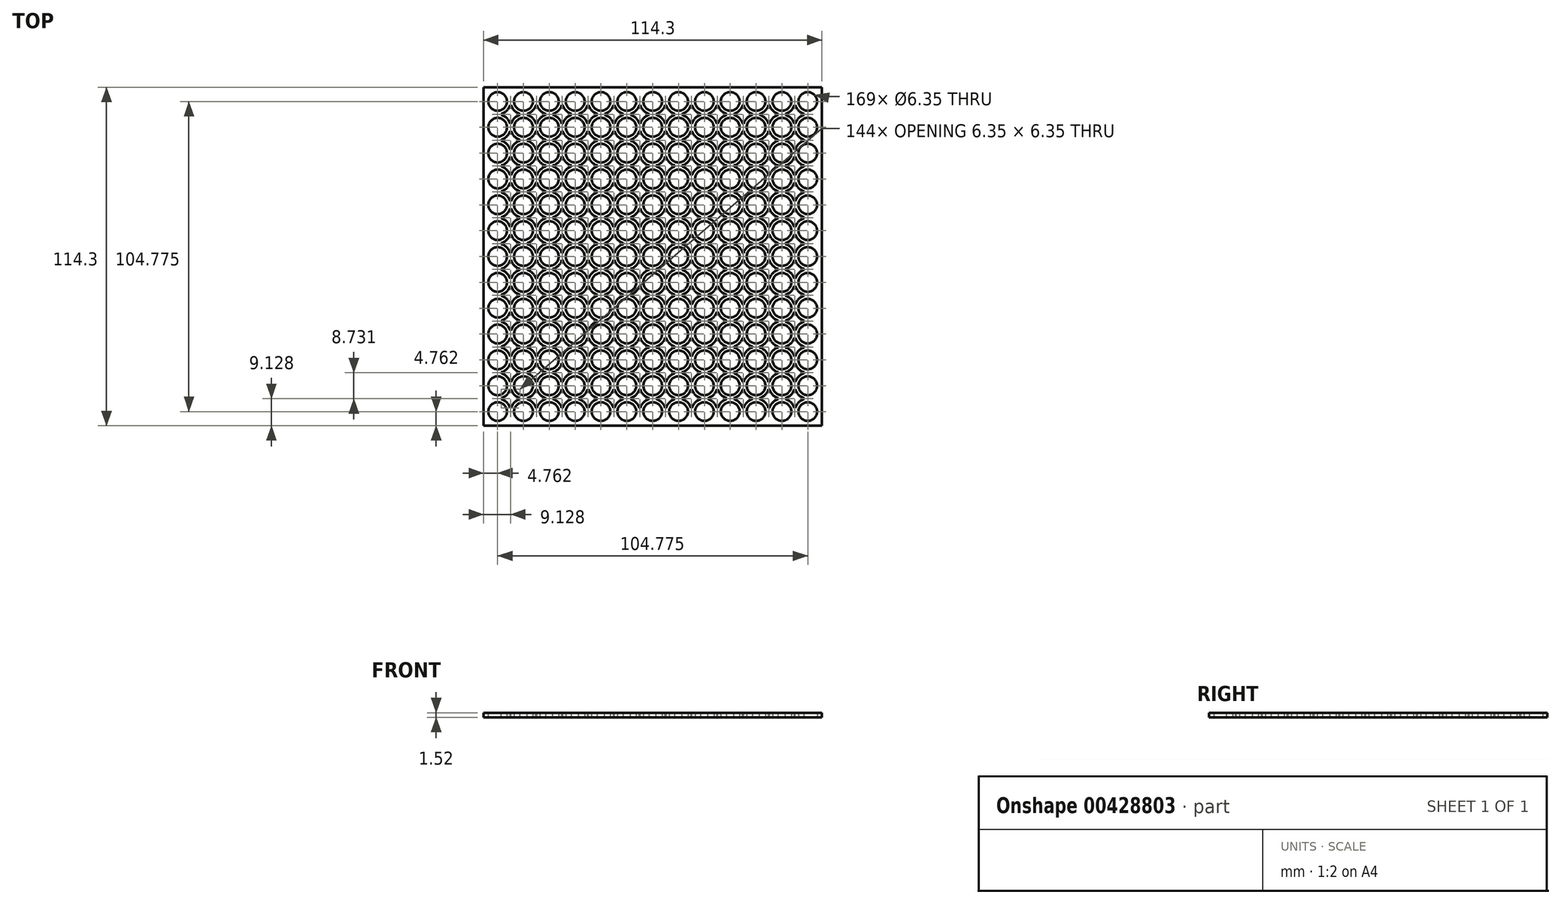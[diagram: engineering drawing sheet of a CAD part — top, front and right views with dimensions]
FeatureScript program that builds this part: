
annotation { "Feature Type Name" : "Feature", "Feature Type Description" : "" }
export const myFeature = defineFeature(function(context is Context, id is Id, definition is map)
    precondition{}
    {
        {
            var Q0;
            Q0=qCreatedBy(makeId("Top.planeOp"),FACE);
            var sketch = newSketch(context, id + "F0", { "sketchPlane" : qUnion([Q0])});
            skLineSegment(sketch, "E0.bottom", {"start": v(-57.15, -57.15) * mm, "end": v(57.15, -57.15) * mm});
            skLineSegment(sketch, "E0.top", {"start": v(-57.15, 57.15) * mm, "end": v(57.15, 57.15) * mm});
            skLineSegment(sketch, "E0.left", {"start": v(-57.15, -57.15) * mm, "end": v(-57.15, 57.15) * mm});
            skLineSegment(sketch, "E0.right", {"start": v(57.15, -57.15) * mm, "end": v(57.15, 57.15) * mm});
            skPoint(sketch, "E0.middle", {"position": v(0, 0) * mm});
            skCircle(sketch, "E1", {"center": v(-52.39, 52.39) * mm, "radius": 3.18 * mm});
            skLineSegment(sketch, "E2", {"start": v(-57.15, 52.39) * mm, "end": v(-52.39, 52.39) * mm, "construction": true});
            skLineSegment(sketch, "E3", {"start": v(-52.39, 57.15) * mm, "end": v(-52.39, 52.39) * mm, "construction": true});
            skLineSegment(sketch, "E4", {"start": v(-57.15, 52.39) * mm, "end": v(-55.56, 52.39) * mm, "construction": true});
            skCircle(sketch, "E5.0.1.0", {"center": v(-52.39, 43.66) * mm, "radius": 3.18 * mm});
            skCircle(sketch, "E5.0.2.0", {"center": v(-52.39, 34.93) * mm, "radius": 3.18 * mm});
            skCircle(sketch, "E5.0.3.0", {"center": v(-52.39, 26.2) * mm, "radius": 3.18 * mm});
            skCircle(sketch, "E5.0.4.0", {"center": v(-52.39, 17.46) * mm, "radius": 3.18 * mm});
            skCircle(sketch, "E5.0.5.0", {"center": v(-52.39, 8.73) * mm, "radius": 3.18 * mm});
            skCircle(sketch, "E5.0.6.0", {"center": v(-52.39, 0) * mm, "radius": 3.18 * mm});
            skCircle(sketch, "E5.0.7.0", {"center": v(-52.39, -8.73) * mm, "radius": 3.18 * mm});
            skCircle(sketch, "E5.0.8.0", {"center": v(-52.39, -17.46) * mm, "radius": 3.18 * mm});
            skCircle(sketch, "E5.0.9.0", {"center": v(-52.39, -26.2) * mm, "radius": 3.18 * mm});
            skCircle(sketch, "E5.0.10.0", {"center": v(-52.39, -34.93) * mm, "radius": 3.18 * mm});
            skCircle(sketch, "E5.0.11.0", {"center": v(-52.39, -43.66) * mm, "radius": 3.18 * mm});
            skCircle(sketch, "E5.0.12.0", {"center": v(-52.39, -52.39) * mm, "radius": 3.18 * mm});
            skCircle(sketch, "E5.1.0.0", {"center": v(-43.66, 52.39) * mm, "radius": 3.18 * mm});
            skCircle(sketch, "E5.1.1.0", {"center": v(-43.66, 43.66) * mm, "radius": 3.18 * mm});
            skCircle(sketch, "E5.1.2.0", {"center": v(-43.66, 34.93) * mm, "radius": 3.18 * mm});
            skCircle(sketch, "E5.1.3.0", {"center": v(-43.66, 26.2) * mm, "radius": 3.18 * mm});
            skCircle(sketch, "E5.1.4.0", {"center": v(-43.66, 17.46) * mm, "radius": 3.18 * mm});
            skCircle(sketch, "E5.1.5.0", {"center": v(-43.66, 8.73) * mm, "radius": 3.18 * mm});
            skCircle(sketch, "E5.1.6.0", {"center": v(-43.66, 0) * mm, "radius": 3.18 * mm});
            skCircle(sketch, "E5.1.7.0", {"center": v(-43.66, -8.73) * mm, "radius": 3.18 * mm});
            skCircle(sketch, "E5.1.8.0", {"center": v(-43.66, -17.46) * mm, "radius": 3.18 * mm});
            skCircle(sketch, "E5.1.9.0", {"center": v(-43.66, -26.2) * mm, "radius": 3.18 * mm});
            skCircle(sketch, "E5.1.10.0", {"center": v(-43.66, -34.93) * mm, "radius": 3.18 * mm});
            skCircle(sketch, "E5.1.11.0", {"center": v(-43.66, -43.66) * mm, "radius": 3.18 * mm});
            skCircle(sketch, "E5.1.12.0", {"center": v(-43.66, -52.39) * mm, "radius": 3.18 * mm});
            skCircle(sketch, "E5.2.0.0", {"center": v(-34.93, 52.39) * mm, "radius": 3.18 * mm});
            skCircle(sketch, "E5.2.1.0", {"center": v(-34.93, 43.66) * mm, "radius": 3.18 * mm});
            skCircle(sketch, "E5.2.2.0", {"center": v(-34.93, 34.93) * mm, "radius": 3.18 * mm});
            skCircle(sketch, "E5.2.3.0", {"center": v(-34.93, 26.2) * mm, "radius": 3.18 * mm});
            skCircle(sketch, "E5.2.4.0", {"center": v(-34.93, 17.46) * mm, "radius": 3.18 * mm});
            skCircle(sketch, "E5.2.5.0", {"center": v(-34.93, 8.73) * mm, "radius": 3.18 * mm});
            skCircle(sketch, "E5.2.6.0", {"center": v(-34.93, 0) * mm, "radius": 3.18 * mm});
            skCircle(sketch, "E5.2.7.0", {"center": v(-34.93, -8.73) * mm, "radius": 3.18 * mm});
            skCircle(sketch, "E5.2.8.0", {"center": v(-34.93, -17.46) * mm, "radius": 3.18 * mm});
            skCircle(sketch, "E5.2.9.0", {"center": v(-34.93, -26.2) * mm, "radius": 3.18 * mm});
            skCircle(sketch, "E5.2.10.0", {"center": v(-34.93, -34.93) * mm, "radius": 3.18 * mm});
            skCircle(sketch, "E5.2.11.0", {"center": v(-34.93, -43.66) * mm, "radius": 3.18 * mm});
            skCircle(sketch, "E5.2.12.0", {"center": v(-34.93, -52.39) * mm, "radius": 3.18 * mm});
            skCircle(sketch, "E5.3.0.0", {"center": v(-26.2, 52.39) * mm, "radius": 3.18 * mm});
            skCircle(sketch, "E5.3.1.0", {"center": v(-26.2, 43.66) * mm, "radius": 3.18 * mm});
            skCircle(sketch, "E5.3.2.0", {"center": v(-26.2, 34.93) * mm, "radius": 3.18 * mm});
            skCircle(sketch, "E5.3.3.0", {"center": v(-26.2, 26.2) * mm, "radius": 3.18 * mm});
            skCircle(sketch, "E5.3.4.0", {"center": v(-26.2, 17.46) * mm, "radius": 3.18 * mm});
            skCircle(sketch, "E5.3.5.0", {"center": v(-26.2, 8.73) * mm, "radius": 3.18 * mm});
            skCircle(sketch, "E5.3.6.0", {"center": v(-26.2, 0) * mm, "radius": 3.18 * mm});
            skCircle(sketch, "E5.3.7.0", {"center": v(-26.2, -8.73) * mm, "radius": 3.18 * mm});
            skCircle(sketch, "E5.3.8.0", {"center": v(-26.2, -17.46) * mm, "radius": 3.18 * mm});
            skCircle(sketch, "E5.3.9.0", {"center": v(-26.2, -26.2) * mm, "radius": 3.18 * mm});
            skCircle(sketch, "E5.3.10.0", {"center": v(-26.2, -34.93) * mm, "radius": 3.18 * mm});
            skCircle(sketch, "E5.3.11.0", {"center": v(-26.2, -43.66) * mm, "radius": 3.18 * mm});
            skCircle(sketch, "E5.3.12.0", {"center": v(-26.2, -52.39) * mm, "radius": 3.18 * mm});
            skCircle(sketch, "E5.4.0.0", {"center": v(-17.46, 52.39) * mm, "radius": 3.18 * mm});
            skCircle(sketch, "E5.4.1.0", {"center": v(-17.46, 43.66) * mm, "radius": 3.18 * mm});
            skCircle(sketch, "E5.4.2.0", {"center": v(-17.46, 34.93) * mm, "radius": 3.18 * mm});
            skCircle(sketch, "E5.4.3.0", {"center": v(-17.46, 26.2) * mm, "radius": 3.18 * mm});
            skCircle(sketch, "E5.4.4.0", {"center": v(-17.46, 17.46) * mm, "radius": 3.18 * mm});
            skCircle(sketch, "E5.4.5.0", {"center": v(-17.46, 8.73) * mm, "radius": 3.18 * mm});
            skCircle(sketch, "E5.4.6.0", {"center": v(-17.46, 0) * mm, "radius": 3.18 * mm});
            skCircle(sketch, "E5.4.7.0", {"center": v(-17.46, -8.73) * mm, "radius": 3.18 * mm});
            skCircle(sketch, "E5.4.8.0", {"center": v(-17.46, -17.46) * mm, "radius": 3.18 * mm});
            skCircle(sketch, "E5.4.9.0", {"center": v(-17.46, -26.2) * mm, "radius": 3.18 * mm});
            skCircle(sketch, "E5.4.10.0", {"center": v(-17.46, -34.93) * mm, "radius": 3.18 * mm});
            skCircle(sketch, "E5.4.11.0", {"center": v(-17.46, -43.66) * mm, "radius": 3.18 * mm});
            skCircle(sketch, "E5.4.12.0", {"center": v(-17.46, -52.39) * mm, "radius": 3.18 * mm});
            skCircle(sketch, "E5.5.0.0", {"center": v(-8.73, 52.39) * mm, "radius": 3.18 * mm});
            skCircle(sketch, "E5.5.1.0", {"center": v(-8.73, 43.66) * mm, "radius": 3.18 * mm});
            skCircle(sketch, "E5.5.2.0", {"center": v(-8.73, 34.93) * mm, "radius": 3.18 * mm});
            skCircle(sketch, "E5.5.3.0", {"center": v(-8.73, 26.2) * mm, "radius": 3.18 * mm});
            skCircle(sketch, "E5.5.4.0", {"center": v(-8.73, 17.46) * mm, "radius": 3.18 * mm});
            skCircle(sketch, "E5.5.5.0", {"center": v(-8.73, 8.73) * mm, "radius": 3.18 * mm});
            skCircle(sketch, "E5.5.6.0", {"center": v(-8.73, 0) * mm, "radius": 3.18 * mm});
            skCircle(sketch, "E5.5.7.0", {"center": v(-8.73, -8.73) * mm, "radius": 3.18 * mm});
            skCircle(sketch, "E5.5.8.0", {"center": v(-8.73, -17.46) * mm, "radius": 3.18 * mm});
            skCircle(sketch, "E5.5.9.0", {"center": v(-8.73, -26.2) * mm, "radius": 3.18 * mm});
            skCircle(sketch, "E5.5.10.0", {"center": v(-8.73, -34.93) * mm, "radius": 3.18 * mm});
            skCircle(sketch, "E5.5.11.0", {"center": v(-8.73, -43.66) * mm, "radius": 3.18 * mm});
            skCircle(sketch, "E5.5.12.0", {"center": v(-8.73, -52.39) * mm, "radius": 3.18 * mm});
            skCircle(sketch, "E5.6.0.0", {"center": v(0, 52.39) * mm, "radius": 3.18 * mm});
            skCircle(sketch, "E5.6.1.0", {"center": v(0, 43.66) * mm, "radius": 3.18 * mm});
            skCircle(sketch, "E5.6.2.0", {"center": v(0, 34.93) * mm, "radius": 3.18 * mm});
            skCircle(sketch, "E5.6.3.0", {"center": v(0, 26.2) * mm, "radius": 3.18 * mm});
            skCircle(sketch, "E5.6.4.0", {"center": v(0, 17.46) * mm, "radius": 3.18 * mm});
            skCircle(sketch, "E5.6.5.0", {"center": v(0, 8.73) * mm, "radius": 3.18 * mm});
            skCircle(sketch, "E5.6.6.0", {"center": v(0, 0) * mm, "radius": 3.18 * mm});
            skCircle(sketch, "E5.6.7.0", {"center": v(0, -8.73) * mm, "radius": 3.18 * mm});
            skCircle(sketch, "E5.6.8.0", {"center": v(0, -17.46) * mm, "radius": 3.18 * mm});
            skCircle(sketch, "E5.6.9.0", {"center": v(0, -26.2) * mm, "radius": 3.18 * mm});
            skCircle(sketch, "E5.6.10.0", {"center": v(0, -34.93) * mm, "radius": 3.18 * mm});
            skCircle(sketch, "E5.6.11.0", {"center": v(0, -43.66) * mm, "radius": 3.18 * mm});
            skCircle(sketch, "E5.6.12.0", {"center": v(0, -52.39) * mm, "radius": 3.18 * mm});
            skCircle(sketch, "E5.7.0.0", {"center": v(8.73, 52.39) * mm, "radius": 3.18 * mm});
            skCircle(sketch, "E5.7.1.0", {"center": v(8.73, 43.66) * mm, "radius": 3.18 * mm});
            skCircle(sketch, "E5.7.2.0", {"center": v(8.73, 34.93) * mm, "radius": 3.18 * mm});
            skCircle(sketch, "E5.7.3.0", {"center": v(8.73, 26.2) * mm, "radius": 3.18 * mm});
            skCircle(sketch, "E5.7.4.0", {"center": v(8.73, 17.46) * mm, "radius": 3.18 * mm});
            skCircle(sketch, "E5.7.5.0", {"center": v(8.73, 8.73) * mm, "radius": 3.18 * mm});
            skCircle(sketch, "E5.7.6.0", {"center": v(8.73, 0) * mm, "radius": 3.18 * mm});
            skCircle(sketch, "E5.7.7.0", {"center": v(8.73, -8.73) * mm, "radius": 3.18 * mm});
            skCircle(sketch, "E5.7.8.0", {"center": v(8.73, -17.46) * mm, "radius": 3.18 * mm});
            skCircle(sketch, "E5.7.9.0", {"center": v(8.73, -26.2) * mm, "radius": 3.18 * mm});
            skCircle(sketch, "E5.7.10.0", {"center": v(8.73, -34.93) * mm, "radius": 3.18 * mm});
            skCircle(sketch, "E5.7.11.0", {"center": v(8.73, -43.66) * mm, "radius": 3.18 * mm});
            skCircle(sketch, "E5.7.12.0", {"center": v(8.73, -52.39) * mm, "radius": 3.18 * mm});
            skCircle(sketch, "E5.8.0.0", {"center": v(17.46, 52.39) * mm, "radius": 3.18 * mm});
            skCircle(sketch, "E5.8.1.0", {"center": v(17.46, 43.66) * mm, "radius": 3.18 * mm});
            skCircle(sketch, "E5.8.2.0", {"center": v(17.46, 34.93) * mm, "radius": 3.18 * mm});
            skCircle(sketch, "E5.8.3.0", {"center": v(17.46, 26.2) * mm, "radius": 3.18 * mm});
            skCircle(sketch, "E5.8.4.0", {"center": v(17.46, 17.46) * mm, "radius": 3.18 * mm});
            skCircle(sketch, "E5.8.5.0", {"center": v(17.46, 8.73) * mm, "radius": 3.18 * mm});
            skCircle(sketch, "E5.8.6.0", {"center": v(17.46, 0) * mm, "radius": 3.18 * mm});
            skCircle(sketch, "E5.8.7.0", {"center": v(17.46, -8.73) * mm, "radius": 3.18 * mm});
            skCircle(sketch, "E5.8.8.0", {"center": v(17.46, -17.46) * mm, "radius": 3.18 * mm});
            skCircle(sketch, "E5.8.9.0", {"center": v(17.46, -26.2) * mm, "radius": 3.18 * mm});
            skCircle(sketch, "E5.8.10.0", {"center": v(17.46, -34.93) * mm, "radius": 3.18 * mm});
            skCircle(sketch, "E5.8.11.0", {"center": v(17.46, -43.66) * mm, "radius": 3.18 * mm});
            skCircle(sketch, "E5.8.12.0", {"center": v(17.46, -52.39) * mm, "radius": 3.18 * mm});
            skCircle(sketch, "E5.9.0.0", {"center": v(26.2, 52.39) * mm, "radius": 3.18 * mm});
            skCircle(sketch, "E5.9.1.0", {"center": v(26.2, 43.66) * mm, "radius": 3.18 * mm});
            skCircle(sketch, "E5.9.2.0", {"center": v(26.2, 34.93) * mm, "radius": 3.18 * mm});
            skCircle(sketch, "E5.9.3.0", {"center": v(26.2, 26.2) * mm, "radius": 3.18 * mm});
            skCircle(sketch, "E5.9.4.0", {"center": v(26.2, 17.46) * mm, "radius": 3.18 * mm});
            skCircle(sketch, "E5.9.5.0", {"center": v(26.2, 8.73) * mm, "radius": 3.18 * mm});
            skCircle(sketch, "E5.9.6.0", {"center": v(26.2, 0) * mm, "radius": 3.18 * mm});
            skCircle(sketch, "E5.9.7.0", {"center": v(26.2, -8.73) * mm, "radius": 3.18 * mm});
            skCircle(sketch, "E5.9.8.0", {"center": v(26.2, -17.46) * mm, "radius": 3.18 * mm});
            skCircle(sketch, "E5.9.9.0", {"center": v(26.2, -26.2) * mm, "radius": 3.18 * mm});
            skCircle(sketch, "E5.9.10.0", {"center": v(26.2, -34.93) * mm, "radius": 3.18 * mm});
            skCircle(sketch, "E5.9.11.0", {"center": v(26.2, -43.66) * mm, "radius": 3.18 * mm});
            skCircle(sketch, "E5.9.12.0", {"center": v(26.2, -52.39) * mm, "radius": 3.18 * mm});
            skCircle(sketch, "E5.10.0.0", {"center": v(34.93, 52.39) * mm, "radius": 3.18 * mm});
            skCircle(sketch, "E5.10.1.0", {"center": v(34.93, 43.66) * mm, "radius": 3.18 * mm});
            skCircle(sketch, "E5.10.2.0", {"center": v(34.93, 34.93) * mm, "radius": 3.18 * mm});
            skCircle(sketch, "E5.10.3.0", {"center": v(34.93, 26.2) * mm, "radius": 3.18 * mm});
            skCircle(sketch, "E5.10.4.0", {"center": v(34.93, 17.46) * mm, "radius": 3.18 * mm});
            skCircle(sketch, "E5.10.5.0", {"center": v(34.93, 8.73) * mm, "radius": 3.18 * mm});
            skCircle(sketch, "E5.10.6.0", {"center": v(34.93, 0) * mm, "radius": 3.18 * mm});
            skCircle(sketch, "E5.10.7.0", {"center": v(34.93, -8.73) * mm, "radius": 3.18 * mm});
            skCircle(sketch, "E5.10.8.0", {"center": v(34.93, -17.46) * mm, "radius": 3.18 * mm});
            skCircle(sketch, "E5.10.9.0", {"center": v(34.93, -26.2) * mm, "radius": 3.18 * mm});
            skCircle(sketch, "E5.10.10.0", {"center": v(34.93, -34.93) * mm, "radius": 3.18 * mm});
            skCircle(sketch, "E5.10.11.0", {"center": v(34.93, -43.66) * mm, "radius": 3.18 * mm});
            skCircle(sketch, "E5.10.12.0", {"center": v(34.93, -52.39) * mm, "radius": 3.18 * mm});
            skCircle(sketch, "E5.11.0.0", {"center": v(43.66, 52.39) * mm, "radius": 3.18 * mm});
            skCircle(sketch, "E5.11.1.0", {"center": v(43.66, 43.66) * mm, "radius": 3.18 * mm});
            skCircle(sketch, "E5.11.2.0", {"center": v(43.66, 34.93) * mm, "radius": 3.18 * mm});
            skCircle(sketch, "E5.11.3.0", {"center": v(43.66, 26.2) * mm, "radius": 3.18 * mm});
            skCircle(sketch, "E5.11.4.0", {"center": v(43.66, 17.46) * mm, "radius": 3.18 * mm});
            skCircle(sketch, "E5.11.5.0", {"center": v(43.66, 8.73) * mm, "radius": 3.18 * mm});
            skCircle(sketch, "E5.11.6.0", {"center": v(43.66, 0) * mm, "radius": 3.18 * mm});
            skCircle(sketch, "E5.11.7.0", {"center": v(43.66, -8.73) * mm, "radius": 3.18 * mm});
            skCircle(sketch, "E5.11.8.0", {"center": v(43.66, -17.46) * mm, "radius": 3.18 * mm});
            skCircle(sketch, "E5.11.9.0", {"center": v(43.66, -26.2) * mm, "radius": 3.18 * mm});
            skCircle(sketch, "E5.11.10.0", {"center": v(43.66, -34.93) * mm, "radius": 3.18 * mm});
            skCircle(sketch, "E5.11.11.0", {"center": v(43.66, -43.66) * mm, "radius": 3.18 * mm});
            skCircle(sketch, "E5.11.12.0", {"center": v(43.66, -52.39) * mm, "radius": 3.18 * mm});
            skCircle(sketch, "E5.12.0.0", {"center": v(52.39, 52.39) * mm, "radius": 3.18 * mm});
            skCircle(sketch, "E5.12.1.0", {"center": v(52.39, 43.66) * mm, "radius": 3.18 * mm});
            skCircle(sketch, "E5.12.2.0", {"center": v(52.39, 34.93) * mm, "radius": 3.18 * mm});
            skCircle(sketch, "E5.12.3.0", {"center": v(52.39, 26.2) * mm, "radius": 3.18 * mm});
            skCircle(sketch, "E5.12.4.0", {"center": v(52.39, 17.46) * mm, "radius": 3.18 * mm});
            skCircle(sketch, "E5.12.5.0", {"center": v(52.39, 8.73) * mm, "radius": 3.18 * mm});
            skCircle(sketch, "E5.12.6.0", {"center": v(52.39, 0) * mm, "radius": 3.18 * mm});
            skCircle(sketch, "E5.12.7.0", {"center": v(52.39, -8.73) * mm, "radius": 3.18 * mm});
            skCircle(sketch, "E5.12.8.0", {"center": v(52.39, -17.46) * mm, "radius": 3.18 * mm});
            skCircle(sketch, "E5.12.9.0", {"center": v(52.39, -26.2) * mm, "radius": 3.18 * mm});
            skCircle(sketch, "E5.12.10.0", {"center": v(52.39, -34.93) * mm, "radius": 3.18 * mm});
            skCircle(sketch, "E5.12.11.0", {"center": v(52.39, -43.66) * mm, "radius": 3.18 * mm});
            skCircle(sketch, "E5.12.12.0", {"center": v(52.39, -52.39) * mm, "radius": 3.18 * mm});
            skLineSegment(sketch, "E5.direction1", {"start": v(-52.39, 52.39) * mm, "end": v(-43.66, 52.39) * mm, "construction": true});
            skLineSegment(sketch, "E5.direction2", {"start": v(-52.39, 52.39) * mm, "end": v(-52.39, 43.66) * mm, "construction": true});
            skLineSegment(sketch, "E6", {"start": v(52.39, 52.39) * mm, "end": v(57.15, 52.39) * mm, "construction": true});
            skLineSegment(sketch, "E7", {"start": v(-52.39, -52.39) * mm, "end": v(-52.39, -57.15) * mm, "construction": true});
            skSolve(sketch);
        }
        {
            var Q0;
            Q0=makeQuery(id+"F0.imprint","IMPRINT",FACE,{"disambiguationData":[TD([[makeQuery(id+"F0.imprint","IMPRINT",EDGE,{"derivedFrom":sQuery(id+"F0.wireOp",EDGE,"E0.bottom")}),1.0]])]});
            extrude(context, id + "F1", {"entities" : qUnion([Q0]), "depth" : 1.52 * mm});
        }
        {
            var Q0;
            Q0=makeQuery(id+"F1.opExtrude","CAP_FACE",FACE,{"disambiguationData":[OSD([sQuery(id+"F0.wireOp",EDGE,"E0.bottom"),sQuery(id+"F0.wireOp",EDGE,"E0.top"),sQuery(id+"F0.wireOp",EDGE,"E0.left"),sQuery(id+"F0.wireOp",EDGE,"E0.right"),sQuery(id+"F0.wireOp",EDGE,"E1"),sQuery(id+"F0.wireOp",EDGE,"E5.0.1.0"),sQuery(id+"F0.wireOp",EDGE,"E5.0.2.0"),sQuery(id+"F0.wireOp",EDGE,"E5.0.3.0"),sQuery(id+"F0.wireOp",EDGE,"E5.0.4.0"),sQuery(id+"F0.wireOp",EDGE,"E5.0.5.0"),sQuery(id+"F0.wireOp",EDGE,"E5.0.6.0"),sQuery(id+"F0.wireOp",EDGE,"E5.0.7.0"),sQuery(id+"F0.wireOp",EDGE,"E5.0.8.0"),sQuery(id+"F0.wireOp",EDGE,"E5.0.9.0"),sQuery(id+"F0.wireOp",EDGE,"E5.0.10.0"),sQuery(id+"F0.wireOp",EDGE,"E5.0.11.0"),sQuery(id+"F0.wireOp",EDGE,"E5.0.12.0"),sQuery(id+"F0.wireOp",EDGE,"E5.1.0.0"),sQuery(id+"F0.wireOp",EDGE,"E5.1.1.0"),sQuery(id+"F0.wireOp",EDGE,"E5.1.2.0"),sQuery(id+"F0.wireOp",EDGE,"E5.1.3.0"),sQuery(id+"F0.wireOp",EDGE,"E5.1.4.0"),sQuery(id+"F0.wireOp",EDGE,"E5.1.5.0"),sQuery(id+"F0.wireOp",EDGE,"E5.1.6.0"),sQuery(id+"F0.wireOp",EDGE,"E5.1.7.0"),sQuery(id+"F0.wireOp",EDGE,"E5.1.8.0"),sQuery(id+"F0.wireOp",EDGE,"E5.1.9.0"),sQuery(id+"F0.wireOp",EDGE,"E5.1.10.0"),sQuery(id+"F0.wireOp",EDGE,"E5.1.11.0"),sQuery(id+"F0.wireOp",EDGE,"E5.1.12.0"),sQuery(id+"F0.wireOp",EDGE,"E5.2.0.0"),sQuery(id+"F0.wireOp",EDGE,"E5.2.1.0"),sQuery(id+"F0.wireOp",EDGE,"E5.2.2.0"),sQuery(id+"F0.wireOp",EDGE,"E5.2.3.0"),sQuery(id+"F0.wireOp",EDGE,"E5.2.4.0"),sQuery(id+"F0.wireOp",EDGE,"E5.2.5.0"),sQuery(id+"F0.wireOp",EDGE,"E5.2.6.0"),sQuery(id+"F0.wireOp",EDGE,"E5.2.7.0"),sQuery(id+"F0.wireOp",EDGE,"E5.2.8.0"),sQuery(id+"F0.wireOp",EDGE,"E5.2.9.0"),sQuery(id+"F0.wireOp",EDGE,"E5.2.10.0"),sQuery(id+"F0.wireOp",EDGE,"E5.2.11.0"),sQuery(id+"F0.wireOp",EDGE,"E5.2.12.0"),sQuery(id+"F0.wireOp",EDGE,"E5.3.0.0"),sQuery(id+"F0.wireOp",EDGE,"E5.3.1.0"),sQuery(id+"F0.wireOp",EDGE,"E5.3.2.0"),sQuery(id+"F0.wireOp",EDGE,"E5.3.3.0"),sQuery(id+"F0.wireOp",EDGE,"E5.3.4.0"),sQuery(id+"F0.wireOp",EDGE,"E5.3.5.0"),sQuery(id+"F0.wireOp",EDGE,"E5.3.6.0"),sQuery(id+"F0.wireOp",EDGE,"E5.3.7.0"),sQuery(id+"F0.wireOp",EDGE,"E5.3.8.0"),sQuery(id+"F0.wireOp",EDGE,"E5.3.9.0"),sQuery(id+"F0.wireOp",EDGE,"E5.3.10.0"),sQuery(id+"F0.wireOp",EDGE,"E5.3.11.0"),sQuery(id+"F0.wireOp",EDGE,"E5.3.12.0"),sQuery(id+"F0.wireOp",EDGE,"E5.4.0.0"),sQuery(id+"F0.wireOp",EDGE,"E5.4.1.0"),sQuery(id+"F0.wireOp",EDGE,"E5.4.2.0"),sQuery(id+"F0.wireOp",EDGE,"E5.4.3.0"),sQuery(id+"F0.wireOp",EDGE,"E5.4.4.0"),sQuery(id+"F0.wireOp",EDGE,"E5.4.5.0"),sQuery(id+"F0.wireOp",EDGE,"E5.4.6.0"),sQuery(id+"F0.wireOp",EDGE,"E5.4.7.0"),sQuery(id+"F0.wireOp",EDGE,"E5.4.8.0"),sQuery(id+"F0.wireOp",EDGE,"E5.4.9.0"),sQuery(id+"F0.wireOp",EDGE,"E5.4.10.0"),sQuery(id+"F0.wireOp",EDGE,"E5.4.11.0"),sQuery(id+"F0.wireOp",EDGE,"E5.4.12.0"),sQuery(id+"F0.wireOp",EDGE,"E5.5.0.0"),sQuery(id+"F0.wireOp",EDGE,"E5.5.1.0"),sQuery(id+"F0.wireOp",EDGE,"E5.5.2.0"),sQuery(id+"F0.wireOp",EDGE,"E5.5.3.0"),sQuery(id+"F0.wireOp",EDGE,"E5.5.4.0"),sQuery(id+"F0.wireOp",EDGE,"E5.5.5.0"),sQuery(id+"F0.wireOp",EDGE,"E5.5.6.0"),sQuery(id+"F0.wireOp",EDGE,"E5.5.7.0"),sQuery(id+"F0.wireOp",EDGE,"E5.5.8.0"),sQuery(id+"F0.wireOp",EDGE,"E5.5.9.0"),sQuery(id+"F0.wireOp",EDGE,"E5.5.10.0"),sQuery(id+"F0.wireOp",EDGE,"E5.5.11.0"),sQuery(id+"F0.wireOp",EDGE,"E5.5.12.0"),sQuery(id+"F0.wireOp",EDGE,"E5.6.0.0"),sQuery(id+"F0.wireOp",EDGE,"E5.6.1.0"),sQuery(id+"F0.wireOp",EDGE,"E5.6.2.0"),sQuery(id+"F0.wireOp",EDGE,"E5.6.3.0"),sQuery(id+"F0.wireOp",EDGE,"E5.6.4.0"),sQuery(id+"F0.wireOp",EDGE,"E5.6.5.0"),sQuery(id+"F0.wireOp",EDGE,"E5.6.6.0"),sQuery(id+"F0.wireOp",EDGE,"E5.6.7.0"),sQuery(id+"F0.wireOp",EDGE,"E5.6.8.0"),sQuery(id+"F0.wireOp",EDGE,"E5.6.9.0"),sQuery(id+"F0.wireOp",EDGE,"E5.6.10.0"),sQuery(id+"F0.wireOp",EDGE,"E5.6.11.0"),sQuery(id+"F0.wireOp",EDGE,"E5.6.12.0"),sQuery(id+"F0.wireOp",EDGE,"E5.7.0.0"),sQuery(id+"F0.wireOp",EDGE,"E5.7.1.0"),sQuery(id+"F0.wireOp",EDGE,"E5.7.2.0"),sQuery(id+"F0.wireOp",EDGE,"E5.7.3.0"),sQuery(id+"F0.wireOp",EDGE,"E5.7.4.0"),sQuery(id+"F0.wireOp",EDGE,"E5.7.5.0"),sQuery(id+"F0.wireOp",EDGE,"E5.7.6.0"),sQuery(id+"F0.wireOp",EDGE,"E5.7.7.0"),sQuery(id+"F0.wireOp",EDGE,"E5.7.8.0"),sQuery(id+"F0.wireOp",EDGE,"E5.7.9.0"),sQuery(id+"F0.wireOp",EDGE,"E5.7.10.0"),sQuery(id+"F0.wireOp",EDGE,"E5.7.11.0"),sQuery(id+"F0.wireOp",EDGE,"E5.7.12.0"),sQuery(id+"F0.wireOp",EDGE,"E5.8.0.0"),sQuery(id+"F0.wireOp",EDGE,"E5.8.1.0"),sQuery(id+"F0.wireOp",EDGE,"E5.8.2.0"),sQuery(id+"F0.wireOp",EDGE,"E5.8.3.0"),sQuery(id+"F0.wireOp",EDGE,"E5.8.4.0"),sQuery(id+"F0.wireOp",EDGE,"E5.8.5.0"),sQuery(id+"F0.wireOp",EDGE,"E5.8.6.0"),sQuery(id+"F0.wireOp",EDGE,"E5.8.7.0"),sQuery(id+"F0.wireOp",EDGE,"E5.8.8.0"),sQuery(id+"F0.wireOp",EDGE,"E5.8.9.0"),sQuery(id+"F0.wireOp",EDGE,"E5.8.10.0"),sQuery(id+"F0.wireOp",EDGE,"E5.8.11.0"),sQuery(id+"F0.wireOp",EDGE,"E5.8.12.0"),sQuery(id+"F0.wireOp",EDGE,"E5.9.0.0"),sQuery(id+"F0.wireOp",EDGE,"E5.9.1.0"),sQuery(id+"F0.wireOp",EDGE,"E5.9.2.0"),sQuery(id+"F0.wireOp",EDGE,"E5.9.3.0"),sQuery(id+"F0.wireOp",EDGE,"E5.9.4.0"),sQuery(id+"F0.wireOp",EDGE,"E5.9.5.0"),sQuery(id+"F0.wireOp",EDGE,"E5.9.6.0"),sQuery(id+"F0.wireOp",EDGE,"E5.9.7.0"),sQuery(id+"F0.wireOp",EDGE,"E5.9.8.0"),sQuery(id+"F0.wireOp",EDGE,"E5.9.9.0"),sQuery(id+"F0.wireOp",EDGE,"E5.9.10.0"),sQuery(id+"F0.wireOp",EDGE,"E5.9.11.0"),sQuery(id+"F0.wireOp",EDGE,"E5.9.12.0"),sQuery(id+"F0.wireOp",EDGE,"E5.10.0.0"),sQuery(id+"F0.wireOp",EDGE,"E5.10.1.0"),sQuery(id+"F0.wireOp",EDGE,"E5.10.2.0"),sQuery(id+"F0.wireOp",EDGE,"E5.10.3.0"),sQuery(id+"F0.wireOp",EDGE,"E5.10.4.0"),sQuery(id+"F0.wireOp",EDGE,"E5.10.5.0"),sQuery(id+"F0.wireOp",EDGE,"E5.10.6.0"),sQuery(id+"F0.wireOp",EDGE,"E5.10.7.0"),sQuery(id+"F0.wireOp",EDGE,"E5.10.8.0"),sQuery(id+"F0.wireOp",EDGE,"E5.10.9.0"),sQuery(id+"F0.wireOp",EDGE,"E5.10.10.0"),sQuery(id+"F0.wireOp",EDGE,"E5.10.11.0"),sQuery(id+"F0.wireOp",EDGE,"E5.10.12.0"),sQuery(id+"F0.wireOp",EDGE,"E5.11.0.0"),sQuery(id+"F0.wireOp",EDGE,"E5.11.1.0"),sQuery(id+"F0.wireOp",EDGE,"E5.11.2.0"),sQuery(id+"F0.wireOp",EDGE,"E5.11.3.0"),sQuery(id+"F0.wireOp",EDGE,"E5.11.4.0"),sQuery(id+"F0.wireOp",EDGE,"E5.11.5.0"),sQuery(id+"F0.wireOp",EDGE,"E5.11.6.0"),sQuery(id+"F0.wireOp",EDGE,"E5.11.7.0"),sQuery(id+"F0.wireOp",EDGE,"E5.11.8.0"),sQuery(id+"F0.wireOp",EDGE,"E5.11.9.0"),sQuery(id+"F0.wireOp",EDGE,"E5.11.10.0"),sQuery(id+"F0.wireOp",EDGE,"E5.11.11.0"),sQuery(id+"F0.wireOp",EDGE,"E5.11.12.0"),sQuery(id+"F0.wireOp",EDGE,"E5.12.0.0"),sQuery(id+"F0.wireOp",EDGE,"E5.12.1.0"),sQuery(id+"F0.wireOp",EDGE,"E5.12.2.0"),sQuery(id+"F0.wireOp",EDGE,"E5.12.3.0"),sQuery(id+"F0.wireOp",EDGE,"E5.12.4.0"),sQuery(id+"F0.wireOp",EDGE,"E5.12.5.0"),sQuery(id+"F0.wireOp",EDGE,"E5.12.6.0"),sQuery(id+"F0.wireOp",EDGE,"E5.12.7.0"),sQuery(id+"F0.wireOp",EDGE,"E5.12.8.0"),sQuery(id+"F0.wireOp",EDGE,"E5.12.9.0"),sQuery(id+"F0.wireOp",EDGE,"E5.12.10.0"),sQuery(id+"F0.wireOp",EDGE,"E5.12.11.0"),sQuery(id+"F0.wireOp",EDGE,"E5.12.12.0")])],"isStart":false});
            var sketch = newSketch(context, id + "F2", { "sketchPlane" : qUnion([Q0])});
            skArc(sketch, "E8", {"start": v(-51.2, 48.19) * mm, "mid": v(-49.3, 49.3) * mm, "end": v(-48.19, 51.2) * mm});
            skArc(sketch, "E9", {"start": v(-47.86, 51.2) * mm, "mid": v(-46.74, 49.3) * mm, "end": v(-44.85, 48.19) * mm});
            skArc(sketch, "E10", {"start": v(-44.85, 47.86) * mm, "mid": v(-46.74, 46.74) * mm, "end": v(-47.86, 44.85) * mm});
            skArc(sketch, "E11", {"start": v(-48.19, 44.85) * mm, "mid": v(-49.3, 46.74) * mm, "end": v(-51.2, 47.86) * mm});
            skLineSegment(sketch, "E12", {"start": v(-52.39, 52.39) * mm, "end": v(-43.66, 43.66) * mm, "construction": true});
            skArc(sketch, "E13", {"start": v(-51.2, 48.19) * mm, "mid": v(-51.2, 48.02) * mm, "end": v(-51.2, 47.86) * mm});
            skArc(sketch, "E14.trimOffspring", {"start": v(-47.86, 51.2) * mm, "mid": v(-48.02, 51.2) * mm, "end": v(-48.19, 51.2) * mm});
            skArc(sketch, "E15.trimOffspring", {"start": v(-44.85, 47.86) * mm, "mid": v(-44.85, 48.02) * mm, "end": v(-44.85, 48.19) * mm});
            skArc(sketch, "E16.trimOffspring", {"start": v(-48.19, 44.85) * mm, "mid": v(-48.02, 44.85) * mm, "end": v(-47.86, 44.85) * mm});
            skArc(sketch, "E17.0.1.0", {"start": v(-47.86, 42.46) * mm, "mid": v(-46.74, 40.57) * mm, "end": v(-44.85, 39.46) * mm});
            skArc(sketch, "E17.0.1.1", {"start": v(-51.2, 39.46) * mm, "mid": v(-49.3, 40.57) * mm, "end": v(-48.19, 42.46) * mm});
            skArc(sketch, "E17.0.1.2", {"start": v(-47.86, 42.46) * mm, "mid": v(-48.02, 42.47) * mm, "end": v(-48.19, 42.46) * mm});
            skArc(sketch, "E17.0.1.3", {"start": v(-51.2, 39.46) * mm, "mid": v(-51.2, 39.3) * mm, "end": v(-51.2, 39.12) * mm});
            skArc(sketch, "E17.0.1.4", {"start": v(-48.19, 36.12) * mm, "mid": v(-49.3, 38.01) * mm, "end": v(-51.2, 39.12) * mm});
            skArc(sketch, "E17.0.1.5", {"start": v(-44.85, 39.12) * mm, "mid": v(-46.74, 38.01) * mm, "end": v(-47.86, 36.12) * mm});
            skArc(sketch, "E17.0.1.6", {"start": v(-48.19, 36.12) * mm, "mid": v(-48.02, 36.12) * mm, "end": v(-47.86, 36.12) * mm});
            skArc(sketch, "E17.0.1.7", {"start": v(-44.85, 39.12) * mm, "mid": v(-44.85, 39.3) * mm, "end": v(-44.85, 39.46) * mm});
            skArc(sketch, "E17.0.2.0", {"start": v(-47.86, 33.73) * mm, "mid": v(-46.74, 31.84) * mm, "end": v(-44.85, 30.73) * mm});
            skArc(sketch, "E17.0.2.1", {"start": v(-51.2, 30.73) * mm, "mid": v(-49.3, 31.84) * mm, "end": v(-48.19, 33.73) * mm});
            skArc(sketch, "E17.0.2.2", {"start": v(-47.86, 33.73) * mm, "mid": v(-48.02, 33.73) * mm, "end": v(-48.19, 33.73) * mm});
            skArc(sketch, "E17.0.2.3", {"start": v(-51.2, 30.73) * mm, "mid": v(-51.2, 30.56) * mm, "end": v(-51.2, 30.4) * mm});
            skArc(sketch, "E17.0.2.4", {"start": v(-48.19, 27.39) * mm, "mid": v(-49.3, 29.28) * mm, "end": v(-51.2, 30.4) * mm});
            skArc(sketch, "E17.0.2.5", {"start": v(-44.85, 30.4) * mm, "mid": v(-46.74, 29.28) * mm, "end": v(-47.86, 27.39) * mm});
            skArc(sketch, "E17.0.2.6", {"start": v(-48.19, 27.39) * mm, "mid": v(-48.02, 27.38) * mm, "end": v(-47.86, 27.39) * mm});
            skArc(sketch, "E17.0.2.7", {"start": v(-44.85, 30.4) * mm, "mid": v(-44.85, 30.56) * mm, "end": v(-44.85, 30.73) * mm});
            skArc(sketch, "E17.0.3.0", {"start": v(-47.86, 25) * mm, "mid": v(-46.74, 23.1) * mm, "end": v(-44.85, 22) * mm});
            skArc(sketch, "E17.0.3.1", {"start": v(-51.2, 22) * mm, "mid": v(-49.3, 23.1) * mm, "end": v(-48.19, 25) * mm});
            skArc(sketch, "E17.0.3.2", {"start": v(-47.86, 25) * mm, "mid": v(-48.02, 25) * mm, "end": v(-48.19, 25) * mm});
            skArc(sketch, "E17.0.3.3", {"start": v(-51.2, 22) * mm, "mid": v(-51.2, 21.83) * mm, "end": v(-51.2, 21.66) * mm});
            skArc(sketch, "E17.0.3.4", {"start": v(-48.19, 18.66) * mm, "mid": v(-49.3, 20.55) * mm, "end": v(-51.2, 21.66) * mm});
            skArc(sketch, "E17.0.3.5", {"start": v(-44.85, 21.66) * mm, "mid": v(-46.74, 20.55) * mm, "end": v(-47.86, 18.66) * mm});
            skArc(sketch, "E17.0.3.6", {"start": v(-48.19, 18.66) * mm, "mid": v(-48.02, 18.65) * mm, "end": v(-47.86, 18.66) * mm});
            skArc(sketch, "E17.0.3.7", {"start": v(-44.85, 21.66) * mm, "mid": v(-44.85, 21.83) * mm, "end": v(-44.85, 22) * mm});
            skArc(sketch, "E17.0.4.0", {"start": v(-47.86, 16.27) * mm, "mid": v(-46.74, 14.38) * mm, "end": v(-44.85, 13.26) * mm});
            skArc(sketch, "E17.0.4.1", {"start": v(-51.2, 13.26) * mm, "mid": v(-49.3, 14.38) * mm, "end": v(-48.19, 16.27) * mm});
            skArc(sketch, "E17.0.4.2", {"start": v(-47.86, 16.27) * mm, "mid": v(-48.02, 16.27) * mm, "end": v(-48.19, 16.27) * mm});
            skArc(sketch, "E17.0.4.3", {"start": v(-51.2, 13.26) * mm, "mid": v(-51.2, 13.1) * mm, "end": v(-51.2, 12.93) * mm});
            skArc(sketch, "E17.0.4.4", {"start": v(-48.19, 9.93) * mm, "mid": v(-49.3, 11.82) * mm, "end": v(-51.2, 12.93) * mm});
            skArc(sketch, "E17.0.4.5", {"start": v(-44.85, 12.93) * mm, "mid": v(-46.74, 11.82) * mm, "end": v(-47.86, 9.93) * mm});
            skArc(sketch, "E17.0.4.6", {"start": v(-48.19, 9.93) * mm, "mid": v(-48.02, 9.92) * mm, "end": v(-47.86, 9.93) * mm});
            skArc(sketch, "E17.0.4.7", {"start": v(-44.85, 12.93) * mm, "mid": v(-44.85, 13.1) * mm, "end": v(-44.85, 13.26) * mm});
            skArc(sketch, "E17.0.5.0", {"start": v(-47.86, 7.54) * mm, "mid": v(-46.74, 5.64) * mm, "end": v(-44.85, 4.53) * mm});
            skArc(sketch, "E17.0.5.1", {"start": v(-51.2, 4.53) * mm, "mid": v(-49.3, 5.64) * mm, "end": v(-48.19, 7.54) * mm});
            skArc(sketch, "E17.0.5.2", {"start": v(-47.86, 7.54) * mm, "mid": v(-48.02, 7.54) * mm, "end": v(-48.19, 7.54) * mm});
            skArc(sketch, "E17.0.5.3", {"start": v(-51.2, 4.53) * mm, "mid": v(-51.2, 4.37) * mm, "end": v(-51.2, 4.2) * mm});
            skArc(sketch, "E17.0.5.4", {"start": v(-48.19, 1.2) * mm, "mid": v(-49.3, 3.09) * mm, "end": v(-51.2, 4.2) * mm});
            skArc(sketch, "E17.0.5.5", {"start": v(-44.85, 4.2) * mm, "mid": v(-46.74, 3.09) * mm, "end": v(-47.86, 1.2) * mm});
            skArc(sketch, "E17.0.5.6", {"start": v(-48.19, 1.2) * mm, "mid": v(-48.02, 1.2) * mm, "end": v(-47.86, 1.2) * mm});
            skArc(sketch, "E17.0.5.7", {"start": v(-44.85, 4.2) * mm, "mid": v(-44.85, 4.37) * mm, "end": v(-44.85, 4.53) * mm});
            skArc(sketch, "E17.0.6.0", {"start": v(-47.86, -1.2) * mm, "mid": v(-46.74, -3.09) * mm, "end": v(-44.85, -4.2) * mm});
            skArc(sketch, "E17.0.6.1", {"start": v(-51.2, -4.2) * mm, "mid": v(-49.3, -3.09) * mm, "end": v(-48.19, -1.2) * mm});
            skArc(sketch, "E17.0.6.2", {"start": v(-47.86, -1.2) * mm, "mid": v(-48.02, -1.2) * mm, "end": v(-48.19, -1.2) * mm});
            skArc(sketch, "E17.0.6.3", {"start": v(-51.2, -4.2) * mm, "mid": v(-51.2, -4.37) * mm, "end": v(-51.2, -4.53) * mm});
            skArc(sketch, "E17.0.6.4", {"start": v(-48.19, -7.54) * mm, "mid": v(-49.3, -5.64) * mm, "end": v(-51.2, -4.53) * mm});
            skArc(sketch, "E17.0.6.5", {"start": v(-44.85, -4.53) * mm, "mid": v(-46.74, -5.64) * mm, "end": v(-47.86, -7.54) * mm});
            skArc(sketch, "E17.0.6.6", {"start": v(-48.19, -7.54) * mm, "mid": v(-48.02, -7.54) * mm, "end": v(-47.86, -7.54) * mm});
            skArc(sketch, "E17.0.6.7", {"start": v(-44.85, -4.53) * mm, "mid": v(-44.85, -4.37) * mm, "end": v(-44.85, -4.2) * mm});
            skArc(sketch, "E17.0.7.0", {"start": v(-47.86, -9.93) * mm, "mid": v(-46.74, -11.82) * mm, "end": v(-44.85, -12.93) * mm});
            skArc(sketch, "E17.0.7.1", {"start": v(-51.2, -12.93) * mm, "mid": v(-49.3, -11.82) * mm, "end": v(-48.19, -9.93) * mm});
            skArc(sketch, "E17.0.7.2", {"start": v(-47.86, -9.93) * mm, "mid": v(-48.02, -9.92) * mm, "end": v(-48.19, -9.93) * mm});
            skArc(sketch, "E17.0.7.3", {"start": v(-51.2, -12.93) * mm, "mid": v(-51.2, -13.1) * mm, "end": v(-51.2, -13.26) * mm});
            skArc(sketch, "E17.0.7.4", {"start": v(-48.19, -16.27) * mm, "mid": v(-49.3, -14.38) * mm, "end": v(-51.2, -13.26) * mm});
            skArc(sketch, "E17.0.7.5", {"start": v(-44.85, -13.26) * mm, "mid": v(-46.74, -14.38) * mm, "end": v(-47.86, -16.27) * mm});
            skArc(sketch, "E17.0.7.6", {"start": v(-48.19, -16.27) * mm, "mid": v(-48.02, -16.27) * mm, "end": v(-47.86, -16.27) * mm});
            skArc(sketch, "E17.0.7.7", {"start": v(-44.85, -13.26) * mm, "mid": v(-44.85, -13.1) * mm, "end": v(-44.85, -12.93) * mm});
            skArc(sketch, "E17.0.8.0", {"start": v(-47.86, -18.66) * mm, "mid": v(-46.74, -20.55) * mm, "end": v(-44.85, -21.66) * mm});
            skArc(sketch, "E17.0.8.1", {"start": v(-51.2, -21.66) * mm, "mid": v(-49.3, -20.55) * mm, "end": v(-48.19, -18.66) * mm});
            skArc(sketch, "E17.0.8.2", {"start": v(-47.86, -18.66) * mm, "mid": v(-48.02, -18.65) * mm, "end": v(-48.19, -18.66) * mm});
            skArc(sketch, "E17.0.8.3", {"start": v(-51.2, -21.66) * mm, "mid": v(-51.2, -21.83) * mm, "end": v(-51.2, -22) * mm});
            skArc(sketch, "E17.0.8.4", {"start": v(-48.19, -25) * mm, "mid": v(-49.3, -23.1) * mm, "end": v(-51.2, -22) * mm});
            skArc(sketch, "E17.0.8.5", {"start": v(-44.85, -22) * mm, "mid": v(-46.74, -23.1) * mm, "end": v(-47.86, -25) * mm});
            skArc(sketch, "E17.0.8.6", {"start": v(-48.19, -25) * mm, "mid": v(-48.02, -25) * mm, "end": v(-47.86, -25) * mm});
            skArc(sketch, "E17.0.8.7", {"start": v(-44.85, -22) * mm, "mid": v(-44.85, -21.83) * mm, "end": v(-44.85, -21.66) * mm});
            skArc(sketch, "E17.0.9.0", {"start": v(-47.86, -27.39) * mm, "mid": v(-46.74, -29.28) * mm, "end": v(-44.85, -30.4) * mm});
            skArc(sketch, "E17.0.9.1", {"start": v(-51.2, -30.4) * mm, "mid": v(-49.3, -29.28) * mm, "end": v(-48.19, -27.39) * mm});
            skArc(sketch, "E17.0.9.2", {"start": v(-47.86, -27.39) * mm, "mid": v(-48.02, -27.38) * mm, "end": v(-48.19, -27.39) * mm});
            skArc(sketch, "E17.0.9.3", {"start": v(-51.2, -30.4) * mm, "mid": v(-51.2, -30.56) * mm, "end": v(-51.2, -30.73) * mm});
            skArc(sketch, "E17.0.9.4", {"start": v(-48.19, -33.73) * mm, "mid": v(-49.3, -31.84) * mm, "end": v(-51.2, -30.73) * mm});
            skArc(sketch, "E17.0.9.5", {"start": v(-44.85, -30.73) * mm, "mid": v(-46.74, -31.84) * mm, "end": v(-47.86, -33.73) * mm});
            skArc(sketch, "E17.0.9.6", {"start": v(-48.19, -33.73) * mm, "mid": v(-48.02, -33.73) * mm, "end": v(-47.86, -33.73) * mm});
            skArc(sketch, "E17.0.9.7", {"start": v(-44.85, -30.73) * mm, "mid": v(-44.85, -30.56) * mm, "end": v(-44.85, -30.4) * mm});
            skArc(sketch, "E17.0.10.0", {"start": v(-47.86, -36.12) * mm, "mid": v(-46.74, -38.01) * mm, "end": v(-44.85, -39.12) * mm});
            skArc(sketch, "E17.0.10.1", {"start": v(-51.2, -39.12) * mm, "mid": v(-49.3, -38.01) * mm, "end": v(-48.19, -36.12) * mm});
            skArc(sketch, "E17.0.10.2", {"start": v(-47.86, -36.12) * mm, "mid": v(-48.02, -36.12) * mm, "end": v(-48.19, -36.12) * mm});
            skArc(sketch, "E17.0.10.3", {"start": v(-51.2, -39.12) * mm, "mid": v(-51.2, -39.3) * mm, "end": v(-51.2, -39.46) * mm});
            skArc(sketch, "E17.0.10.4", {"start": v(-48.19, -42.46) * mm, "mid": v(-49.3, -40.57) * mm, "end": v(-51.2, -39.46) * mm});
            skArc(sketch, "E17.0.10.5", {"start": v(-44.85, -39.46) * mm, "mid": v(-46.74, -40.57) * mm, "end": v(-47.86, -42.46) * mm});
            skArc(sketch, "E17.0.10.6", {"start": v(-48.19, -42.46) * mm, "mid": v(-48.02, -42.47) * mm, "end": v(-47.86, -42.46) * mm});
            skArc(sketch, "E17.0.10.7", {"start": v(-44.85, -39.46) * mm, "mid": v(-44.85, -39.3) * mm, "end": v(-44.85, -39.12) * mm});
            skArc(sketch, "E17.0.11.0", {"start": v(-47.86, -44.85) * mm, "mid": v(-46.74, -46.74) * mm, "end": v(-44.85, -47.86) * mm});
            skArc(sketch, "E17.0.11.1", {"start": v(-51.2, -47.86) * mm, "mid": v(-49.3, -46.74) * mm, "end": v(-48.19, -44.85) * mm});
            skArc(sketch, "E17.0.11.2", {"start": v(-47.86, -44.85) * mm, "mid": v(-48.02, -44.85) * mm, "end": v(-48.19, -44.85) * mm});
            skArc(sketch, "E17.0.11.3", {"start": v(-51.2, -47.86) * mm, "mid": v(-51.2, -48.02) * mm, "end": v(-51.2, -48.19) * mm});
            skArc(sketch, "E17.0.11.4", {"start": v(-48.19, -51.2) * mm, "mid": v(-49.3, -49.3) * mm, "end": v(-51.2, -48.19) * mm});
            skArc(sketch, "E17.0.11.5", {"start": v(-44.85, -48.19) * mm, "mid": v(-46.74, -49.3) * mm, "end": v(-47.86, -51.2) * mm});
            skArc(sketch, "E17.0.11.6", {"start": v(-48.19, -51.2) * mm, "mid": v(-48.02, -51.2) * mm, "end": v(-47.86, -51.2) * mm});
            skArc(sketch, "E17.0.11.7", {"start": v(-44.85, -48.19) * mm, "mid": v(-44.85, -48.02) * mm, "end": v(-44.85, -47.86) * mm});
            skArc(sketch, "E17.1.0.0", {"start": v(-39.12, 51.2) * mm, "mid": v(-38.01, 49.3) * mm, "end": v(-36.12, 48.19) * mm});
            skArc(sketch, "E17.1.0.1", {"start": v(-42.46, 48.19) * mm, "mid": v(-40.57, 49.3) * mm, "end": v(-39.46, 51.2) * mm});
            skArc(sketch, "E17.1.0.2", {"start": v(-39.12, 51.2) * mm, "mid": v(-39.3, 51.2) * mm, "end": v(-39.46, 51.2) * mm});
            skArc(sketch, "E17.1.0.3", {"start": v(-42.46, 48.19) * mm, "mid": v(-42.47, 48.02) * mm, "end": v(-42.46, 47.86) * mm});
            skArc(sketch, "E17.1.0.4", {"start": v(-39.46, 44.85) * mm, "mid": v(-40.57, 46.74) * mm, "end": v(-42.46, 47.86) * mm});
            skArc(sketch, "E17.1.0.5", {"start": v(-36.12, 47.86) * mm, "mid": v(-38.01, 46.74) * mm, "end": v(-39.12, 44.85) * mm});
            skArc(sketch, "E17.1.0.6", {"start": v(-39.46, 44.85) * mm, "mid": v(-39.3, 44.85) * mm, "end": v(-39.12, 44.85) * mm});
            skArc(sketch, "E17.1.0.7", {"start": v(-36.12, 47.86) * mm, "mid": v(-36.12, 48.02) * mm, "end": v(-36.12, 48.19) * mm});
            skArc(sketch, "E17.1.1.0", {"start": v(-39.12, 42.46) * mm, "mid": v(-38.01, 40.57) * mm, "end": v(-36.12, 39.46) * mm});
            skArc(sketch, "E17.1.1.1", {"start": v(-42.46, 39.46) * mm, "mid": v(-40.57, 40.57) * mm, "end": v(-39.46, 42.46) * mm});
            skArc(sketch, "E17.1.1.2", {"start": v(-39.12, 42.46) * mm, "mid": v(-39.3, 42.47) * mm, "end": v(-39.46, 42.46) * mm});
            skArc(sketch, "E17.1.1.3", {"start": v(-42.46, 39.46) * mm, "mid": v(-42.47, 39.3) * mm, "end": v(-42.46, 39.12) * mm});
            skArc(sketch, "E17.1.1.4", {"start": v(-39.46, 36.12) * mm, "mid": v(-40.57, 38.01) * mm, "end": v(-42.46, 39.12) * mm});
            skArc(sketch, "E17.1.1.5", {"start": v(-36.12, 39.12) * mm, "mid": v(-38.01, 38.01) * mm, "end": v(-39.12, 36.12) * mm});
            skArc(sketch, "E17.1.1.6", {"start": v(-39.46, 36.12) * mm, "mid": v(-39.3, 36.12) * mm, "end": v(-39.12, 36.12) * mm});
            skArc(sketch, "E17.1.1.7", {"start": v(-36.12, 39.12) * mm, "mid": v(-36.12, 39.3) * mm, "end": v(-36.12, 39.46) * mm});
            skArc(sketch, "E17.1.2.0", {"start": v(-39.12, 33.73) * mm, "mid": v(-38.01, 31.84) * mm, "end": v(-36.12, 30.73) * mm});
            skArc(sketch, "E17.1.2.1", {"start": v(-42.46, 30.73) * mm, "mid": v(-40.57, 31.84) * mm, "end": v(-39.46, 33.73) * mm});
            skArc(sketch, "E17.1.2.2", {"start": v(-39.12, 33.73) * mm, "mid": v(-39.3, 33.73) * mm, "end": v(-39.46, 33.73) * mm});
            skArc(sketch, "E17.1.2.3", {"start": v(-42.46, 30.73) * mm, "mid": v(-42.47, 30.56) * mm, "end": v(-42.46, 30.4) * mm});
            skArc(sketch, "E17.1.2.4", {"start": v(-39.46, 27.39) * mm, "mid": v(-40.57, 29.28) * mm, "end": v(-42.46, 30.4) * mm});
            skArc(sketch, "E17.1.2.5", {"start": v(-36.12, 30.4) * mm, "mid": v(-38.01, 29.28) * mm, "end": v(-39.12, 27.39) * mm});
            skArc(sketch, "E17.1.2.6", {"start": v(-39.46, 27.39) * mm, "mid": v(-39.3, 27.38) * mm, "end": v(-39.12, 27.39) * mm});
            skArc(sketch, "E17.1.2.7", {"start": v(-36.12, 30.4) * mm, "mid": v(-36.12, 30.56) * mm, "end": v(-36.12, 30.73) * mm});
            skArc(sketch, "E17.1.3.0", {"start": v(-39.12, 25) * mm, "mid": v(-38.01, 23.1) * mm, "end": v(-36.12, 22) * mm});
            skArc(sketch, "E17.1.3.1", {"start": v(-42.46, 22) * mm, "mid": v(-40.57, 23.1) * mm, "end": v(-39.46, 25) * mm});
            skArc(sketch, "E17.1.3.2", {"start": v(-39.12, 25) * mm, "mid": v(-39.3, 25) * mm, "end": v(-39.46, 25) * mm});
            skArc(sketch, "E17.1.3.3", {"start": v(-42.46, 22) * mm, "mid": v(-42.47, 21.83) * mm, "end": v(-42.46, 21.66) * mm});
            skArc(sketch, "E17.1.3.4", {"start": v(-39.46, 18.66) * mm, "mid": v(-40.57, 20.55) * mm, "end": v(-42.46, 21.66) * mm});
            skArc(sketch, "E17.1.3.5", {"start": v(-36.12, 21.66) * mm, "mid": v(-38.01, 20.55) * mm, "end": v(-39.12, 18.66) * mm});
            skArc(sketch, "E17.1.3.6", {"start": v(-39.46, 18.66) * mm, "mid": v(-39.3, 18.65) * mm, "end": v(-39.12, 18.66) * mm});
            skArc(sketch, "E17.1.3.7", {"start": v(-36.12, 21.66) * mm, "mid": v(-36.12, 21.83) * mm, "end": v(-36.12, 22) * mm});
            skArc(sketch, "E17.1.4.0", {"start": v(-39.12, 16.27) * mm, "mid": v(-38.01, 14.38) * mm, "end": v(-36.12, 13.26) * mm});
            skArc(sketch, "E17.1.4.1", {"start": v(-42.46, 13.26) * mm, "mid": v(-40.57, 14.38) * mm, "end": v(-39.46, 16.27) * mm});
            skArc(sketch, "E17.1.4.2", {"start": v(-39.12, 16.27) * mm, "mid": v(-39.3, 16.27) * mm, "end": v(-39.46, 16.27) * mm});
            skArc(sketch, "E17.1.4.3", {"start": v(-42.46, 13.26) * mm, "mid": v(-42.47, 13.1) * mm, "end": v(-42.46, 12.93) * mm});
            skArc(sketch, "E17.1.4.4", {"start": v(-39.46, 9.93) * mm, "mid": v(-40.57, 11.82) * mm, "end": v(-42.46, 12.93) * mm});
            skArc(sketch, "E17.1.4.5", {"start": v(-36.12, 12.93) * mm, "mid": v(-38.01, 11.82) * mm, "end": v(-39.12, 9.93) * mm});
            skArc(sketch, "E17.1.4.6", {"start": v(-39.46, 9.93) * mm, "mid": v(-39.3, 9.92) * mm, "end": v(-39.12, 9.93) * mm});
            skArc(sketch, "E17.1.4.7", {"start": v(-36.12, 12.93) * mm, "mid": v(-36.12, 13.1) * mm, "end": v(-36.12, 13.26) * mm});
            skArc(sketch, "E17.1.5.0", {"start": v(-39.12, 7.54) * mm, "mid": v(-38.01, 5.64) * mm, "end": v(-36.12, 4.53) * mm});
            skArc(sketch, "E17.1.5.1", {"start": v(-42.46, 4.53) * mm, "mid": v(-40.57, 5.64) * mm, "end": v(-39.46, 7.54) * mm});
            skArc(sketch, "E17.1.5.2", {"start": v(-39.12, 7.54) * mm, "mid": v(-39.3, 7.54) * mm, "end": v(-39.46, 7.54) * mm});
            skArc(sketch, "E17.1.5.3", {"start": v(-42.46, 4.53) * mm, "mid": v(-42.47, 4.37) * mm, "end": v(-42.46, 4.2) * mm});
            skArc(sketch, "E17.1.5.4", {"start": v(-39.46, 1.2) * mm, "mid": v(-40.57, 3.09) * mm, "end": v(-42.46, 4.2) * mm});
            skArc(sketch, "E17.1.5.5", {"start": v(-36.12, 4.2) * mm, "mid": v(-38.01, 3.09) * mm, "end": v(-39.12, 1.2) * mm});
            skArc(sketch, "E17.1.5.6", {"start": v(-39.46, 1.2) * mm, "mid": v(-39.3, 1.2) * mm, "end": v(-39.12, 1.2) * mm});
            skArc(sketch, "E17.1.5.7", {"start": v(-36.12, 4.2) * mm, "mid": v(-36.12, 4.37) * mm, "end": v(-36.12, 4.53) * mm});
            skArc(sketch, "E17.1.6.0", {"start": v(-39.12, -1.2) * mm, "mid": v(-38.01, -3.09) * mm, "end": v(-36.12, -4.2) * mm});
            skArc(sketch, "E17.1.6.1", {"start": v(-42.46, -4.2) * mm, "mid": v(-40.57, -3.09) * mm, "end": v(-39.46, -1.2) * mm});
            skArc(sketch, "E17.1.6.2", {"start": v(-39.12, -1.2) * mm, "mid": v(-39.3, -1.2) * mm, "end": v(-39.46, -1.2) * mm});
            skArc(sketch, "E17.1.6.3", {"start": v(-42.46, -4.2) * mm, "mid": v(-42.47, -4.37) * mm, "end": v(-42.46, -4.53) * mm});
            skArc(sketch, "E17.1.6.4", {"start": v(-39.46, -7.54) * mm, "mid": v(-40.57, -5.64) * mm, "end": v(-42.46, -4.53) * mm});
            skArc(sketch, "E17.1.6.5", {"start": v(-36.12, -4.53) * mm, "mid": v(-38.01, -5.64) * mm, "end": v(-39.12, -7.54) * mm});
            skArc(sketch, "E17.1.6.6", {"start": v(-39.46, -7.54) * mm, "mid": v(-39.3, -7.54) * mm, "end": v(-39.12, -7.54) * mm});
            skArc(sketch, "E17.1.6.7", {"start": v(-36.12, -4.53) * mm, "mid": v(-36.12, -4.37) * mm, "end": v(-36.12, -4.2) * mm});
            skArc(sketch, "E17.1.7.0", {"start": v(-39.12, -9.93) * mm, "mid": v(-38.01, -11.82) * mm, "end": v(-36.12, -12.93) * mm});
            skArc(sketch, "E17.1.7.1", {"start": v(-42.46, -12.93) * mm, "mid": v(-40.57, -11.82) * mm, "end": v(-39.46, -9.93) * mm});
            skArc(sketch, "E17.1.7.2", {"start": v(-39.12, -9.93) * mm, "mid": v(-39.3, -9.92) * mm, "end": v(-39.46, -9.93) * mm});
            skArc(sketch, "E17.1.7.3", {"start": v(-42.46, -12.93) * mm, "mid": v(-42.47, -13.1) * mm, "end": v(-42.46, -13.26) * mm});
            skArc(sketch, "E17.1.7.4", {"start": v(-39.46, -16.27) * mm, "mid": v(-40.57, -14.38) * mm, "end": v(-42.46, -13.26) * mm});
            skArc(sketch, "E17.1.7.5", {"start": v(-36.12, -13.26) * mm, "mid": v(-38.01, -14.38) * mm, "end": v(-39.12, -16.27) * mm});
            skArc(sketch, "E17.1.7.6", {"start": v(-39.46, -16.27) * mm, "mid": v(-39.3, -16.27) * mm, "end": v(-39.12, -16.27) * mm});
            skArc(sketch, "E17.1.7.7", {"start": v(-36.12, -13.26) * mm, "mid": v(-36.12, -13.1) * mm, "end": v(-36.12, -12.93) * mm});
            skArc(sketch, "E17.1.8.0", {"start": v(-39.12, -18.66) * mm, "mid": v(-38.01, -20.55) * mm, "end": v(-36.12, -21.66) * mm});
            skArc(sketch, "E17.1.8.1", {"start": v(-42.46, -21.66) * mm, "mid": v(-40.57, -20.55) * mm, "end": v(-39.46, -18.66) * mm});
            skArc(sketch, "E17.1.8.2", {"start": v(-39.12, -18.66) * mm, "mid": v(-39.3, -18.65) * mm, "end": v(-39.46, -18.66) * mm});
            skArc(sketch, "E17.1.8.3", {"start": v(-42.46, -21.66) * mm, "mid": v(-42.47, -21.83) * mm, "end": v(-42.46, -22) * mm});
            skArc(sketch, "E17.1.8.4", {"start": v(-39.46, -25) * mm, "mid": v(-40.57, -23.1) * mm, "end": v(-42.46, -22) * mm});
            skArc(sketch, "E17.1.8.5", {"start": v(-36.12, -22) * mm, "mid": v(-38.01, -23.1) * mm, "end": v(-39.12, -25) * mm});
            skArc(sketch, "E17.1.8.6", {"start": v(-39.46, -25) * mm, "mid": v(-39.3, -25) * mm, "end": v(-39.12, -25) * mm});
            skArc(sketch, "E17.1.8.7", {"start": v(-36.12, -22) * mm, "mid": v(-36.12, -21.83) * mm, "end": v(-36.12, -21.66) * mm});
            skArc(sketch, "E17.1.9.0", {"start": v(-39.12, -27.39) * mm, "mid": v(-38.01, -29.28) * mm, "end": v(-36.12, -30.4) * mm});
            skArc(sketch, "E17.1.9.1", {"start": v(-42.46, -30.4) * mm, "mid": v(-40.57, -29.28) * mm, "end": v(-39.46, -27.39) * mm});
            skArc(sketch, "E17.1.9.2", {"start": v(-39.12, -27.39) * mm, "mid": v(-39.3, -27.38) * mm, "end": v(-39.46, -27.39) * mm});
            skArc(sketch, "E17.1.9.3", {"start": v(-42.46, -30.4) * mm, "mid": v(-42.47, -30.56) * mm, "end": v(-42.46, -30.73) * mm});
            skArc(sketch, "E17.1.9.4", {"start": v(-39.46, -33.73) * mm, "mid": v(-40.57, -31.84) * mm, "end": v(-42.46, -30.73) * mm});
            skArc(sketch, "E17.1.9.5", {"start": v(-36.12, -30.73) * mm, "mid": v(-38.01, -31.84) * mm, "end": v(-39.12, -33.73) * mm});
            skArc(sketch, "E17.1.9.6", {"start": v(-39.46, -33.73) * mm, "mid": v(-39.3, -33.73) * mm, "end": v(-39.12, -33.73) * mm});
            skArc(sketch, "E17.1.9.7", {"start": v(-36.12, -30.73) * mm, "mid": v(-36.12, -30.56) * mm, "end": v(-36.12, -30.4) * mm});
            skArc(sketch, "E17.1.10.0", {"start": v(-39.12, -36.12) * mm, "mid": v(-38.01, -38.01) * mm, "end": v(-36.12, -39.12) * mm});
            skArc(sketch, "E17.1.10.1", {"start": v(-42.46, -39.12) * mm, "mid": v(-40.57, -38.01) * mm, "end": v(-39.46, -36.12) * mm});
            skArc(sketch, "E17.1.10.2", {"start": v(-39.12, -36.12) * mm, "mid": v(-39.3, -36.12) * mm, "end": v(-39.46, -36.12) * mm});
            skArc(sketch, "E17.1.10.3", {"start": v(-42.46, -39.12) * mm, "mid": v(-42.47, -39.3) * mm, "end": v(-42.46, -39.46) * mm});
            skArc(sketch, "E17.1.10.4", {"start": v(-39.46, -42.46) * mm, "mid": v(-40.57, -40.57) * mm, "end": v(-42.46, -39.46) * mm});
            skArc(sketch, "E17.1.10.5", {"start": v(-36.12, -39.46) * mm, "mid": v(-38.01, -40.57) * mm, "end": v(-39.12, -42.46) * mm});
            skArc(sketch, "E17.1.10.6", {"start": v(-39.46, -42.46) * mm, "mid": v(-39.3, -42.47) * mm, "end": v(-39.12, -42.46) * mm});
            skArc(sketch, "E17.1.10.7", {"start": v(-36.12, -39.46) * mm, "mid": v(-36.12, -39.3) * mm, "end": v(-36.12, -39.12) * mm});
            skArc(sketch, "E17.1.11.0", {"start": v(-39.12, -44.85) * mm, "mid": v(-38.01, -46.74) * mm, "end": v(-36.12, -47.86) * mm});
            skArc(sketch, "E17.1.11.1", {"start": v(-42.46, -47.86) * mm, "mid": v(-40.57, -46.74) * mm, "end": v(-39.46, -44.85) * mm});
            skArc(sketch, "E17.1.11.2", {"start": v(-39.12, -44.85) * mm, "mid": v(-39.3, -44.85) * mm, "end": v(-39.46, -44.85) * mm});
            skArc(sketch, "E17.1.11.3", {"start": v(-42.46, -47.86) * mm, "mid": v(-42.47, -48.02) * mm, "end": v(-42.46, -48.19) * mm});
            skArc(sketch, "E17.1.11.4", {"start": v(-39.46, -51.2) * mm, "mid": v(-40.57, -49.3) * mm, "end": v(-42.46, -48.19) * mm});
            skArc(sketch, "E17.1.11.5", {"start": v(-36.12, -48.19) * mm, "mid": v(-38.01, -49.3) * mm, "end": v(-39.12, -51.2) * mm});
            skArc(sketch, "E17.1.11.6", {"start": v(-39.46, -51.2) * mm, "mid": v(-39.3, -51.2) * mm, "end": v(-39.12, -51.2) * mm});
            skArc(sketch, "E17.1.11.7", {"start": v(-36.12, -48.19) * mm, "mid": v(-36.12, -48.02) * mm, "end": v(-36.12, -47.86) * mm});
            skArc(sketch, "E17.2.0.0", {"start": v(-30.4, 51.2) * mm, "mid": v(-29.28, 49.3) * mm, "end": v(-27.39, 48.19) * mm});
            skArc(sketch, "E17.2.0.1", {"start": v(-33.73, 48.19) * mm, "mid": v(-31.84, 49.3) * mm, "end": v(-30.73, 51.2) * mm});
            skArc(sketch, "E17.2.0.2", {"start": v(-30.4, 51.2) * mm, "mid": v(-30.56, 51.2) * mm, "end": v(-30.73, 51.2) * mm});
            skArc(sketch, "E17.2.0.3", {"start": v(-33.73, 48.19) * mm, "mid": v(-33.73, 48.02) * mm, "end": v(-33.73, 47.86) * mm});
            skArc(sketch, "E17.2.0.4", {"start": v(-30.73, 44.85) * mm, "mid": v(-31.84, 46.74) * mm, "end": v(-33.73, 47.86) * mm});
            skArc(sketch, "E17.2.0.5", {"start": v(-27.39, 47.86) * mm, "mid": v(-29.28, 46.74) * mm, "end": v(-30.4, 44.85) * mm});
            skArc(sketch, "E17.2.0.6", {"start": v(-30.73, 44.85) * mm, "mid": v(-30.56, 44.85) * mm, "end": v(-30.4, 44.85) * mm});
            skArc(sketch, "E17.2.0.7", {"start": v(-27.39, 47.86) * mm, "mid": v(-27.38, 48.02) * mm, "end": v(-27.39, 48.19) * mm});
            skArc(sketch, "E17.2.1.0", {"start": v(-30.4, 42.46) * mm, "mid": v(-29.28, 40.57) * mm, "end": v(-27.39, 39.46) * mm});
            skArc(sketch, "E17.2.1.1", {"start": v(-33.73, 39.46) * mm, "mid": v(-31.84, 40.57) * mm, "end": v(-30.73, 42.46) * mm});
            skArc(sketch, "E17.2.1.2", {"start": v(-30.4, 42.46) * mm, "mid": v(-30.56, 42.47) * mm, "end": v(-30.73, 42.46) * mm});
            skArc(sketch, "E17.2.1.3", {"start": v(-33.73, 39.46) * mm, "mid": v(-33.73, 39.3) * mm, "end": v(-33.73, 39.12) * mm});
            skArc(sketch, "E17.2.1.4", {"start": v(-30.73, 36.12) * mm, "mid": v(-31.84, 38.01) * mm, "end": v(-33.73, 39.12) * mm});
            skArc(sketch, "E17.2.1.5", {"start": v(-27.39, 39.12) * mm, "mid": v(-29.28, 38.01) * mm, "end": v(-30.4, 36.12) * mm});
            skArc(sketch, "E17.2.1.6", {"start": v(-30.73, 36.12) * mm, "mid": v(-30.56, 36.12) * mm, "end": v(-30.4, 36.12) * mm});
            skArc(sketch, "E17.2.1.7", {"start": v(-27.39, 39.12) * mm, "mid": v(-27.38, 39.3) * mm, "end": v(-27.39, 39.46) * mm});
            skArc(sketch, "E17.2.2.0", {"start": v(-30.4, 33.73) * mm, "mid": v(-29.28, 31.84) * mm, "end": v(-27.39, 30.73) * mm});
            skArc(sketch, "E17.2.2.1", {"start": v(-33.73, 30.73) * mm, "mid": v(-31.84, 31.84) * mm, "end": v(-30.73, 33.73) * mm});
            skArc(sketch, "E17.2.2.2", {"start": v(-30.4, 33.73) * mm, "mid": v(-30.56, 33.73) * mm, "end": v(-30.73, 33.73) * mm});
            skArc(sketch, "E17.2.2.3", {"start": v(-33.73, 30.73) * mm, "mid": v(-33.73, 30.56) * mm, "end": v(-33.73, 30.4) * mm});
            skArc(sketch, "E17.2.2.4", {"start": v(-30.73, 27.39) * mm, "mid": v(-31.84, 29.28) * mm, "end": v(-33.73, 30.4) * mm});
            skArc(sketch, "E17.2.2.5", {"start": v(-27.39, 30.4) * mm, "mid": v(-29.28, 29.28) * mm, "end": v(-30.4, 27.39) * mm});
            skArc(sketch, "E17.2.2.6", {"start": v(-30.73, 27.39) * mm, "mid": v(-30.56, 27.38) * mm, "end": v(-30.4, 27.39) * mm});
            skArc(sketch, "E17.2.2.7", {"start": v(-27.39, 30.4) * mm, "mid": v(-27.38, 30.56) * mm, "end": v(-27.39, 30.73) * mm});
            skArc(sketch, "E17.2.3.0", {"start": v(-30.4, 25) * mm, "mid": v(-29.28, 23.1) * mm, "end": v(-27.39, 22) * mm});
            skArc(sketch, "E17.2.3.1", {"start": v(-33.73, 22) * mm, "mid": v(-31.84, 23.1) * mm, "end": v(-30.73, 25) * mm});
            skArc(sketch, "E17.2.3.2", {"start": v(-30.4, 25) * mm, "mid": v(-30.56, 25) * mm, "end": v(-30.73, 25) * mm});
            skArc(sketch, "E17.2.3.3", {"start": v(-33.73, 22) * mm, "mid": v(-33.73, 21.83) * mm, "end": v(-33.73, 21.66) * mm});
            skArc(sketch, "E17.2.3.4", {"start": v(-30.73, 18.66) * mm, "mid": v(-31.84, 20.55) * mm, "end": v(-33.73, 21.66) * mm});
            skArc(sketch, "E17.2.3.5", {"start": v(-27.39, 21.66) * mm, "mid": v(-29.28, 20.55) * mm, "end": v(-30.4, 18.66) * mm});
            skArc(sketch, "E17.2.3.6", {"start": v(-30.73, 18.66) * mm, "mid": v(-30.56, 18.65) * mm, "end": v(-30.4, 18.66) * mm});
            skArc(sketch, "E17.2.3.7", {"start": v(-27.39, 21.66) * mm, "mid": v(-27.38, 21.83) * mm, "end": v(-27.39, 22) * mm});
            skArc(sketch, "E17.2.4.0", {"start": v(-30.4, 16.27) * mm, "mid": v(-29.28, 14.38) * mm, "end": v(-27.39, 13.26) * mm});
            skArc(sketch, "E17.2.4.1", {"start": v(-33.73, 13.26) * mm, "mid": v(-31.84, 14.38) * mm, "end": v(-30.73, 16.27) * mm});
            skArc(sketch, "E17.2.4.2", {"start": v(-30.4, 16.27) * mm, "mid": v(-30.56, 16.27) * mm, "end": v(-30.73, 16.27) * mm});
            skArc(sketch, "E17.2.4.3", {"start": v(-33.73, 13.26) * mm, "mid": v(-33.73, 13.1) * mm, "end": v(-33.73, 12.93) * mm});
            skArc(sketch, "E17.2.4.4", {"start": v(-30.73, 9.93) * mm, "mid": v(-31.84, 11.82) * mm, "end": v(-33.73, 12.93) * mm});
            skArc(sketch, "E17.2.4.5", {"start": v(-27.39, 12.93) * mm, "mid": v(-29.28, 11.82) * mm, "end": v(-30.4, 9.93) * mm});
            skArc(sketch, "E17.2.4.6", {"start": v(-30.73, 9.93) * mm, "mid": v(-30.56, 9.92) * mm, "end": v(-30.4, 9.93) * mm});
            skArc(sketch, "E17.2.4.7", {"start": v(-27.39, 12.93) * mm, "mid": v(-27.38, 13.1) * mm, "end": v(-27.39, 13.26) * mm});
            skArc(sketch, "E17.2.5.0", {"start": v(-30.4, 7.54) * mm, "mid": v(-29.28, 5.64) * mm, "end": v(-27.39, 4.53) * mm});
            skArc(sketch, "E17.2.5.1", {"start": v(-33.73, 4.53) * mm, "mid": v(-31.84, 5.64) * mm, "end": v(-30.73, 7.54) * mm});
            skArc(sketch, "E17.2.5.2", {"start": v(-30.4, 7.54) * mm, "mid": v(-30.56, 7.54) * mm, "end": v(-30.73, 7.54) * mm});
            skArc(sketch, "E17.2.5.3", {"start": v(-33.73, 4.53) * mm, "mid": v(-33.73, 4.37) * mm, "end": v(-33.73, 4.2) * mm});
            skArc(sketch, "E17.2.5.4", {"start": v(-30.73, 1.2) * mm, "mid": v(-31.84, 3.09) * mm, "end": v(-33.73, 4.2) * mm});
            skArc(sketch, "E17.2.5.5", {"start": v(-27.39, 4.2) * mm, "mid": v(-29.28, 3.09) * mm, "end": v(-30.4, 1.2) * mm});
            skArc(sketch, "E17.2.5.6", {"start": v(-30.73, 1.2) * mm, "mid": v(-30.56, 1.2) * mm, "end": v(-30.4, 1.2) * mm});
            skArc(sketch, "E17.2.5.7", {"start": v(-27.39, 4.2) * mm, "mid": v(-27.38, 4.37) * mm, "end": v(-27.39, 4.53) * mm});
            skArc(sketch, "E17.2.6.0", {"start": v(-30.4, -1.2) * mm, "mid": v(-29.28, -3.09) * mm, "end": v(-27.39, -4.2) * mm});
            skArc(sketch, "E17.2.6.1", {"start": v(-33.73, -4.2) * mm, "mid": v(-31.84, -3.09) * mm, "end": v(-30.73, -1.2) * mm});
            skArc(sketch, "E17.2.6.2", {"start": v(-30.4, -1.2) * mm, "mid": v(-30.56, -1.2) * mm, "end": v(-30.73, -1.2) * mm});
            skArc(sketch, "E17.2.6.3", {"start": v(-33.73, -4.2) * mm, "mid": v(-33.73, -4.37) * mm, "end": v(-33.73, -4.53) * mm});
            skArc(sketch, "E17.2.6.4", {"start": v(-30.73, -7.54) * mm, "mid": v(-31.84, -5.64) * mm, "end": v(-33.73, -4.53) * mm});
            skArc(sketch, "E17.2.6.5", {"start": v(-27.39, -4.53) * mm, "mid": v(-29.28, -5.64) * mm, "end": v(-30.4, -7.54) * mm});
            skArc(sketch, "E17.2.6.6", {"start": v(-30.73, -7.54) * mm, "mid": v(-30.56, -7.54) * mm, "end": v(-30.4, -7.54) * mm});
            skArc(sketch, "E17.2.6.7", {"start": v(-27.39, -4.53) * mm, "mid": v(-27.38, -4.37) * mm, "end": v(-27.39, -4.2) * mm});
            skArc(sketch, "E17.2.7.0", {"start": v(-30.4, -9.93) * mm, "mid": v(-29.28, -11.82) * mm, "end": v(-27.39, -12.93) * mm});
            skArc(sketch, "E17.2.7.1", {"start": v(-33.73, -12.93) * mm, "mid": v(-31.84, -11.82) * mm, "end": v(-30.73, -9.93) * mm});
            skArc(sketch, "E17.2.7.2", {"start": v(-30.4, -9.93) * mm, "mid": v(-30.56, -9.92) * mm, "end": v(-30.73, -9.93) * mm});
            skArc(sketch, "E17.2.7.3", {"start": v(-33.73, -12.93) * mm, "mid": v(-33.73, -13.1) * mm, "end": v(-33.73, -13.26) * mm});
            skArc(sketch, "E17.2.7.4", {"start": v(-30.73, -16.27) * mm, "mid": v(-31.84, -14.38) * mm, "end": v(-33.73, -13.26) * mm});
            skArc(sketch, "E17.2.7.5", {"start": v(-27.39, -13.26) * mm, "mid": v(-29.28, -14.38) * mm, "end": v(-30.4, -16.27) * mm});
            skArc(sketch, "E17.2.7.6", {"start": v(-30.73, -16.27) * mm, "mid": v(-30.56, -16.27) * mm, "end": v(-30.4, -16.27) * mm});
            skArc(sketch, "E17.2.7.7", {"start": v(-27.39, -13.26) * mm, "mid": v(-27.38, -13.1) * mm, "end": v(-27.39, -12.93) * mm});
            skArc(sketch, "E17.2.8.0", {"start": v(-30.4, -18.66) * mm, "mid": v(-29.28, -20.55) * mm, "end": v(-27.39, -21.66) * mm});
            skArc(sketch, "E17.2.8.1", {"start": v(-33.73, -21.66) * mm, "mid": v(-31.84, -20.55) * mm, "end": v(-30.73, -18.66) * mm});
            skArc(sketch, "E17.2.8.2", {"start": v(-30.4, -18.66) * mm, "mid": v(-30.56, -18.65) * mm, "end": v(-30.73, -18.66) * mm});
            skArc(sketch, "E17.2.8.3", {"start": v(-33.73, -21.66) * mm, "mid": v(-33.73, -21.83) * mm, "end": v(-33.73, -22) * mm});
            skArc(sketch, "E17.2.8.4", {"start": v(-30.73, -25) * mm, "mid": v(-31.84, -23.1) * mm, "end": v(-33.73, -22) * mm});
            skArc(sketch, "E17.2.8.5", {"start": v(-27.39, -22) * mm, "mid": v(-29.28, -23.1) * mm, "end": v(-30.4, -25) * mm});
            skArc(sketch, "E17.2.8.6", {"start": v(-30.73, -25) * mm, "mid": v(-30.56, -25) * mm, "end": v(-30.4, -25) * mm});
            skArc(sketch, "E17.2.8.7", {"start": v(-27.39, -22) * mm, "mid": v(-27.38, -21.83) * mm, "end": v(-27.39, -21.66) * mm});
            skArc(sketch, "E17.2.9.0", {"start": v(-30.4, -27.39) * mm, "mid": v(-29.28, -29.28) * mm, "end": v(-27.39, -30.4) * mm});
            skArc(sketch, "E17.2.9.1", {"start": v(-33.73, -30.4) * mm, "mid": v(-31.84, -29.28) * mm, "end": v(-30.73, -27.39) * mm});
            skArc(sketch, "E17.2.9.2", {"start": v(-30.4, -27.39) * mm, "mid": v(-30.56, -27.38) * mm, "end": v(-30.73, -27.39) * mm});
            skArc(sketch, "E17.2.9.3", {"start": v(-33.73, -30.4) * mm, "mid": v(-33.73, -30.56) * mm, "end": v(-33.73, -30.73) * mm});
            skArc(sketch, "E17.2.9.4", {"start": v(-30.73, -33.73) * mm, "mid": v(-31.84, -31.84) * mm, "end": v(-33.73, -30.73) * mm});
            skArc(sketch, "E17.2.9.5", {"start": v(-27.39, -30.73) * mm, "mid": v(-29.28, -31.84) * mm, "end": v(-30.4, -33.73) * mm});
            skArc(sketch, "E17.2.9.6", {"start": v(-30.73, -33.73) * mm, "mid": v(-30.56, -33.73) * mm, "end": v(-30.4, -33.73) * mm});
            skArc(sketch, "E17.2.9.7", {"start": v(-27.39, -30.73) * mm, "mid": v(-27.38, -30.56) * mm, "end": v(-27.39, -30.4) * mm});
            skArc(sketch, "E17.2.10.0", {"start": v(-30.4, -36.12) * mm, "mid": v(-29.28, -38.01) * mm, "end": v(-27.39, -39.12) * mm});
            skArc(sketch, "E17.2.10.1", {"start": v(-33.73, -39.12) * mm, "mid": v(-31.84, -38.01) * mm, "end": v(-30.73, -36.12) * mm});
            skArc(sketch, "E17.2.10.2", {"start": v(-30.4, -36.12) * mm, "mid": v(-30.56, -36.12) * mm, "end": v(-30.73, -36.12) * mm});
            skArc(sketch, "E17.2.10.3", {"start": v(-33.73, -39.12) * mm, "mid": v(-33.73, -39.3) * mm, "end": v(-33.73, -39.46) * mm});
            skArc(sketch, "E17.2.10.4", {"start": v(-30.73, -42.46) * mm, "mid": v(-31.84, -40.57) * mm, "end": v(-33.73, -39.46) * mm});
            skArc(sketch, "E17.2.10.5", {"start": v(-27.39, -39.46) * mm, "mid": v(-29.28, -40.57) * mm, "end": v(-30.4, -42.46) * mm});
            skArc(sketch, "E17.2.10.6", {"start": v(-30.73, -42.46) * mm, "mid": v(-30.56, -42.47) * mm, "end": v(-30.4, -42.46) * mm});
            skArc(sketch, "E17.2.10.7", {"start": v(-27.39, -39.46) * mm, "mid": v(-27.38, -39.3) * mm, "end": v(-27.39, -39.12) * mm});
            skArc(sketch, "E17.2.11.0", {"start": v(-30.4, -44.85) * mm, "mid": v(-29.28, -46.74) * mm, "end": v(-27.39, -47.86) * mm});
            skArc(sketch, "E17.2.11.1", {"start": v(-33.73, -47.86) * mm, "mid": v(-31.84, -46.74) * mm, "end": v(-30.73, -44.85) * mm});
            skArc(sketch, "E17.2.11.2", {"start": v(-30.4, -44.85) * mm, "mid": v(-30.56, -44.85) * mm, "end": v(-30.73, -44.85) * mm});
            skArc(sketch, "E17.2.11.3", {"start": v(-33.73, -47.86) * mm, "mid": v(-33.73, -48.02) * mm, "end": v(-33.73, -48.19) * mm});
            skArc(sketch, "E17.2.11.4", {"start": v(-30.73, -51.2) * mm, "mid": v(-31.84, -49.3) * mm, "end": v(-33.73, -48.19) * mm});
            skArc(sketch, "E17.2.11.5", {"start": v(-27.39, -48.19) * mm, "mid": v(-29.28, -49.3) * mm, "end": v(-30.4, -51.2) * mm});
            skArc(sketch, "E17.2.11.6", {"start": v(-30.73, -51.2) * mm, "mid": v(-30.56, -51.2) * mm, "end": v(-30.4, -51.2) * mm});
            skArc(sketch, "E17.2.11.7", {"start": v(-27.39, -48.19) * mm, "mid": v(-27.38, -48.02) * mm, "end": v(-27.39, -47.86) * mm});
            skArc(sketch, "E17.3.0.0", {"start": v(-21.66, 51.2) * mm, "mid": v(-20.55, 49.3) * mm, "end": v(-18.66, 48.19) * mm});
            skArc(sketch, "E17.3.0.1", {"start": v(-25, 48.19) * mm, "mid": v(-23.1, 49.3) * mm, "end": v(-22, 51.2) * mm});
            skArc(sketch, "E17.3.0.2", {"start": v(-21.66, 51.2) * mm, "mid": v(-21.83, 51.2) * mm, "end": v(-22, 51.2) * mm});
            skArc(sketch, "E17.3.0.3", {"start": v(-25, 48.19) * mm, "mid": v(-25, 48.02) * mm, "end": v(-25, 47.86) * mm});
            skArc(sketch, "E17.3.0.4", {"start": v(-22, 44.85) * mm, "mid": v(-23.1, 46.74) * mm, "end": v(-25, 47.86) * mm});
            skArc(sketch, "E17.3.0.5", {"start": v(-18.66, 47.86) * mm, "mid": v(-20.55, 46.74) * mm, "end": v(-21.66, 44.85) * mm});
            skArc(sketch, "E17.3.0.6", {"start": v(-22, 44.85) * mm, "mid": v(-21.83, 44.85) * mm, "end": v(-21.66, 44.85) * mm});
            skArc(sketch, "E17.3.0.7", {"start": v(-18.66, 47.86) * mm, "mid": v(-18.65, 48.02) * mm, "end": v(-18.66, 48.19) * mm});
            skArc(sketch, "E17.3.1.0", {"start": v(-21.66, 42.46) * mm, "mid": v(-20.55, 40.57) * mm, "end": v(-18.66, 39.46) * mm});
            skArc(sketch, "E17.3.1.1", {"start": v(-25, 39.46) * mm, "mid": v(-23.1, 40.57) * mm, "end": v(-22, 42.46) * mm});
            skArc(sketch, "E17.3.1.2", {"start": v(-21.66, 42.46) * mm, "mid": v(-21.83, 42.47) * mm, "end": v(-22, 42.46) * mm});
            skArc(sketch, "E17.3.1.3", {"start": v(-25, 39.46) * mm, "mid": v(-25, 39.3) * mm, "end": v(-25, 39.12) * mm});
            skArc(sketch, "E17.3.1.4", {"start": v(-22, 36.12) * mm, "mid": v(-23.1, 38.01) * mm, "end": v(-25, 39.12) * mm});
            skArc(sketch, "E17.3.1.5", {"start": v(-18.66, 39.12) * mm, "mid": v(-20.55, 38.01) * mm, "end": v(-21.66, 36.12) * mm});
            skArc(sketch, "E17.3.1.6", {"start": v(-22, 36.12) * mm, "mid": v(-21.83, 36.12) * mm, "end": v(-21.66, 36.12) * mm});
            skArc(sketch, "E17.3.1.7", {"start": v(-18.66, 39.12) * mm, "mid": v(-18.65, 39.3) * mm, "end": v(-18.66, 39.46) * mm});
            skArc(sketch, "E17.3.2.0", {"start": v(-21.66, 33.73) * mm, "mid": v(-20.55, 31.84) * mm, "end": v(-18.66, 30.73) * mm});
            skArc(sketch, "E17.3.2.1", {"start": v(-25, 30.73) * mm, "mid": v(-23.1, 31.84) * mm, "end": v(-22, 33.73) * mm});
            skArc(sketch, "E17.3.2.2", {"start": v(-21.66, 33.73) * mm, "mid": v(-21.83, 33.73) * mm, "end": v(-22, 33.73) * mm});
            skArc(sketch, "E17.3.2.3", {"start": v(-25, 30.73) * mm, "mid": v(-25, 30.56) * mm, "end": v(-25, 30.4) * mm});
            skArc(sketch, "E17.3.2.4", {"start": v(-22, 27.39) * mm, "mid": v(-23.1, 29.28) * mm, "end": v(-25, 30.4) * mm});
            skArc(sketch, "E17.3.2.5", {"start": v(-18.66, 30.4) * mm, "mid": v(-20.55, 29.28) * mm, "end": v(-21.66, 27.39) * mm});
            skArc(sketch, "E17.3.2.6", {"start": v(-22, 27.39) * mm, "mid": v(-21.83, 27.38) * mm, "end": v(-21.66, 27.39) * mm});
            skArc(sketch, "E17.3.2.7", {"start": v(-18.66, 30.4) * mm, "mid": v(-18.65, 30.56) * mm, "end": v(-18.66, 30.73) * mm});
            skArc(sketch, "E17.3.3.0", {"start": v(-21.66, 25) * mm, "mid": v(-20.55, 23.1) * mm, "end": v(-18.66, 22) * mm});
            skArc(sketch, "E17.3.3.1", {"start": v(-25, 22) * mm, "mid": v(-23.1, 23.1) * mm, "end": v(-22, 25) * mm});
            skArc(sketch, "E17.3.3.2", {"start": v(-21.66, 25) * mm, "mid": v(-21.83, 25) * mm, "end": v(-22, 25) * mm});
            skArc(sketch, "E17.3.3.3", {"start": v(-25, 22) * mm, "mid": v(-25, 21.83) * mm, "end": v(-25, 21.66) * mm});
            skArc(sketch, "E17.3.3.4", {"start": v(-22, 18.66) * mm, "mid": v(-23.1, 20.55) * mm, "end": v(-25, 21.66) * mm});
            skArc(sketch, "E17.3.3.5", {"start": v(-18.66, 21.66) * mm, "mid": v(-20.55, 20.55) * mm, "end": v(-21.66, 18.66) * mm});
            skArc(sketch, "E17.3.3.6", {"start": v(-22, 18.66) * mm, "mid": v(-21.83, 18.65) * mm, "end": v(-21.66, 18.66) * mm});
            skArc(sketch, "E17.3.3.7", {"start": v(-18.66, 21.66) * mm, "mid": v(-18.65, 21.83) * mm, "end": v(-18.66, 22) * mm});
            skArc(sketch, "E17.3.4.0", {"start": v(-21.66, 16.27) * mm, "mid": v(-20.55, 14.38) * mm, "end": v(-18.66, 13.26) * mm});
            skArc(sketch, "E17.3.4.1", {"start": v(-25, 13.26) * mm, "mid": v(-23.1, 14.38) * mm, "end": v(-22, 16.27) * mm});
            skArc(sketch, "E17.3.4.2", {"start": v(-21.66, 16.27) * mm, "mid": v(-21.83, 16.27) * mm, "end": v(-22, 16.27) * mm});
            skArc(sketch, "E17.3.4.3", {"start": v(-25, 13.26) * mm, "mid": v(-25, 13.1) * mm, "end": v(-25, 12.93) * mm});
            skArc(sketch, "E17.3.4.4", {"start": v(-22, 9.93) * mm, "mid": v(-23.1, 11.82) * mm, "end": v(-25, 12.93) * mm});
            skArc(sketch, "E17.3.4.5", {"start": v(-18.66, 12.93) * mm, "mid": v(-20.55, 11.82) * mm, "end": v(-21.66, 9.93) * mm});
            skArc(sketch, "E17.3.4.6", {"start": v(-22, 9.93) * mm, "mid": v(-21.83, 9.92) * mm, "end": v(-21.66, 9.93) * mm});
            skArc(sketch, "E17.3.4.7", {"start": v(-18.66, 12.93) * mm, "mid": v(-18.65, 13.1) * mm, "end": v(-18.66, 13.26) * mm});
            skArc(sketch, "E17.3.5.0", {"start": v(-21.66, 7.54) * mm, "mid": v(-20.55, 5.64) * mm, "end": v(-18.66, 4.53) * mm});
            skArc(sketch, "E17.3.5.1", {"start": v(-25, 4.53) * mm, "mid": v(-23.1, 5.64) * mm, "end": v(-22, 7.54) * mm});
            skArc(sketch, "E17.3.5.2", {"start": v(-21.66, 7.54) * mm, "mid": v(-21.83, 7.54) * mm, "end": v(-22, 7.54) * mm});
            skArc(sketch, "E17.3.5.3", {"start": v(-25, 4.53) * mm, "mid": v(-25, 4.37) * mm, "end": v(-25, 4.2) * mm});
            skArc(sketch, "E17.3.5.4", {"start": v(-22, 1.2) * mm, "mid": v(-23.1, 3.09) * mm, "end": v(-25, 4.2) * mm});
            skArc(sketch, "E17.3.5.5", {"start": v(-18.66, 4.2) * mm, "mid": v(-20.55, 3.09) * mm, "end": v(-21.66, 1.2) * mm});
            skArc(sketch, "E17.3.5.6", {"start": v(-22, 1.2) * mm, "mid": v(-21.83, 1.2) * mm, "end": v(-21.66, 1.2) * mm});
            skArc(sketch, "E17.3.5.7", {"start": v(-18.66, 4.2) * mm, "mid": v(-18.65, 4.37) * mm, "end": v(-18.66, 4.53) * mm});
            skArc(sketch, "E17.3.6.0", {"start": v(-21.66, -1.2) * mm, "mid": v(-20.55, -3.09) * mm, "end": v(-18.66, -4.2) * mm});
            skArc(sketch, "E17.3.6.1", {"start": v(-25, -4.2) * mm, "mid": v(-23.1, -3.09) * mm, "end": v(-22, -1.2) * mm});
            skArc(sketch, "E17.3.6.2", {"start": v(-21.66, -1.2) * mm, "mid": v(-21.83, -1.2) * mm, "end": v(-22, -1.2) * mm});
            skArc(sketch, "E17.3.6.3", {"start": v(-25, -4.2) * mm, "mid": v(-25, -4.37) * mm, "end": v(-25, -4.53) * mm});
            skArc(sketch, "E17.3.6.4", {"start": v(-22, -7.54) * mm, "mid": v(-23.1, -5.64) * mm, "end": v(-25, -4.53) * mm});
            skArc(sketch, "E17.3.6.5", {"start": v(-18.66, -4.53) * mm, "mid": v(-20.55, -5.64) * mm, "end": v(-21.66, -7.54) * mm});
            skArc(sketch, "E17.3.6.6", {"start": v(-22, -7.54) * mm, "mid": v(-21.83, -7.54) * mm, "end": v(-21.66, -7.54) * mm});
            skArc(sketch, "E17.3.6.7", {"start": v(-18.66, -4.53) * mm, "mid": v(-18.65, -4.37) * mm, "end": v(-18.66, -4.2) * mm});
            skArc(sketch, "E17.3.7.0", {"start": v(-21.66, -9.93) * mm, "mid": v(-20.55, -11.82) * mm, "end": v(-18.66, -12.93) * mm});
            skArc(sketch, "E17.3.7.1", {"start": v(-25, -12.93) * mm, "mid": v(-23.1, -11.82) * mm, "end": v(-22, -9.93) * mm});
            skArc(sketch, "E17.3.7.2", {"start": v(-21.66, -9.93) * mm, "mid": v(-21.83, -9.92) * mm, "end": v(-22, -9.93) * mm});
            skArc(sketch, "E17.3.7.3", {"start": v(-25, -12.93) * mm, "mid": v(-25, -13.1) * mm, "end": v(-25, -13.26) * mm});
            skArc(sketch, "E17.3.7.4", {"start": v(-22, -16.27) * mm, "mid": v(-23.1, -14.38) * mm, "end": v(-25, -13.26) * mm});
            skArc(sketch, "E17.3.7.5", {"start": v(-18.66, -13.26) * mm, "mid": v(-20.55, -14.38) * mm, "end": v(-21.66, -16.27) * mm});
            skArc(sketch, "E17.3.7.6", {"start": v(-22, -16.27) * mm, "mid": v(-21.83, -16.27) * mm, "end": v(-21.66, -16.27) * mm});
            skArc(sketch, "E17.3.7.7", {"start": v(-18.66, -13.26) * mm, "mid": v(-18.65, -13.1) * mm, "end": v(-18.66, -12.93) * mm});
            skArc(sketch, "E17.3.8.0", {"start": v(-21.66, -18.66) * mm, "mid": v(-20.55, -20.55) * mm, "end": v(-18.66, -21.66) * mm});
            skArc(sketch, "E17.3.8.1", {"start": v(-25, -21.66) * mm, "mid": v(-23.1, -20.55) * mm, "end": v(-22, -18.66) * mm});
            skArc(sketch, "E17.3.8.2", {"start": v(-21.66, -18.66) * mm, "mid": v(-21.83, -18.65) * mm, "end": v(-22, -18.66) * mm});
            skArc(sketch, "E17.3.8.3", {"start": v(-25, -21.66) * mm, "mid": v(-25, -21.83) * mm, "end": v(-25, -22) * mm});
            skArc(sketch, "E17.3.8.4", {"start": v(-22, -25) * mm, "mid": v(-23.1, -23.1) * mm, "end": v(-25, -22) * mm});
            skArc(sketch, "E17.3.8.5", {"start": v(-18.66, -22) * mm, "mid": v(-20.55, -23.1) * mm, "end": v(-21.66, -25) * mm});
            skArc(sketch, "E17.3.8.6", {"start": v(-22, -25) * mm, "mid": v(-21.83, -25) * mm, "end": v(-21.66, -25) * mm});
            skArc(sketch, "E17.3.8.7", {"start": v(-18.66, -22) * mm, "mid": v(-18.65, -21.83) * mm, "end": v(-18.66, -21.66) * mm});
            skArc(sketch, "E17.3.9.0", {"start": v(-21.66, -27.39) * mm, "mid": v(-20.55, -29.28) * mm, "end": v(-18.66, -30.4) * mm});
            skArc(sketch, "E17.3.9.1", {"start": v(-25, -30.4) * mm, "mid": v(-23.1, -29.28) * mm, "end": v(-22, -27.39) * mm});
            skArc(sketch, "E17.3.9.2", {"start": v(-21.66, -27.39) * mm, "mid": v(-21.83, -27.38) * mm, "end": v(-22, -27.39) * mm});
            skArc(sketch, "E17.3.9.3", {"start": v(-25, -30.4) * mm, "mid": v(-25, -30.56) * mm, "end": v(-25, -30.73) * mm});
            skArc(sketch, "E17.3.9.4", {"start": v(-22, -33.73) * mm, "mid": v(-23.1, -31.84) * mm, "end": v(-25, -30.73) * mm});
            skArc(sketch, "E17.3.9.5", {"start": v(-18.66, -30.73) * mm, "mid": v(-20.55, -31.84) * mm, "end": v(-21.66, -33.73) * mm});
            skArc(sketch, "E17.3.9.6", {"start": v(-22, -33.73) * mm, "mid": v(-21.83, -33.73) * mm, "end": v(-21.66, -33.73) * mm});
            skArc(sketch, "E17.3.9.7", {"start": v(-18.66, -30.73) * mm, "mid": v(-18.65, -30.56) * mm, "end": v(-18.66, -30.4) * mm});
            skArc(sketch, "E17.3.10.0", {"start": v(-21.66, -36.12) * mm, "mid": v(-20.55, -38.01) * mm, "end": v(-18.66, -39.12) * mm});
            skArc(sketch, "E17.3.10.1", {"start": v(-25, -39.12) * mm, "mid": v(-23.1, -38.01) * mm, "end": v(-22, -36.12) * mm});
            skArc(sketch, "E17.3.10.2", {"start": v(-21.66, -36.12) * mm, "mid": v(-21.83, -36.12) * mm, "end": v(-22, -36.12) * mm});
            skArc(sketch, "E17.3.10.3", {"start": v(-25, -39.12) * mm, "mid": v(-25, -39.3) * mm, "end": v(-25, -39.46) * mm});
            skArc(sketch, "E17.3.10.4", {"start": v(-22, -42.46) * mm, "mid": v(-23.1, -40.57) * mm, "end": v(-25, -39.46) * mm});
            skArc(sketch, "E17.3.10.5", {"start": v(-18.66, -39.46) * mm, "mid": v(-20.55, -40.57) * mm, "end": v(-21.66, -42.46) * mm});
            skArc(sketch, "E17.3.10.6", {"start": v(-22, -42.46) * mm, "mid": v(-21.83, -42.47) * mm, "end": v(-21.66, -42.46) * mm});
            skArc(sketch, "E17.3.10.7", {"start": v(-18.66, -39.46) * mm, "mid": v(-18.65, -39.3) * mm, "end": v(-18.66, -39.12) * mm});
            skArc(sketch, "E17.3.11.0", {"start": v(-21.66, -44.85) * mm, "mid": v(-20.55, -46.74) * mm, "end": v(-18.66, -47.86) * mm});
            skArc(sketch, "E17.3.11.1", {"start": v(-25, -47.86) * mm, "mid": v(-23.1, -46.74) * mm, "end": v(-22, -44.85) * mm});
            skArc(sketch, "E17.3.11.2", {"start": v(-21.66, -44.85) * mm, "mid": v(-21.83, -44.85) * mm, "end": v(-22, -44.85) * mm});
            skArc(sketch, "E17.3.11.3", {"start": v(-25, -47.86) * mm, "mid": v(-25, -48.02) * mm, "end": v(-25, -48.19) * mm});
            skArc(sketch, "E17.3.11.4", {"start": v(-22, -51.2) * mm, "mid": v(-23.1, -49.3) * mm, "end": v(-25, -48.19) * mm});
            skArc(sketch, "E17.3.11.5", {"start": v(-18.66, -48.19) * mm, "mid": v(-20.55, -49.3) * mm, "end": v(-21.66, -51.2) * mm});
            skArc(sketch, "E17.3.11.6", {"start": v(-22, -51.2) * mm, "mid": v(-21.83, -51.2) * mm, "end": v(-21.66, -51.2) * mm});
            skArc(sketch, "E17.3.11.7", {"start": v(-18.66, -48.19) * mm, "mid": v(-18.65, -48.02) * mm, "end": v(-18.66, -47.86) * mm});
            skArc(sketch, "E17.4.0.0", {"start": v(-12.93, 51.2) * mm, "mid": v(-11.82, 49.3) * mm, "end": v(-9.93, 48.19) * mm});
            skArc(sketch, "E17.4.0.1", {"start": v(-16.27, 48.19) * mm, "mid": v(-14.38, 49.3) * mm, "end": v(-13.26, 51.2) * mm});
            skArc(sketch, "E17.4.0.2", {"start": v(-12.93, 51.2) * mm, "mid": v(-13.1, 51.2) * mm, "end": v(-13.26, 51.2) * mm});
            skArc(sketch, "E17.4.0.3", {"start": v(-16.27, 48.19) * mm, "mid": v(-16.27, 48.02) * mm, "end": v(-16.27, 47.86) * mm});
            skArc(sketch, "E17.4.0.4", {"start": v(-13.26, 44.85) * mm, "mid": v(-14.38, 46.74) * mm, "end": v(-16.27, 47.86) * mm});
            skArc(sketch, "E17.4.0.5", {"start": v(-9.93, 47.86) * mm, "mid": v(-11.82, 46.74) * mm, "end": v(-12.93, 44.85) * mm});
            skArc(sketch, "E17.4.0.6", {"start": v(-13.26, 44.85) * mm, "mid": v(-13.1, 44.85) * mm, "end": v(-12.93, 44.85) * mm});
            skArc(sketch, "E17.4.0.7", {"start": v(-9.93, 47.86) * mm, "mid": v(-9.92, 48.02) * mm, "end": v(-9.93, 48.19) * mm});
            skArc(sketch, "E17.4.1.0", {"start": v(-12.93, 42.46) * mm, "mid": v(-11.82, 40.57) * mm, "end": v(-9.93, 39.46) * mm});
            skArc(sketch, "E17.4.1.1", {"start": v(-16.27, 39.46) * mm, "mid": v(-14.38, 40.57) * mm, "end": v(-13.26, 42.46) * mm});
            skArc(sketch, "E17.4.1.2", {"start": v(-12.93, 42.46) * mm, "mid": v(-13.1, 42.47) * mm, "end": v(-13.26, 42.46) * mm});
            skArc(sketch, "E17.4.1.3", {"start": v(-16.27, 39.46) * mm, "mid": v(-16.27, 39.3) * mm, "end": v(-16.27, 39.12) * mm});
            skArc(sketch, "E17.4.1.4", {"start": v(-13.26, 36.12) * mm, "mid": v(-14.38, 38.01) * mm, "end": v(-16.27, 39.12) * mm});
            skArc(sketch, "E17.4.1.5", {"start": v(-9.93, 39.12) * mm, "mid": v(-11.82, 38.01) * mm, "end": v(-12.93, 36.12) * mm});
            skArc(sketch, "E17.4.1.6", {"start": v(-13.26, 36.12) * mm, "mid": v(-13.1, 36.12) * mm, "end": v(-12.93, 36.12) * mm});
            skArc(sketch, "E17.4.1.7", {"start": v(-9.93, 39.12) * mm, "mid": v(-9.92, 39.3) * mm, "end": v(-9.93, 39.46) * mm});
            skArc(sketch, "E17.4.2.0", {"start": v(-12.93, 33.73) * mm, "mid": v(-11.82, 31.84) * mm, "end": v(-9.93, 30.73) * mm});
            skArc(sketch, "E17.4.2.1", {"start": v(-16.27, 30.73) * mm, "mid": v(-14.38, 31.84) * mm, "end": v(-13.26, 33.73) * mm});
            skArc(sketch, "E17.4.2.2", {"start": v(-12.93, 33.73) * mm, "mid": v(-13.1, 33.73) * mm, "end": v(-13.26, 33.73) * mm});
            skArc(sketch, "E17.4.2.3", {"start": v(-16.27, 30.73) * mm, "mid": v(-16.27, 30.56) * mm, "end": v(-16.27, 30.4) * mm});
            skArc(sketch, "E17.4.2.4", {"start": v(-13.26, 27.39) * mm, "mid": v(-14.38, 29.28) * mm, "end": v(-16.27, 30.4) * mm});
            skArc(sketch, "E17.4.2.5", {"start": v(-9.93, 30.4) * mm, "mid": v(-11.82, 29.28) * mm, "end": v(-12.93, 27.39) * mm});
            skArc(sketch, "E17.4.2.6", {"start": v(-13.26, 27.39) * mm, "mid": v(-13.1, 27.38) * mm, "end": v(-12.93, 27.39) * mm});
            skArc(sketch, "E17.4.2.7", {"start": v(-9.93, 30.4) * mm, "mid": v(-9.92, 30.56) * mm, "end": v(-9.93, 30.73) * mm});
            skArc(sketch, "E17.4.3.0", {"start": v(-12.93, 25) * mm, "mid": v(-11.82, 23.1) * mm, "end": v(-9.93, 22) * mm});
            skArc(sketch, "E17.4.3.1", {"start": v(-16.27, 22) * mm, "mid": v(-14.38, 23.1) * mm, "end": v(-13.26, 25) * mm});
            skArc(sketch, "E17.4.3.2", {"start": v(-12.93, 25) * mm, "mid": v(-13.1, 25) * mm, "end": v(-13.26, 25) * mm});
            skArc(sketch, "E17.4.3.3", {"start": v(-16.27, 22) * mm, "mid": v(-16.27, 21.83) * mm, "end": v(-16.27, 21.66) * mm});
            skArc(sketch, "E17.4.3.4", {"start": v(-13.26, 18.66) * mm, "mid": v(-14.38, 20.55) * mm, "end": v(-16.27, 21.66) * mm});
            skArc(sketch, "E17.4.3.5", {"start": v(-9.93, 21.66) * mm, "mid": v(-11.82, 20.55) * mm, "end": v(-12.93, 18.66) * mm});
            skArc(sketch, "E17.4.3.6", {"start": v(-13.26, 18.66) * mm, "mid": v(-13.1, 18.65) * mm, "end": v(-12.93, 18.66) * mm});
            skArc(sketch, "E17.4.3.7", {"start": v(-9.93, 21.66) * mm, "mid": v(-9.92, 21.83) * mm, "end": v(-9.93, 22) * mm});
            skArc(sketch, "E17.4.4.0", {"start": v(-12.93, 16.27) * mm, "mid": v(-11.82, 14.38) * mm, "end": v(-9.93, 13.26) * mm});
            skArc(sketch, "E17.4.4.1", {"start": v(-16.27, 13.26) * mm, "mid": v(-14.38, 14.38) * mm, "end": v(-13.26, 16.27) * mm});
            skArc(sketch, "E17.4.4.2", {"start": v(-12.93, 16.27) * mm, "mid": v(-13.1, 16.27) * mm, "end": v(-13.26, 16.27) * mm});
            skArc(sketch, "E17.4.4.3", {"start": v(-16.27, 13.26) * mm, "mid": v(-16.27, 13.1) * mm, "end": v(-16.27, 12.93) * mm});
            skArc(sketch, "E17.4.4.4", {"start": v(-13.26, 9.93) * mm, "mid": v(-14.38, 11.82) * mm, "end": v(-16.27, 12.93) * mm});
            skArc(sketch, "E17.4.4.5", {"start": v(-9.93, 12.93) * mm, "mid": v(-11.82, 11.82) * mm, "end": v(-12.93, 9.93) * mm});
            skArc(sketch, "E17.4.4.6", {"start": v(-13.26, 9.93) * mm, "mid": v(-13.1, 9.92) * mm, "end": v(-12.93, 9.93) * mm});
            skArc(sketch, "E17.4.4.7", {"start": v(-9.93, 12.93) * mm, "mid": v(-9.92, 13.1) * mm, "end": v(-9.93, 13.26) * mm});
            skArc(sketch, "E17.4.5.0", {"start": v(-12.93, 7.54) * mm, "mid": v(-11.82, 5.64) * mm, "end": v(-9.93, 4.53) * mm});
            skArc(sketch, "E17.4.5.1", {"start": v(-16.27, 4.53) * mm, "mid": v(-14.38, 5.64) * mm, "end": v(-13.26, 7.54) * mm});
            skArc(sketch, "E17.4.5.2", {"start": v(-12.93, 7.54) * mm, "mid": v(-13.1, 7.54) * mm, "end": v(-13.26, 7.54) * mm});
            skArc(sketch, "E17.4.5.3", {"start": v(-16.27, 4.53) * mm, "mid": v(-16.27, 4.37) * mm, "end": v(-16.27, 4.2) * mm});
            skArc(sketch, "E17.4.5.4", {"start": v(-13.26, 1.2) * mm, "mid": v(-14.38, 3.09) * mm, "end": v(-16.27, 4.2) * mm});
            skArc(sketch, "E17.4.5.5", {"start": v(-9.93, 4.2) * mm, "mid": v(-11.82, 3.09) * mm, "end": v(-12.93, 1.2) * mm});
            skArc(sketch, "E17.4.5.6", {"start": v(-13.26, 1.2) * mm, "mid": v(-13.1, 1.2) * mm, "end": v(-12.93, 1.2) * mm});
            skArc(sketch, "E17.4.5.7", {"start": v(-9.93, 4.2) * mm, "mid": v(-9.92, 4.37) * mm, "end": v(-9.93, 4.53) * mm});
            skArc(sketch, "E17.4.6.0", {"start": v(-12.93, -1.2) * mm, "mid": v(-11.82, -3.09) * mm, "end": v(-9.93, -4.2) * mm});
            skArc(sketch, "E17.4.6.1", {"start": v(-16.27, -4.2) * mm, "mid": v(-14.38, -3.09) * mm, "end": v(-13.26, -1.2) * mm});
            skArc(sketch, "E17.4.6.2", {"start": v(-12.93, -1.2) * mm, "mid": v(-13.1, -1.2) * mm, "end": v(-13.26, -1.2) * mm});
            skArc(sketch, "E17.4.6.3", {"start": v(-16.27, -4.2) * mm, "mid": v(-16.27, -4.37) * mm, "end": v(-16.27, -4.53) * mm});
            skArc(sketch, "E17.4.6.4", {"start": v(-13.26, -7.54) * mm, "mid": v(-14.38, -5.64) * mm, "end": v(-16.27, -4.53) * mm});
            skArc(sketch, "E17.4.6.5", {"start": v(-9.93, -4.53) * mm, "mid": v(-11.82, -5.64) * mm, "end": v(-12.93, -7.54) * mm});
            skArc(sketch, "E17.4.6.6", {"start": v(-13.26, -7.54) * mm, "mid": v(-13.1, -7.54) * mm, "end": v(-12.93, -7.54) * mm});
            skArc(sketch, "E17.4.6.7", {"start": v(-9.93, -4.53) * mm, "mid": v(-9.92, -4.37) * mm, "end": v(-9.93, -4.2) * mm});
            skArc(sketch, "E17.4.7.0", {"start": v(-12.93, -9.93) * mm, "mid": v(-11.82, -11.82) * mm, "end": v(-9.93, -12.93) * mm});
            skArc(sketch, "E17.4.7.1", {"start": v(-16.27, -12.93) * mm, "mid": v(-14.38, -11.82) * mm, "end": v(-13.26, -9.93) * mm});
            skArc(sketch, "E17.4.7.2", {"start": v(-12.93, -9.93) * mm, "mid": v(-13.1, -9.92) * mm, "end": v(-13.26, -9.93) * mm});
            skArc(sketch, "E17.4.7.3", {"start": v(-16.27, -12.93) * mm, "mid": v(-16.27, -13.1) * mm, "end": v(-16.27, -13.26) * mm});
            skArc(sketch, "E17.4.7.4", {"start": v(-13.26, -16.27) * mm, "mid": v(-14.38, -14.38) * mm, "end": v(-16.27, -13.26) * mm});
            skArc(sketch, "E17.4.7.5", {"start": v(-9.93, -13.26) * mm, "mid": v(-11.82, -14.38) * mm, "end": v(-12.93, -16.27) * mm});
            skArc(sketch, "E17.4.7.6", {"start": v(-13.26, -16.27) * mm, "mid": v(-13.1, -16.27) * mm, "end": v(-12.93, -16.27) * mm});
            skArc(sketch, "E17.4.7.7", {"start": v(-9.93, -13.26) * mm, "mid": v(-9.92, -13.1) * mm, "end": v(-9.93, -12.93) * mm});
            skArc(sketch, "E17.4.8.0", {"start": v(-12.93, -18.66) * mm, "mid": v(-11.82, -20.55) * mm, "end": v(-9.93, -21.66) * mm});
            skArc(sketch, "E17.4.8.1", {"start": v(-16.27, -21.66) * mm, "mid": v(-14.38, -20.55) * mm, "end": v(-13.26, -18.66) * mm});
            skArc(sketch, "E17.4.8.2", {"start": v(-12.93, -18.66) * mm, "mid": v(-13.1, -18.65) * mm, "end": v(-13.26, -18.66) * mm});
            skArc(sketch, "E17.4.8.3", {"start": v(-16.27, -21.66) * mm, "mid": v(-16.27, -21.83) * mm, "end": v(-16.27, -22) * mm});
            skArc(sketch, "E17.4.8.4", {"start": v(-13.26, -25) * mm, "mid": v(-14.38, -23.1) * mm, "end": v(-16.27, -22) * mm});
            skArc(sketch, "E17.4.8.5", {"start": v(-9.93, -22) * mm, "mid": v(-11.82, -23.1) * mm, "end": v(-12.93, -25) * mm});
            skArc(sketch, "E17.4.8.6", {"start": v(-13.26, -25) * mm, "mid": v(-13.1, -25) * mm, "end": v(-12.93, -25) * mm});
            skArc(sketch, "E17.4.8.7", {"start": v(-9.93, -22) * mm, "mid": v(-9.92, -21.83) * mm, "end": v(-9.93, -21.66) * mm});
            skArc(sketch, "E17.4.9.0", {"start": v(-12.93, -27.39) * mm, "mid": v(-11.82, -29.28) * mm, "end": v(-9.93, -30.4) * mm});
            skArc(sketch, "E17.4.9.1", {"start": v(-16.27, -30.4) * mm, "mid": v(-14.38, -29.28) * mm, "end": v(-13.26, -27.39) * mm});
            skArc(sketch, "E17.4.9.2", {"start": v(-12.93, -27.39) * mm, "mid": v(-13.1, -27.38) * mm, "end": v(-13.26, -27.39) * mm});
            skArc(sketch, "E17.4.9.3", {"start": v(-16.27, -30.4) * mm, "mid": v(-16.27, -30.56) * mm, "end": v(-16.27, -30.73) * mm});
            skArc(sketch, "E17.4.9.4", {"start": v(-13.26, -33.73) * mm, "mid": v(-14.38, -31.84) * mm, "end": v(-16.27, -30.73) * mm});
            skArc(sketch, "E17.4.9.5", {"start": v(-9.93, -30.73) * mm, "mid": v(-11.82, -31.84) * mm, "end": v(-12.93, -33.73) * mm});
            skArc(sketch, "E17.4.9.6", {"start": v(-13.26, -33.73) * mm, "mid": v(-13.1, -33.73) * mm, "end": v(-12.93, -33.73) * mm});
            skArc(sketch, "E17.4.9.7", {"start": v(-9.93, -30.73) * mm, "mid": v(-9.92, -30.56) * mm, "end": v(-9.93, -30.4) * mm});
            skArc(sketch, "E17.4.10.0", {"start": v(-12.93, -36.12) * mm, "mid": v(-11.82, -38.01) * mm, "end": v(-9.93, -39.12) * mm});
            skArc(sketch, "E17.4.10.1", {"start": v(-16.27, -39.12) * mm, "mid": v(-14.38, -38.01) * mm, "end": v(-13.26, -36.12) * mm});
            skArc(sketch, "E17.4.10.2", {"start": v(-12.93, -36.12) * mm, "mid": v(-13.1, -36.12) * mm, "end": v(-13.26, -36.12) * mm});
            skArc(sketch, "E17.4.10.3", {"start": v(-16.27, -39.12) * mm, "mid": v(-16.27, -39.3) * mm, "end": v(-16.27, -39.46) * mm});
            skArc(sketch, "E17.4.10.4", {"start": v(-13.26, -42.46) * mm, "mid": v(-14.38, -40.57) * mm, "end": v(-16.27, -39.46) * mm});
            skArc(sketch, "E17.4.10.5", {"start": v(-9.93, -39.46) * mm, "mid": v(-11.82, -40.57) * mm, "end": v(-12.93, -42.46) * mm});
            skArc(sketch, "E17.4.10.6", {"start": v(-13.26, -42.46) * mm, "mid": v(-13.1, -42.47) * mm, "end": v(-12.93, -42.46) * mm});
            skArc(sketch, "E17.4.10.7", {"start": v(-9.93, -39.46) * mm, "mid": v(-9.92, -39.3) * mm, "end": v(-9.93, -39.12) * mm});
            skArc(sketch, "E17.4.11.0", {"start": v(-12.93, -44.85) * mm, "mid": v(-11.82, -46.74) * mm, "end": v(-9.93, -47.86) * mm});
            skArc(sketch, "E17.4.11.1", {"start": v(-16.27, -47.86) * mm, "mid": v(-14.38, -46.74) * mm, "end": v(-13.26, -44.85) * mm});
            skArc(sketch, "E17.4.11.2", {"start": v(-12.93, -44.85) * mm, "mid": v(-13.1, -44.85) * mm, "end": v(-13.26, -44.85) * mm});
            skArc(sketch, "E17.4.11.3", {"start": v(-16.27, -47.86) * mm, "mid": v(-16.27, -48.02) * mm, "end": v(-16.27, -48.19) * mm});
            skArc(sketch, "E17.4.11.4", {"start": v(-13.26, -51.2) * mm, "mid": v(-14.38, -49.3) * mm, "end": v(-16.27, -48.19) * mm});
            skArc(sketch, "E17.4.11.5", {"start": v(-9.93, -48.19) * mm, "mid": v(-11.82, -49.3) * mm, "end": v(-12.93, -51.2) * mm});
            skArc(sketch, "E17.4.11.6", {"start": v(-13.26, -51.2) * mm, "mid": v(-13.1, -51.2) * mm, "end": v(-12.93, -51.2) * mm});
            skArc(sketch, "E17.4.11.7", {"start": v(-9.93, -48.19) * mm, "mid": v(-9.92, -48.02) * mm, "end": v(-9.93, -47.86) * mm});
            skArc(sketch, "E17.5.0.0", {"start": v(-4.2, 51.2) * mm, "mid": v(-3.09, 49.3) * mm, "end": v(-1.2, 48.19) * mm});
            skArc(sketch, "E17.5.0.1", {"start": v(-7.54, 48.19) * mm, "mid": v(-5.64, 49.3) * mm, "end": v(-4.53, 51.2) * mm});
            skArc(sketch, "E17.5.0.2", {"start": v(-4.2, 51.2) * mm, "mid": v(-4.37, 51.2) * mm, "end": v(-4.53, 51.2) * mm});
            skArc(sketch, "E17.5.0.3", {"start": v(-7.54, 48.19) * mm, "mid": v(-7.54, 48.02) * mm, "end": v(-7.54, 47.86) * mm});
            skArc(sketch, "E17.5.0.4", {"start": v(-4.53, 44.85) * mm, "mid": v(-5.64, 46.74) * mm, "end": v(-7.54, 47.86) * mm});
            skArc(sketch, "E17.5.0.5", {"start": v(-1.2, 47.86) * mm, "mid": v(-3.09, 46.74) * mm, "end": v(-4.2, 44.85) * mm});
            skArc(sketch, "E17.5.0.6", {"start": v(-4.53, 44.85) * mm, "mid": v(-4.37, 44.85) * mm, "end": v(-4.2, 44.85) * mm});
            skArc(sketch, "E17.5.0.7", {"start": v(-1.2, 47.86) * mm, "mid": v(-1.2, 48.02) * mm, "end": v(-1.2, 48.19) * mm});
            skArc(sketch, "E17.5.1.0", {"start": v(-4.2, 42.46) * mm, "mid": v(-3.09, 40.57) * mm, "end": v(-1.2, 39.46) * mm});
            skArc(sketch, "E17.5.1.1", {"start": v(-7.54, 39.46) * mm, "mid": v(-5.64, 40.57) * mm, "end": v(-4.53, 42.46) * mm});
            skArc(sketch, "E17.5.1.2", {"start": v(-4.2, 42.46) * mm, "mid": v(-4.37, 42.47) * mm, "end": v(-4.53, 42.46) * mm});
            skArc(sketch, "E17.5.1.3", {"start": v(-7.54, 39.46) * mm, "mid": v(-7.54, 39.3) * mm, "end": v(-7.54, 39.12) * mm});
            skArc(sketch, "E17.5.1.4", {"start": v(-4.53, 36.12) * mm, "mid": v(-5.64, 38.01) * mm, "end": v(-7.54, 39.12) * mm});
            skArc(sketch, "E17.5.1.5", {"start": v(-1.2, 39.12) * mm, "mid": v(-3.09, 38.01) * mm, "end": v(-4.2, 36.12) * mm});
            skArc(sketch, "E17.5.1.6", {"start": v(-4.53, 36.12) * mm, "mid": v(-4.37, 36.12) * mm, "end": v(-4.2, 36.12) * mm});
            skArc(sketch, "E17.5.1.7", {"start": v(-1.2, 39.12) * mm, "mid": v(-1.2, 39.3) * mm, "end": v(-1.2, 39.46) * mm});
            skArc(sketch, "E17.5.2.0", {"start": v(-4.2, 33.73) * mm, "mid": v(-3.09, 31.84) * mm, "end": v(-1.2, 30.73) * mm});
            skArc(sketch, "E17.5.2.1", {"start": v(-7.54, 30.73) * mm, "mid": v(-5.64, 31.84) * mm, "end": v(-4.53, 33.73) * mm});
            skArc(sketch, "E17.5.2.2", {"start": v(-4.2, 33.73) * mm, "mid": v(-4.37, 33.73) * mm, "end": v(-4.53, 33.73) * mm});
            skArc(sketch, "E17.5.2.3", {"start": v(-7.54, 30.73) * mm, "mid": v(-7.54, 30.56) * mm, "end": v(-7.54, 30.4) * mm});
            skArc(sketch, "E17.5.2.4", {"start": v(-4.53, 27.39) * mm, "mid": v(-5.64, 29.28) * mm, "end": v(-7.54, 30.4) * mm});
            skArc(sketch, "E17.5.2.5", {"start": v(-1.2, 30.4) * mm, "mid": v(-3.09, 29.28) * mm, "end": v(-4.2, 27.39) * mm});
            skArc(sketch, "E17.5.2.6", {"start": v(-4.53, 27.39) * mm, "mid": v(-4.37, 27.38) * mm, "end": v(-4.2, 27.39) * mm});
            skArc(sketch, "E17.5.2.7", {"start": v(-1.2, 30.4) * mm, "mid": v(-1.2, 30.56) * mm, "end": v(-1.2, 30.73) * mm});
            skArc(sketch, "E17.5.3.0", {"start": v(-4.2, 25) * mm, "mid": v(-3.09, 23.1) * mm, "end": v(-1.2, 22) * mm});
            skArc(sketch, "E17.5.3.1", {"start": v(-7.54, 22) * mm, "mid": v(-5.64, 23.1) * mm, "end": v(-4.53, 25) * mm});
            skArc(sketch, "E17.5.3.2", {"start": v(-4.2, 25) * mm, "mid": v(-4.37, 25) * mm, "end": v(-4.53, 25) * mm});
            skArc(sketch, "E17.5.3.3", {"start": v(-7.54, 22) * mm, "mid": v(-7.54, 21.83) * mm, "end": v(-7.54, 21.66) * mm});
            skArc(sketch, "E17.5.3.4", {"start": v(-4.53, 18.66) * mm, "mid": v(-5.64, 20.55) * mm, "end": v(-7.54, 21.66) * mm});
            skArc(sketch, "E17.5.3.5", {"start": v(-1.2, 21.66) * mm, "mid": v(-3.09, 20.55) * mm, "end": v(-4.2, 18.66) * mm});
            skArc(sketch, "E17.5.3.6", {"start": v(-4.53, 18.66) * mm, "mid": v(-4.37, 18.65) * mm, "end": v(-4.2, 18.66) * mm});
            skArc(sketch, "E17.5.3.7", {"start": v(-1.2, 21.66) * mm, "mid": v(-1.2, 21.83) * mm, "end": v(-1.2, 22) * mm});
            skArc(sketch, "E17.5.4.0", {"start": v(-4.2, 16.27) * mm, "mid": v(-3.09, 14.38) * mm, "end": v(-1.2, 13.26) * mm});
            skArc(sketch, "E17.5.4.1", {"start": v(-7.54, 13.26) * mm, "mid": v(-5.64, 14.38) * mm, "end": v(-4.53, 16.27) * mm});
            skArc(sketch, "E17.5.4.2", {"start": v(-4.2, 16.27) * mm, "mid": v(-4.37, 16.27) * mm, "end": v(-4.53, 16.27) * mm});
            skArc(sketch, "E17.5.4.3", {"start": v(-7.54, 13.26) * mm, "mid": v(-7.54, 13.1) * mm, "end": v(-7.54, 12.93) * mm});
            skArc(sketch, "E17.5.4.4", {"start": v(-4.53, 9.93) * mm, "mid": v(-5.64, 11.82) * mm, "end": v(-7.54, 12.93) * mm});
            skArc(sketch, "E17.5.4.5", {"start": v(-1.2, 12.93) * mm, "mid": v(-3.09, 11.82) * mm, "end": v(-4.2, 9.93) * mm});
            skArc(sketch, "E17.5.4.6", {"start": v(-4.53, 9.93) * mm, "mid": v(-4.37, 9.92) * mm, "end": v(-4.2, 9.93) * mm});
            skArc(sketch, "E17.5.4.7", {"start": v(-1.2, 12.93) * mm, "mid": v(-1.2, 13.1) * mm, "end": v(-1.2, 13.26) * mm});
            skArc(sketch, "E17.5.5.0", {"start": v(-4.2, 7.54) * mm, "mid": v(-3.09, 5.64) * mm, "end": v(-1.2, 4.53) * mm});
            skArc(sketch, "E17.5.5.1", {"start": v(-7.54, 4.53) * mm, "mid": v(-5.64, 5.64) * mm, "end": v(-4.53, 7.54) * mm});
            skArc(sketch, "E17.5.5.2", {"start": v(-4.2, 7.54) * mm, "mid": v(-4.37, 7.54) * mm, "end": v(-4.53, 7.54) * mm});
            skArc(sketch, "E17.5.5.3", {"start": v(-7.54, 4.53) * mm, "mid": v(-7.54, 4.37) * mm, "end": v(-7.54, 4.2) * mm});
            skArc(sketch, "E17.5.5.4", {"start": v(-4.53, 1.2) * mm, "mid": v(-5.64, 3.09) * mm, "end": v(-7.54, 4.2) * mm});
            skArc(sketch, "E17.5.5.5", {"start": v(-1.2, 4.2) * mm, "mid": v(-3.09, 3.09) * mm, "end": v(-4.2, 1.2) * mm});
            skArc(sketch, "E17.5.5.6", {"start": v(-4.53, 1.2) * mm, "mid": v(-4.37, 1.2) * mm, "end": v(-4.2, 1.2) * mm});
            skArc(sketch, "E17.5.5.7", {"start": v(-1.2, 4.2) * mm, "mid": v(-1.2, 4.37) * mm, "end": v(-1.2, 4.53) * mm});
            skArc(sketch, "E17.5.6.0", {"start": v(-4.2, -1.2) * mm, "mid": v(-3.09, -3.09) * mm, "end": v(-1.2, -4.2) * mm});
            skArc(sketch, "E17.5.6.1", {"start": v(-7.54, -4.2) * mm, "mid": v(-5.64, -3.09) * mm, "end": v(-4.53, -1.2) * mm});
            skArc(sketch, "E17.5.6.2", {"start": v(-4.2, -1.2) * mm, "mid": v(-4.37, -1.2) * mm, "end": v(-4.53, -1.2) * mm});
            skArc(sketch, "E17.5.6.3", {"start": v(-7.54, -4.2) * mm, "mid": v(-7.54, -4.37) * mm, "end": v(-7.54, -4.53) * mm});
            skArc(sketch, "E17.5.6.4", {"start": v(-4.53, -7.54) * mm, "mid": v(-5.64, -5.64) * mm, "end": v(-7.54, -4.53) * mm});
            skArc(sketch, "E17.5.6.5", {"start": v(-1.2, -4.53) * mm, "mid": v(-3.09, -5.64) * mm, "end": v(-4.2, -7.54) * mm});
            skArc(sketch, "E17.5.6.6", {"start": v(-4.53, -7.54) * mm, "mid": v(-4.37, -7.54) * mm, "end": v(-4.2, -7.54) * mm});
            skArc(sketch, "E17.5.6.7", {"start": v(-1.2, -4.53) * mm, "mid": v(-1.2, -4.37) * mm, "end": v(-1.2, -4.2) * mm});
            skArc(sketch, "E17.5.7.0", {"start": v(-4.2, -9.93) * mm, "mid": v(-3.09, -11.82) * mm, "end": v(-1.2, -12.93) * mm});
            skArc(sketch, "E17.5.7.1", {"start": v(-7.54, -12.93) * mm, "mid": v(-5.64, -11.82) * mm, "end": v(-4.53, -9.93) * mm});
            skArc(sketch, "E17.5.7.2", {"start": v(-4.2, -9.93) * mm, "mid": v(-4.37, -9.92) * mm, "end": v(-4.53, -9.93) * mm});
            skArc(sketch, "E17.5.7.3", {"start": v(-7.54, -12.93) * mm, "mid": v(-7.54, -13.1) * mm, "end": v(-7.54, -13.26) * mm});
            skArc(sketch, "E17.5.7.4", {"start": v(-4.53, -16.27) * mm, "mid": v(-5.64, -14.38) * mm, "end": v(-7.54, -13.26) * mm});
            skArc(sketch, "E17.5.7.5", {"start": v(-1.2, -13.26) * mm, "mid": v(-3.09, -14.38) * mm, "end": v(-4.2, -16.27) * mm});
            skArc(sketch, "E17.5.7.6", {"start": v(-4.53, -16.27) * mm, "mid": v(-4.37, -16.27) * mm, "end": v(-4.2, -16.27) * mm});
            skArc(sketch, "E17.5.7.7", {"start": v(-1.2, -13.26) * mm, "mid": v(-1.2, -13.1) * mm, "end": v(-1.2, -12.93) * mm});
            skArc(sketch, "E17.5.8.0", {"start": v(-4.2, -18.66) * mm, "mid": v(-3.09, -20.55) * mm, "end": v(-1.2, -21.66) * mm});
            skArc(sketch, "E17.5.8.1", {"start": v(-7.54, -21.66) * mm, "mid": v(-5.64, -20.55) * mm, "end": v(-4.53, -18.66) * mm});
            skArc(sketch, "E17.5.8.2", {"start": v(-4.2, -18.66) * mm, "mid": v(-4.37, -18.65) * mm, "end": v(-4.53, -18.66) * mm});
            skArc(sketch, "E17.5.8.3", {"start": v(-7.54, -21.66) * mm, "mid": v(-7.54, -21.83) * mm, "end": v(-7.54, -22) * mm});
            skArc(sketch, "E17.5.8.4", {"start": v(-4.53, -25) * mm, "mid": v(-5.64, -23.1) * mm, "end": v(-7.54, -22) * mm});
            skArc(sketch, "E17.5.8.5", {"start": v(-1.2, -22) * mm, "mid": v(-3.09, -23.1) * mm, "end": v(-4.2, -25) * mm});
            skArc(sketch, "E17.5.8.6", {"start": v(-4.53, -25) * mm, "mid": v(-4.37, -25) * mm, "end": v(-4.2, -25) * mm});
            skArc(sketch, "E17.5.8.7", {"start": v(-1.2, -22) * mm, "mid": v(-1.2, -21.83) * mm, "end": v(-1.2, -21.66) * mm});
            skArc(sketch, "E17.5.9.0", {"start": v(-4.2, -27.39) * mm, "mid": v(-3.09, -29.28) * mm, "end": v(-1.2, -30.4) * mm});
            skArc(sketch, "E17.5.9.1", {"start": v(-7.54, -30.4) * mm, "mid": v(-5.64, -29.28) * mm, "end": v(-4.53, -27.39) * mm});
            skArc(sketch, "E17.5.9.2", {"start": v(-4.2, -27.39) * mm, "mid": v(-4.37, -27.38) * mm, "end": v(-4.53, -27.39) * mm});
            skArc(sketch, "E17.5.9.3", {"start": v(-7.54, -30.4) * mm, "mid": v(-7.54, -30.56) * mm, "end": v(-7.54, -30.73) * mm});
            skArc(sketch, "E17.5.9.4", {"start": v(-4.53, -33.73) * mm, "mid": v(-5.64, -31.84) * mm, "end": v(-7.54, -30.73) * mm});
            skArc(sketch, "E17.5.9.5", {"start": v(-1.2, -30.73) * mm, "mid": v(-3.09, -31.84) * mm, "end": v(-4.2, -33.73) * mm});
            skArc(sketch, "E17.5.9.6", {"start": v(-4.53, -33.73) * mm, "mid": v(-4.37, -33.73) * mm, "end": v(-4.2, -33.73) * mm});
            skArc(sketch, "E17.5.9.7", {"start": v(-1.2, -30.73) * mm, "mid": v(-1.2, -30.56) * mm, "end": v(-1.2, -30.4) * mm});
            skArc(sketch, "E17.5.10.0", {"start": v(-4.2, -36.12) * mm, "mid": v(-3.09, -38.01) * mm, "end": v(-1.2, -39.12) * mm});
            skArc(sketch, "E17.5.10.1", {"start": v(-7.54, -39.12) * mm, "mid": v(-5.64, -38.01) * mm, "end": v(-4.53, -36.12) * mm});
            skArc(sketch, "E17.5.10.2", {"start": v(-4.2, -36.12) * mm, "mid": v(-4.37, -36.12) * mm, "end": v(-4.53, -36.12) * mm});
            skArc(sketch, "E17.5.10.3", {"start": v(-7.54, -39.12) * mm, "mid": v(-7.54, -39.3) * mm, "end": v(-7.54, -39.46) * mm});
            skArc(sketch, "E17.5.10.4", {"start": v(-4.53, -42.46) * mm, "mid": v(-5.64, -40.57) * mm, "end": v(-7.54, -39.46) * mm});
            skArc(sketch, "E17.5.10.5", {"start": v(-1.2, -39.46) * mm, "mid": v(-3.09, -40.57) * mm, "end": v(-4.2, -42.46) * mm});
            skArc(sketch, "E17.5.10.6", {"start": v(-4.53, -42.46) * mm, "mid": v(-4.37, -42.47) * mm, "end": v(-4.2, -42.46) * mm});
            skArc(sketch, "E17.5.10.7", {"start": v(-1.2, -39.46) * mm, "mid": v(-1.2, -39.3) * mm, "end": v(-1.2, -39.12) * mm});
            skArc(sketch, "E17.5.11.0", {"start": v(-4.2, -44.85) * mm, "mid": v(-3.09, -46.74) * mm, "end": v(-1.2, -47.86) * mm});
            skArc(sketch, "E17.5.11.1", {"start": v(-7.54, -47.86) * mm, "mid": v(-5.64, -46.74) * mm, "end": v(-4.53, -44.85) * mm});
            skArc(sketch, "E17.5.11.2", {"start": v(-4.2, -44.85) * mm, "mid": v(-4.37, -44.85) * mm, "end": v(-4.53, -44.85) * mm});
            skArc(sketch, "E17.5.11.3", {"start": v(-7.54, -47.86) * mm, "mid": v(-7.54, -48.02) * mm, "end": v(-7.54, -48.19) * mm});
            skArc(sketch, "E17.5.11.4", {"start": v(-4.53, -51.2) * mm, "mid": v(-5.64, -49.3) * mm, "end": v(-7.54, -48.19) * mm});
            skArc(sketch, "E17.5.11.5", {"start": v(-1.2, -48.19) * mm, "mid": v(-3.09, -49.3) * mm, "end": v(-4.2, -51.2) * mm});
            skArc(sketch, "E17.5.11.6", {"start": v(-4.53, -51.2) * mm, "mid": v(-4.37, -51.2) * mm, "end": v(-4.2, -51.2) * mm});
            skArc(sketch, "E17.5.11.7", {"start": v(-1.2, -48.19) * mm, "mid": v(-1.2, -48.02) * mm, "end": v(-1.2, -47.86) * mm});
            skArc(sketch, "E17.6.0.0", {"start": v(4.53, 51.2) * mm, "mid": v(5.64, 49.3) * mm, "end": v(7.54, 48.19) * mm});
            skArc(sketch, "E17.6.0.1", {"start": v(1.2, 48.19) * mm, "mid": v(3.09, 49.3) * mm, "end": v(4.2, 51.2) * mm});
            skArc(sketch, "E17.6.0.2", {"start": v(4.53, 51.2) * mm, "mid": v(4.37, 51.2) * mm, "end": v(4.2, 51.2) * mm});
            skArc(sketch, "E17.6.0.3", {"start": v(1.2, 48.19) * mm, "mid": v(1.2, 48.02) * mm, "end": v(1.2, 47.86) * mm});
            skArc(sketch, "E17.6.0.4", {"start": v(4.2, 44.85) * mm, "mid": v(3.09, 46.74) * mm, "end": v(1.2, 47.86) * mm});
            skArc(sketch, "E17.6.0.5", {"start": v(7.54, 47.86) * mm, "mid": v(5.64, 46.74) * mm, "end": v(4.53, 44.85) * mm});
            skArc(sketch, "E17.6.0.6", {"start": v(4.2, 44.85) * mm, "mid": v(4.37, 44.85) * mm, "end": v(4.53, 44.85) * mm});
            skArc(sketch, "E17.6.0.7", {"start": v(7.54, 47.86) * mm, "mid": v(7.54, 48.02) * mm, "end": v(7.54, 48.19) * mm});
            skArc(sketch, "E17.6.1.0", {"start": v(4.53, 42.46) * mm, "mid": v(5.64, 40.57) * mm, "end": v(7.54, 39.46) * mm});
            skArc(sketch, "E17.6.1.1", {"start": v(1.2, 39.46) * mm, "mid": v(3.09, 40.57) * mm, "end": v(4.2, 42.46) * mm});
            skArc(sketch, "E17.6.1.2", {"start": v(4.53, 42.46) * mm, "mid": v(4.37, 42.47) * mm, "end": v(4.2, 42.46) * mm});
            skArc(sketch, "E17.6.1.3", {"start": v(1.2, 39.46) * mm, "mid": v(1.2, 39.3) * mm, "end": v(1.2, 39.12) * mm});
            skArc(sketch, "E17.6.1.4", {"start": v(4.2, 36.12) * mm, "mid": v(3.09, 38.01) * mm, "end": v(1.2, 39.12) * mm});
            skArc(sketch, "E17.6.1.5", {"start": v(7.54, 39.12) * mm, "mid": v(5.64, 38.01) * mm, "end": v(4.53, 36.12) * mm});
            skArc(sketch, "E17.6.1.6", {"start": v(4.2, 36.12) * mm, "mid": v(4.37, 36.12) * mm, "end": v(4.53, 36.12) * mm});
            skArc(sketch, "E17.6.1.7", {"start": v(7.54, 39.12) * mm, "mid": v(7.54, 39.3) * mm, "end": v(7.54, 39.46) * mm});
            skArc(sketch, "E17.6.2.0", {"start": v(4.53, 33.73) * mm, "mid": v(5.64, 31.84) * mm, "end": v(7.54, 30.73) * mm});
            skArc(sketch, "E17.6.2.1", {"start": v(1.2, 30.73) * mm, "mid": v(3.09, 31.84) * mm, "end": v(4.2, 33.73) * mm});
            skArc(sketch, "E17.6.2.2", {"start": v(4.53, 33.73) * mm, "mid": v(4.37, 33.73) * mm, "end": v(4.2, 33.73) * mm});
            skArc(sketch, "E17.6.2.3", {"start": v(1.2, 30.73) * mm, "mid": v(1.2, 30.56) * mm, "end": v(1.2, 30.4) * mm});
            skArc(sketch, "E17.6.2.4", {"start": v(4.2, 27.39) * mm, "mid": v(3.09, 29.28) * mm, "end": v(1.2, 30.4) * mm});
            skArc(sketch, "E17.6.2.5", {"start": v(7.54, 30.4) * mm, "mid": v(5.64, 29.28) * mm, "end": v(4.53, 27.39) * mm});
            skArc(sketch, "E17.6.2.6", {"start": v(4.2, 27.39) * mm, "mid": v(4.37, 27.38) * mm, "end": v(4.53, 27.39) * mm});
            skArc(sketch, "E17.6.2.7", {"start": v(7.54, 30.4) * mm, "mid": v(7.54, 30.56) * mm, "end": v(7.54, 30.73) * mm});
            skArc(sketch, "E17.6.3.0", {"start": v(4.53, 25) * mm, "mid": v(5.64, 23.1) * mm, "end": v(7.54, 22) * mm});
            skArc(sketch, "E17.6.3.1", {"start": v(1.2, 22) * mm, "mid": v(3.09, 23.1) * mm, "end": v(4.2, 25) * mm});
            skArc(sketch, "E17.6.3.2", {"start": v(4.53, 25) * mm, "mid": v(4.37, 25) * mm, "end": v(4.2, 25) * mm});
            skArc(sketch, "E17.6.3.3", {"start": v(1.2, 22) * mm, "mid": v(1.2, 21.83) * mm, "end": v(1.2, 21.66) * mm});
            skArc(sketch, "E17.6.3.4", {"start": v(4.2, 18.66) * mm, "mid": v(3.09, 20.55) * mm, "end": v(1.2, 21.66) * mm});
            skArc(sketch, "E17.6.3.5", {"start": v(7.54, 21.66) * mm, "mid": v(5.64, 20.55) * mm, "end": v(4.53, 18.66) * mm});
            skArc(sketch, "E17.6.3.6", {"start": v(4.2, 18.66) * mm, "mid": v(4.37, 18.65) * mm, "end": v(4.53, 18.66) * mm});
            skArc(sketch, "E17.6.3.7", {"start": v(7.54, 21.66) * mm, "mid": v(7.54, 21.83) * mm, "end": v(7.54, 22) * mm});
            skArc(sketch, "E17.6.4.0", {"start": v(4.53, 16.27) * mm, "mid": v(5.64, 14.38) * mm, "end": v(7.54, 13.26) * mm});
            skArc(sketch, "E17.6.4.1", {"start": v(1.2, 13.26) * mm, "mid": v(3.09, 14.38) * mm, "end": v(4.2, 16.27) * mm});
            skArc(sketch, "E17.6.4.2", {"start": v(4.53, 16.27) * mm, "mid": v(4.37, 16.27) * mm, "end": v(4.2, 16.27) * mm});
            skArc(sketch, "E17.6.4.3", {"start": v(1.2, 13.26) * mm, "mid": v(1.2, 13.1) * mm, "end": v(1.2, 12.93) * mm});
            skArc(sketch, "E17.6.4.4", {"start": v(4.2, 9.93) * mm, "mid": v(3.09, 11.82) * mm, "end": v(1.2, 12.93) * mm});
            skArc(sketch, "E17.6.4.5", {"start": v(7.54, 12.93) * mm, "mid": v(5.64, 11.82) * mm, "end": v(4.53, 9.93) * mm});
            skArc(sketch, "E17.6.4.6", {"start": v(4.2, 9.93) * mm, "mid": v(4.37, 9.92) * mm, "end": v(4.53, 9.93) * mm});
            skArc(sketch, "E17.6.4.7", {"start": v(7.54, 12.93) * mm, "mid": v(7.54, 13.1) * mm, "end": v(7.54, 13.26) * mm});
            skArc(sketch, "E17.6.5.0", {"start": v(4.53, 7.54) * mm, "mid": v(5.64, 5.64) * mm, "end": v(7.54, 4.53) * mm});
            skArc(sketch, "E17.6.5.1", {"start": v(1.2, 4.53) * mm, "mid": v(3.09, 5.64) * mm, "end": v(4.2, 7.54) * mm});
            skArc(sketch, "E17.6.5.2", {"start": v(4.53, 7.54) * mm, "mid": v(4.37, 7.54) * mm, "end": v(4.2, 7.54) * mm});
            skArc(sketch, "E17.6.5.3", {"start": v(1.2, 4.53) * mm, "mid": v(1.2, 4.37) * mm, "end": v(1.2, 4.2) * mm});
            skArc(sketch, "E17.6.5.4", {"start": v(4.2, 1.2) * mm, "mid": v(3.09, 3.09) * mm, "end": v(1.2, 4.2) * mm});
            skArc(sketch, "E17.6.5.5", {"start": v(7.54, 4.2) * mm, "mid": v(5.64, 3.09) * mm, "end": v(4.53, 1.2) * mm});
            skArc(sketch, "E17.6.5.6", {"start": v(4.2, 1.2) * mm, "mid": v(4.37, 1.2) * mm, "end": v(4.53, 1.2) * mm});
            skArc(sketch, "E17.6.5.7", {"start": v(7.54, 4.2) * mm, "mid": v(7.54, 4.37) * mm, "end": v(7.54, 4.53) * mm});
            skArc(sketch, "E17.6.6.0", {"start": v(4.53, -1.2) * mm, "mid": v(5.64, -3.09) * mm, "end": v(7.54, -4.2) * mm});
            skArc(sketch, "E17.6.6.1", {"start": v(1.2, -4.2) * mm, "mid": v(3.09, -3.09) * mm, "end": v(4.2, -1.2) * mm});
            skArc(sketch, "E17.6.6.2", {"start": v(4.53, -1.2) * mm, "mid": v(4.37, -1.2) * mm, "end": v(4.2, -1.2) * mm});
            skArc(sketch, "E17.6.6.3", {"start": v(1.2, -4.2) * mm, "mid": v(1.2, -4.37) * mm, "end": v(1.2, -4.53) * mm});
            skArc(sketch, "E17.6.6.4", {"start": v(4.2, -7.54) * mm, "mid": v(3.09, -5.64) * mm, "end": v(1.2, -4.53) * mm});
            skArc(sketch, "E17.6.6.5", {"start": v(7.54, -4.53) * mm, "mid": v(5.64, -5.64) * mm, "end": v(4.53, -7.54) * mm});
            skArc(sketch, "E17.6.6.6", {"start": v(4.2, -7.54) * mm, "mid": v(4.37, -7.54) * mm, "end": v(4.53, -7.54) * mm});
            skArc(sketch, "E17.6.6.7", {"start": v(7.54, -4.53) * mm, "mid": v(7.54, -4.37) * mm, "end": v(7.54, -4.2) * mm});
            skArc(sketch, "E17.6.7.0", {"start": v(4.53, -9.93) * mm, "mid": v(5.64, -11.82) * mm, "end": v(7.54, -12.93) * mm});
            skArc(sketch, "E17.6.7.1", {"start": v(1.2, -12.93) * mm, "mid": v(3.09, -11.82) * mm, "end": v(4.2, -9.93) * mm});
            skArc(sketch, "E17.6.7.2", {"start": v(4.53, -9.93) * mm, "mid": v(4.37, -9.92) * mm, "end": v(4.2, -9.93) * mm});
            skArc(sketch, "E17.6.7.3", {"start": v(1.2, -12.93) * mm, "mid": v(1.2, -13.1) * mm, "end": v(1.2, -13.26) * mm});
            skArc(sketch, "E17.6.7.4", {"start": v(4.2, -16.27) * mm, "mid": v(3.09, -14.38) * mm, "end": v(1.2, -13.26) * mm});
            skArc(sketch, "E17.6.7.5", {"start": v(7.54, -13.26) * mm, "mid": v(5.64, -14.38) * mm, "end": v(4.53, -16.27) * mm});
            skArc(sketch, "E17.6.7.6", {"start": v(4.2, -16.27) * mm, "mid": v(4.37, -16.27) * mm, "end": v(4.53, -16.27) * mm});
            skArc(sketch, "E17.6.7.7", {"start": v(7.54, -13.26) * mm, "mid": v(7.54, -13.1) * mm, "end": v(7.54, -12.93) * mm});
            skArc(sketch, "E17.6.8.0", {"start": v(4.53, -18.66) * mm, "mid": v(5.64, -20.55) * mm, "end": v(7.54, -21.66) * mm});
            skArc(sketch, "E17.6.8.1", {"start": v(1.2, -21.66) * mm, "mid": v(3.09, -20.55) * mm, "end": v(4.2, -18.66) * mm});
            skArc(sketch, "E17.6.8.2", {"start": v(4.53, -18.66) * mm, "mid": v(4.37, -18.65) * mm, "end": v(4.2, -18.66) * mm});
            skArc(sketch, "E17.6.8.3", {"start": v(1.2, -21.66) * mm, "mid": v(1.2, -21.83) * mm, "end": v(1.2, -22) * mm});
            skArc(sketch, "E17.6.8.4", {"start": v(4.2, -25) * mm, "mid": v(3.09, -23.1) * mm, "end": v(1.2, -22) * mm});
            skArc(sketch, "E17.6.8.5", {"start": v(7.54, -22) * mm, "mid": v(5.64, -23.1) * mm, "end": v(4.53, -25) * mm});
            skArc(sketch, "E17.6.8.6", {"start": v(4.2, -25) * mm, "mid": v(4.37, -25) * mm, "end": v(4.53, -25) * mm});
            skArc(sketch, "E17.6.8.7", {"start": v(7.54, -22) * mm, "mid": v(7.54, -21.83) * mm, "end": v(7.54, -21.66) * mm});
            skArc(sketch, "E17.6.9.0", {"start": v(4.53, -27.39) * mm, "mid": v(5.64, -29.28) * mm, "end": v(7.54, -30.4) * mm});
            skArc(sketch, "E17.6.9.1", {"start": v(1.2, -30.4) * mm, "mid": v(3.09, -29.28) * mm, "end": v(4.2, -27.39) * mm});
            skArc(sketch, "E17.6.9.2", {"start": v(4.53, -27.39) * mm, "mid": v(4.37, -27.38) * mm, "end": v(4.2, -27.39) * mm});
            skArc(sketch, "E17.6.9.3", {"start": v(1.2, -30.4) * mm, "mid": v(1.2, -30.56) * mm, "end": v(1.2, -30.73) * mm});
            skArc(sketch, "E17.6.9.4", {"start": v(4.2, -33.73) * mm, "mid": v(3.09, -31.84) * mm, "end": v(1.2, -30.73) * mm});
            skArc(sketch, "E17.6.9.5", {"start": v(7.54, -30.73) * mm, "mid": v(5.64, -31.84) * mm, "end": v(4.53, -33.73) * mm});
            skArc(sketch, "E17.6.9.6", {"start": v(4.2, -33.73) * mm, "mid": v(4.37, -33.73) * mm, "end": v(4.53, -33.73) * mm});
            skArc(sketch, "E17.6.9.7", {"start": v(7.54, -30.73) * mm, "mid": v(7.54, -30.56) * mm, "end": v(7.54, -30.4) * mm});
            skArc(sketch, "E17.6.10.0", {"start": v(4.53, -36.12) * mm, "mid": v(5.64, -38.01) * mm, "end": v(7.54, -39.12) * mm});
            skArc(sketch, "E17.6.10.1", {"start": v(1.2, -39.12) * mm, "mid": v(3.09, -38.01) * mm, "end": v(4.2, -36.12) * mm});
            skArc(sketch, "E17.6.10.2", {"start": v(4.53, -36.12) * mm, "mid": v(4.37, -36.12) * mm, "end": v(4.2, -36.12) * mm});
            skArc(sketch, "E17.6.10.3", {"start": v(1.2, -39.12) * mm, "mid": v(1.2, -39.3) * mm, "end": v(1.2, -39.46) * mm});
            skArc(sketch, "E17.6.10.4", {"start": v(4.2, -42.46) * mm, "mid": v(3.09, -40.57) * mm, "end": v(1.2, -39.46) * mm});
            skArc(sketch, "E17.6.10.5", {"start": v(7.54, -39.46) * mm, "mid": v(5.64, -40.57) * mm, "end": v(4.53, -42.46) * mm});
            skArc(sketch, "E17.6.10.6", {"start": v(4.2, -42.46) * mm, "mid": v(4.37, -42.47) * mm, "end": v(4.53, -42.46) * mm});
            skArc(sketch, "E17.6.10.7", {"start": v(7.54, -39.46) * mm, "mid": v(7.54, -39.3) * mm, "end": v(7.54, -39.12) * mm});
            skArc(sketch, "E17.6.11.0", {"start": v(4.53, -44.85) * mm, "mid": v(5.64, -46.74) * mm, "end": v(7.54, -47.86) * mm});
            skArc(sketch, "E17.6.11.1", {"start": v(1.2, -47.86) * mm, "mid": v(3.09, -46.74) * mm, "end": v(4.2, -44.85) * mm});
            skArc(sketch, "E17.6.11.2", {"start": v(4.53, -44.85) * mm, "mid": v(4.37, -44.85) * mm, "end": v(4.2, -44.85) * mm});
            skArc(sketch, "E17.6.11.3", {"start": v(1.2, -47.86) * mm, "mid": v(1.2, -48.02) * mm, "end": v(1.2, -48.19) * mm});
            skArc(sketch, "E17.6.11.4", {"start": v(4.2, -51.2) * mm, "mid": v(3.09, -49.3) * mm, "end": v(1.2, -48.19) * mm});
            skArc(sketch, "E17.6.11.5", {"start": v(7.54, -48.19) * mm, "mid": v(5.64, -49.3) * mm, "end": v(4.53, -51.2) * mm});
            skArc(sketch, "E17.6.11.6", {"start": v(4.2, -51.2) * mm, "mid": v(4.37, -51.2) * mm, "end": v(4.53, -51.2) * mm});
            skArc(sketch, "E17.6.11.7", {"start": v(7.54, -48.19) * mm, "mid": v(7.54, -48.02) * mm, "end": v(7.54, -47.86) * mm});
            skArc(sketch, "E17.7.0.0", {"start": v(13.26, 51.2) * mm, "mid": v(14.38, 49.3) * mm, "end": v(16.27, 48.19) * mm});
            skArc(sketch, "E17.7.0.1", {"start": v(9.93, 48.19) * mm, "mid": v(11.82, 49.3) * mm, "end": v(12.93, 51.2) * mm});
            skArc(sketch, "E17.7.0.2", {"start": v(13.26, 51.2) * mm, "mid": v(13.1, 51.2) * mm, "end": v(12.93, 51.2) * mm});
            skArc(sketch, "E17.7.0.3", {"start": v(9.93, 48.19) * mm, "mid": v(9.92, 48.02) * mm, "end": v(9.93, 47.86) * mm});
            skArc(sketch, "E17.7.0.4", {"start": v(12.93, 44.85) * mm, "mid": v(11.82, 46.74) * mm, "end": v(9.93, 47.86) * mm});
            skArc(sketch, "E17.7.0.5", {"start": v(16.27, 47.86) * mm, "mid": v(14.38, 46.74) * mm, "end": v(13.26, 44.85) * mm});
            skArc(sketch, "E17.7.0.6", {"start": v(12.93, 44.85) * mm, "mid": v(13.1, 44.85) * mm, "end": v(13.26, 44.85) * mm});
            skArc(sketch, "E17.7.0.7", {"start": v(16.27, 47.86) * mm, "mid": v(16.27, 48.02) * mm, "end": v(16.27, 48.19) * mm});
            skArc(sketch, "E17.7.1.0", {"start": v(13.26, 42.46) * mm, "mid": v(14.38, 40.57) * mm, "end": v(16.27, 39.46) * mm});
            skArc(sketch, "E17.7.1.1", {"start": v(9.93, 39.46) * mm, "mid": v(11.82, 40.57) * mm, "end": v(12.93, 42.46) * mm});
            skArc(sketch, "E17.7.1.2", {"start": v(13.26, 42.46) * mm, "mid": v(13.1, 42.47) * mm, "end": v(12.93, 42.46) * mm});
            skArc(sketch, "E17.7.1.3", {"start": v(9.93, 39.46) * mm, "mid": v(9.92, 39.3) * mm, "end": v(9.93, 39.12) * mm});
            skArc(sketch, "E17.7.1.4", {"start": v(12.93, 36.12) * mm, "mid": v(11.82, 38.01) * mm, "end": v(9.93, 39.12) * mm});
            skArc(sketch, "E17.7.1.5", {"start": v(16.27, 39.12) * mm, "mid": v(14.38, 38.01) * mm, "end": v(13.26, 36.12) * mm});
            skArc(sketch, "E17.7.1.6", {"start": v(12.93, 36.12) * mm, "mid": v(13.1, 36.12) * mm, "end": v(13.26, 36.12) * mm});
            skArc(sketch, "E17.7.1.7", {"start": v(16.27, 39.12) * mm, "mid": v(16.27, 39.3) * mm, "end": v(16.27, 39.46) * mm});
            skArc(sketch, "E17.7.2.0", {"start": v(13.26, 33.73) * mm, "mid": v(14.38, 31.84) * mm, "end": v(16.27, 30.73) * mm});
            skArc(sketch, "E17.7.2.1", {"start": v(9.93, 30.73) * mm, "mid": v(11.82, 31.84) * mm, "end": v(12.93, 33.73) * mm});
            skArc(sketch, "E17.7.2.2", {"start": v(13.26, 33.73) * mm, "mid": v(13.1, 33.73) * mm, "end": v(12.93, 33.73) * mm});
            skArc(sketch, "E17.7.2.3", {"start": v(9.93, 30.73) * mm, "mid": v(9.92, 30.56) * mm, "end": v(9.93, 30.4) * mm});
            skArc(sketch, "E17.7.2.4", {"start": v(12.93, 27.39) * mm, "mid": v(11.82, 29.28) * mm, "end": v(9.93, 30.4) * mm});
            skArc(sketch, "E17.7.2.5", {"start": v(16.27, 30.4) * mm, "mid": v(14.38, 29.28) * mm, "end": v(13.26, 27.39) * mm});
            skArc(sketch, "E17.7.2.6", {"start": v(12.93, 27.39) * mm, "mid": v(13.1, 27.38) * mm, "end": v(13.26, 27.39) * mm});
            skArc(sketch, "E17.7.2.7", {"start": v(16.27, 30.4) * mm, "mid": v(16.27, 30.56) * mm, "end": v(16.27, 30.73) * mm});
            skArc(sketch, "E17.7.3.0", {"start": v(13.26, 25) * mm, "mid": v(14.38, 23.1) * mm, "end": v(16.27, 22) * mm});
            skArc(sketch, "E17.7.3.1", {"start": v(9.93, 22) * mm, "mid": v(11.82, 23.1) * mm, "end": v(12.93, 25) * mm});
            skArc(sketch, "E17.7.3.2", {"start": v(13.26, 25) * mm, "mid": v(13.1, 25) * mm, "end": v(12.93, 25) * mm});
            skArc(sketch, "E17.7.3.3", {"start": v(9.93, 22) * mm, "mid": v(9.92, 21.83) * mm, "end": v(9.93, 21.66) * mm});
            skArc(sketch, "E17.7.3.4", {"start": v(12.93, 18.66) * mm, "mid": v(11.82, 20.55) * mm, "end": v(9.93, 21.66) * mm});
            skArc(sketch, "E17.7.3.5", {"start": v(16.27, 21.66) * mm, "mid": v(14.38, 20.55) * mm, "end": v(13.26, 18.66) * mm});
            skArc(sketch, "E17.7.3.6", {"start": v(12.93, 18.66) * mm, "mid": v(13.1, 18.65) * mm, "end": v(13.26, 18.66) * mm});
            skArc(sketch, "E17.7.3.7", {"start": v(16.27, 21.66) * mm, "mid": v(16.27, 21.83) * mm, "end": v(16.27, 22) * mm});
            skArc(sketch, "E17.7.4.0", {"start": v(13.26, 16.27) * mm, "mid": v(14.38, 14.38) * mm, "end": v(16.27, 13.26) * mm});
            skArc(sketch, "E17.7.4.1", {"start": v(9.93, 13.26) * mm, "mid": v(11.82, 14.38) * mm, "end": v(12.93, 16.27) * mm});
            skArc(sketch, "E17.7.4.2", {"start": v(13.26, 16.27) * mm, "mid": v(13.1, 16.27) * mm, "end": v(12.93, 16.27) * mm});
            skArc(sketch, "E17.7.4.3", {"start": v(9.93, 13.26) * mm, "mid": v(9.92, 13.1) * mm, "end": v(9.93, 12.93) * mm});
            skArc(sketch, "E17.7.4.4", {"start": v(12.93, 9.93) * mm, "mid": v(11.82, 11.82) * mm, "end": v(9.93, 12.93) * mm});
            skArc(sketch, "E17.7.4.5", {"start": v(16.27, 12.93) * mm, "mid": v(14.38, 11.82) * mm, "end": v(13.26, 9.93) * mm});
            skArc(sketch, "E17.7.4.6", {"start": v(12.93, 9.93) * mm, "mid": v(13.1, 9.92) * mm, "end": v(13.26, 9.93) * mm});
            skArc(sketch, "E17.7.4.7", {"start": v(16.27, 12.93) * mm, "mid": v(16.27, 13.1) * mm, "end": v(16.27, 13.26) * mm});
            skArc(sketch, "E17.7.5.0", {"start": v(13.26, 7.54) * mm, "mid": v(14.38, 5.64) * mm, "end": v(16.27, 4.53) * mm});
            skArc(sketch, "E17.7.5.1", {"start": v(9.93, 4.53) * mm, "mid": v(11.82, 5.64) * mm, "end": v(12.93, 7.54) * mm});
            skArc(sketch, "E17.7.5.2", {"start": v(13.26, 7.54) * mm, "mid": v(13.1, 7.54) * mm, "end": v(12.93, 7.54) * mm});
            skArc(sketch, "E17.7.5.3", {"start": v(9.93, 4.53) * mm, "mid": v(9.92, 4.37) * mm, "end": v(9.93, 4.2) * mm});
            skArc(sketch, "E17.7.5.4", {"start": v(12.93, 1.2) * mm, "mid": v(11.82, 3.09) * mm, "end": v(9.93, 4.2) * mm});
            skArc(sketch, "E17.7.5.5", {"start": v(16.27, 4.2) * mm, "mid": v(14.38, 3.09) * mm, "end": v(13.26, 1.2) * mm});
            skArc(sketch, "E17.7.5.6", {"start": v(12.93, 1.2) * mm, "mid": v(13.1, 1.2) * mm, "end": v(13.26, 1.2) * mm});
            skArc(sketch, "E17.7.5.7", {"start": v(16.27, 4.2) * mm, "mid": v(16.27, 4.37) * mm, "end": v(16.27, 4.53) * mm});
            skArc(sketch, "E17.7.6.0", {"start": v(13.26, -1.2) * mm, "mid": v(14.38, -3.09) * mm, "end": v(16.27, -4.2) * mm});
            skArc(sketch, "E17.7.6.1", {"start": v(9.93, -4.2) * mm, "mid": v(11.82, -3.09) * mm, "end": v(12.93, -1.2) * mm});
            skArc(sketch, "E17.7.6.2", {"start": v(13.26, -1.2) * mm, "mid": v(13.1, -1.2) * mm, "end": v(12.93, -1.2) * mm});
            skArc(sketch, "E17.7.6.3", {"start": v(9.93, -4.2) * mm, "mid": v(9.92, -4.37) * mm, "end": v(9.93, -4.53) * mm});
            skArc(sketch, "E17.7.6.4", {"start": v(12.93, -7.54) * mm, "mid": v(11.82, -5.64) * mm, "end": v(9.93, -4.53) * mm});
            skArc(sketch, "E17.7.6.5", {"start": v(16.27, -4.53) * mm, "mid": v(14.38, -5.64) * mm, "end": v(13.26, -7.54) * mm});
            skArc(sketch, "E17.7.6.6", {"start": v(12.93, -7.54) * mm, "mid": v(13.1, -7.54) * mm, "end": v(13.26, -7.54) * mm});
            skArc(sketch, "E17.7.6.7", {"start": v(16.27, -4.53) * mm, "mid": v(16.27, -4.37) * mm, "end": v(16.27, -4.2) * mm});
            skArc(sketch, "E17.7.7.0", {"start": v(13.26, -9.93) * mm, "mid": v(14.38, -11.82) * mm, "end": v(16.27, -12.93) * mm});
            skArc(sketch, "E17.7.7.1", {"start": v(9.93, -12.93) * mm, "mid": v(11.82, -11.82) * mm, "end": v(12.93, -9.93) * mm});
            skArc(sketch, "E17.7.7.2", {"start": v(13.26, -9.93) * mm, "mid": v(13.1, -9.92) * mm, "end": v(12.93, -9.93) * mm});
            skArc(sketch, "E17.7.7.3", {"start": v(9.93, -12.93) * mm, "mid": v(9.92, -13.1) * mm, "end": v(9.93, -13.26) * mm});
            skArc(sketch, "E17.7.7.4", {"start": v(12.93, -16.27) * mm, "mid": v(11.82, -14.38) * mm, "end": v(9.93, -13.26) * mm});
            skArc(sketch, "E17.7.7.5", {"start": v(16.27, -13.26) * mm, "mid": v(14.38, -14.38) * mm, "end": v(13.26, -16.27) * mm});
            skArc(sketch, "E17.7.7.6", {"start": v(12.93, -16.27) * mm, "mid": v(13.1, -16.27) * mm, "end": v(13.26, -16.27) * mm});
            skArc(sketch, "E17.7.7.7", {"start": v(16.27, -13.26) * mm, "mid": v(16.27, -13.1) * mm, "end": v(16.27, -12.93) * mm});
            skArc(sketch, "E17.7.8.0", {"start": v(13.26, -18.66) * mm, "mid": v(14.38, -20.55) * mm, "end": v(16.27, -21.66) * mm});
            skArc(sketch, "E17.7.8.1", {"start": v(9.93, -21.66) * mm, "mid": v(11.82, -20.55) * mm, "end": v(12.93, -18.66) * mm});
            skArc(sketch, "E17.7.8.2", {"start": v(13.26, -18.66) * mm, "mid": v(13.1, -18.65) * mm, "end": v(12.93, -18.66) * mm});
            skArc(sketch, "E17.7.8.3", {"start": v(9.93, -21.66) * mm, "mid": v(9.92, -21.83) * mm, "end": v(9.93, -22) * mm});
            skArc(sketch, "E17.7.8.4", {"start": v(12.93, -25) * mm, "mid": v(11.82, -23.1) * mm, "end": v(9.93, -22) * mm});
            skArc(sketch, "E17.7.8.5", {"start": v(16.27, -22) * mm, "mid": v(14.38, -23.1) * mm, "end": v(13.26, -25) * mm});
            skArc(sketch, "E17.7.8.6", {"start": v(12.93, -25) * mm, "mid": v(13.1, -25) * mm, "end": v(13.26, -25) * mm});
            skArc(sketch, "E17.7.8.7", {"start": v(16.27, -22) * mm, "mid": v(16.27, -21.83) * mm, "end": v(16.27, -21.66) * mm});
            skArc(sketch, "E17.7.9.0", {"start": v(13.26, -27.39) * mm, "mid": v(14.38, -29.28) * mm, "end": v(16.27, -30.4) * mm});
            skArc(sketch, "E17.7.9.1", {"start": v(9.93, -30.4) * mm, "mid": v(11.82, -29.28) * mm, "end": v(12.93, -27.39) * mm});
            skArc(sketch, "E17.7.9.2", {"start": v(13.26, -27.39) * mm, "mid": v(13.1, -27.38) * mm, "end": v(12.93, -27.39) * mm});
            skArc(sketch, "E17.7.9.3", {"start": v(9.93, -30.4) * mm, "mid": v(9.92, -30.56) * mm, "end": v(9.93, -30.73) * mm});
            skArc(sketch, "E17.7.9.4", {"start": v(12.93, -33.73) * mm, "mid": v(11.82, -31.84) * mm, "end": v(9.93, -30.73) * mm});
            skArc(sketch, "E17.7.9.5", {"start": v(16.27, -30.73) * mm, "mid": v(14.38, -31.84) * mm, "end": v(13.26, -33.73) * mm});
            skArc(sketch, "E17.7.9.6", {"start": v(12.93, -33.73) * mm, "mid": v(13.1, -33.73) * mm, "end": v(13.26, -33.73) * mm});
            skArc(sketch, "E17.7.9.7", {"start": v(16.27, -30.73) * mm, "mid": v(16.27, -30.56) * mm, "end": v(16.27, -30.4) * mm});
            skArc(sketch, "E17.7.10.0", {"start": v(13.26, -36.12) * mm, "mid": v(14.38, -38.01) * mm, "end": v(16.27, -39.12) * mm});
            skArc(sketch, "E17.7.10.1", {"start": v(9.93, -39.12) * mm, "mid": v(11.82, -38.01) * mm, "end": v(12.93, -36.12) * mm});
            skArc(sketch, "E17.7.10.2", {"start": v(13.26, -36.12) * mm, "mid": v(13.1, -36.12) * mm, "end": v(12.93, -36.12) * mm});
            skArc(sketch, "E17.7.10.3", {"start": v(9.93, -39.12) * mm, "mid": v(9.92, -39.3) * mm, "end": v(9.93, -39.46) * mm});
            skArc(sketch, "E17.7.10.4", {"start": v(12.93, -42.46) * mm, "mid": v(11.82, -40.57) * mm, "end": v(9.93, -39.46) * mm});
            skArc(sketch, "E17.7.10.5", {"start": v(16.27, -39.46) * mm, "mid": v(14.38, -40.57) * mm, "end": v(13.26, -42.46) * mm});
            skArc(sketch, "E17.7.10.6", {"start": v(12.93, -42.46) * mm, "mid": v(13.1, -42.47) * mm, "end": v(13.26, -42.46) * mm});
            skArc(sketch, "E17.7.10.7", {"start": v(16.27, -39.46) * mm, "mid": v(16.27, -39.3) * mm, "end": v(16.27, -39.12) * mm});
            skArc(sketch, "E17.7.11.0", {"start": v(13.26, -44.85) * mm, "mid": v(14.38, -46.74) * mm, "end": v(16.27, -47.86) * mm});
            skArc(sketch, "E17.7.11.1", {"start": v(9.93, -47.86) * mm, "mid": v(11.82, -46.74) * mm, "end": v(12.93, -44.85) * mm});
            skArc(sketch, "E17.7.11.2", {"start": v(13.26, -44.85) * mm, "mid": v(13.1, -44.85) * mm, "end": v(12.93, -44.85) * mm});
            skArc(sketch, "E17.7.11.3", {"start": v(9.93, -47.86) * mm, "mid": v(9.92, -48.02) * mm, "end": v(9.93, -48.19) * mm});
            skArc(sketch, "E17.7.11.4", {"start": v(12.93, -51.2) * mm, "mid": v(11.82, -49.3) * mm, "end": v(9.93, -48.19) * mm});
            skArc(sketch, "E17.7.11.5", {"start": v(16.27, -48.19) * mm, "mid": v(14.38, -49.3) * mm, "end": v(13.26, -51.2) * mm});
            skArc(sketch, "E17.7.11.6", {"start": v(12.93, -51.2) * mm, "mid": v(13.1, -51.2) * mm, "end": v(13.26, -51.2) * mm});
            skArc(sketch, "E17.7.11.7", {"start": v(16.27, -48.19) * mm, "mid": v(16.27, -48.02) * mm, "end": v(16.27, -47.86) * mm});
            skArc(sketch, "E17.8.0.0", {"start": v(22, 51.2) * mm, "mid": v(23.1, 49.3) * mm, "end": v(25, 48.19) * mm});
            skArc(sketch, "E17.8.0.1", {"start": v(18.66, 48.19) * mm, "mid": v(20.55, 49.3) * mm, "end": v(21.66, 51.2) * mm});
            skArc(sketch, "E17.8.0.2", {"start": v(22, 51.2) * mm, "mid": v(21.83, 51.2) * mm, "end": v(21.66, 51.2) * mm});
            skArc(sketch, "E17.8.0.3", {"start": v(18.66, 48.19) * mm, "mid": v(18.65, 48.02) * mm, "end": v(18.66, 47.86) * mm});
            skArc(sketch, "E17.8.0.4", {"start": v(21.66, 44.85) * mm, "mid": v(20.55, 46.74) * mm, "end": v(18.66, 47.86) * mm});
            skArc(sketch, "E17.8.0.5", {"start": v(25, 47.86) * mm, "mid": v(23.1, 46.74) * mm, "end": v(22, 44.85) * mm});
            skArc(sketch, "E17.8.0.6", {"start": v(21.66, 44.85) * mm, "mid": v(21.83, 44.85) * mm, "end": v(22, 44.85) * mm});
            skArc(sketch, "E17.8.0.7", {"start": v(25, 47.86) * mm, "mid": v(25, 48.02) * mm, "end": v(25, 48.19) * mm});
            skArc(sketch, "E17.8.1.0", {"start": v(22, 42.46) * mm, "mid": v(23.1, 40.57) * mm, "end": v(25, 39.46) * mm});
            skArc(sketch, "E17.8.1.1", {"start": v(18.66, 39.46) * mm, "mid": v(20.55, 40.57) * mm, "end": v(21.66, 42.46) * mm});
            skArc(sketch, "E17.8.1.2", {"start": v(22, 42.46) * mm, "mid": v(21.83, 42.47) * mm, "end": v(21.66, 42.46) * mm});
            skArc(sketch, "E17.8.1.3", {"start": v(18.66, 39.46) * mm, "mid": v(18.65, 39.3) * mm, "end": v(18.66, 39.12) * mm});
            skArc(sketch, "E17.8.1.4", {"start": v(21.66, 36.12) * mm, "mid": v(20.55, 38.01) * mm, "end": v(18.66, 39.12) * mm});
            skArc(sketch, "E17.8.1.5", {"start": v(25, 39.12) * mm, "mid": v(23.1, 38.01) * mm, "end": v(22, 36.12) * mm});
            skArc(sketch, "E17.8.1.6", {"start": v(21.66, 36.12) * mm, "mid": v(21.83, 36.12) * mm, "end": v(22, 36.12) * mm});
            skArc(sketch, "E17.8.1.7", {"start": v(25, 39.12) * mm, "mid": v(25, 39.3) * mm, "end": v(25, 39.46) * mm});
            skArc(sketch, "E17.8.2.0", {"start": v(22, 33.73) * mm, "mid": v(23.1, 31.84) * mm, "end": v(25, 30.73) * mm});
            skArc(sketch, "E17.8.2.1", {"start": v(18.66, 30.73) * mm, "mid": v(20.55, 31.84) * mm, "end": v(21.66, 33.73) * mm});
            skArc(sketch, "E17.8.2.2", {"start": v(22, 33.73) * mm, "mid": v(21.83, 33.73) * mm, "end": v(21.66, 33.73) * mm});
            skArc(sketch, "E17.8.2.3", {"start": v(18.66, 30.73) * mm, "mid": v(18.65, 30.56) * mm, "end": v(18.66, 30.4) * mm});
            skArc(sketch, "E17.8.2.4", {"start": v(21.66, 27.39) * mm, "mid": v(20.55, 29.28) * mm, "end": v(18.66, 30.4) * mm});
            skArc(sketch, "E17.8.2.5", {"start": v(25, 30.4) * mm, "mid": v(23.1, 29.28) * mm, "end": v(22, 27.39) * mm});
            skArc(sketch, "E17.8.2.6", {"start": v(21.66, 27.39) * mm, "mid": v(21.83, 27.38) * mm, "end": v(22, 27.39) * mm});
            skArc(sketch, "E17.8.2.7", {"start": v(25, 30.4) * mm, "mid": v(25, 30.56) * mm, "end": v(25, 30.73) * mm});
            skArc(sketch, "E17.8.3.0", {"start": v(22, 25) * mm, "mid": v(23.1, 23.1) * mm, "end": v(25, 22) * mm});
            skArc(sketch, "E17.8.3.1", {"start": v(18.66, 22) * mm, "mid": v(20.55, 23.1) * mm, "end": v(21.66, 25) * mm});
            skArc(sketch, "E17.8.3.2", {"start": v(22, 25) * mm, "mid": v(21.83, 25) * mm, "end": v(21.66, 25) * mm});
            skArc(sketch, "E17.8.3.3", {"start": v(18.66, 22) * mm, "mid": v(18.65, 21.83) * mm, "end": v(18.66, 21.66) * mm});
            skArc(sketch, "E17.8.3.4", {"start": v(21.66, 18.66) * mm, "mid": v(20.55, 20.55) * mm, "end": v(18.66, 21.66) * mm});
            skArc(sketch, "E17.8.3.5", {"start": v(25, 21.66) * mm, "mid": v(23.1, 20.55) * mm, "end": v(22, 18.66) * mm});
            skArc(sketch, "E17.8.3.6", {"start": v(21.66, 18.66) * mm, "mid": v(21.83, 18.65) * mm, "end": v(22, 18.66) * mm});
            skArc(sketch, "E17.8.3.7", {"start": v(25, 21.66) * mm, "mid": v(25, 21.83) * mm, "end": v(25, 22) * mm});
            skArc(sketch, "E17.8.4.0", {"start": v(22, 16.27) * mm, "mid": v(23.1, 14.38) * mm, "end": v(25, 13.26) * mm});
            skArc(sketch, "E17.8.4.1", {"start": v(18.66, 13.26) * mm, "mid": v(20.55, 14.38) * mm, "end": v(21.66, 16.27) * mm});
            skArc(sketch, "E17.8.4.2", {"start": v(22, 16.27) * mm, "mid": v(21.83, 16.27) * mm, "end": v(21.66, 16.27) * mm});
            skArc(sketch, "E17.8.4.3", {"start": v(18.66, 13.26) * mm, "mid": v(18.65, 13.1) * mm, "end": v(18.66, 12.93) * mm});
            skArc(sketch, "E17.8.4.4", {"start": v(21.66, 9.93) * mm, "mid": v(20.55, 11.82) * mm, "end": v(18.66, 12.93) * mm});
            skArc(sketch, "E17.8.4.5", {"start": v(25, 12.93) * mm, "mid": v(23.1, 11.82) * mm, "end": v(22, 9.93) * mm});
            skArc(sketch, "E17.8.4.6", {"start": v(21.66, 9.93) * mm, "mid": v(21.83, 9.92) * mm, "end": v(22, 9.93) * mm});
            skArc(sketch, "E17.8.4.7", {"start": v(25, 12.93) * mm, "mid": v(25, 13.1) * mm, "end": v(25, 13.26) * mm});
            skArc(sketch, "E17.8.5.0", {"start": v(22, 7.54) * mm, "mid": v(23.1, 5.64) * mm, "end": v(25, 4.53) * mm});
            skArc(sketch, "E17.8.5.1", {"start": v(18.66, 4.53) * mm, "mid": v(20.55, 5.64) * mm, "end": v(21.66, 7.54) * mm});
            skArc(sketch, "E17.8.5.2", {"start": v(22, 7.54) * mm, "mid": v(21.83, 7.54) * mm, "end": v(21.66, 7.54) * mm});
            skArc(sketch, "E17.8.5.3", {"start": v(18.66, 4.53) * mm, "mid": v(18.65, 4.37) * mm, "end": v(18.66, 4.2) * mm});
            skArc(sketch, "E17.8.5.4", {"start": v(21.66, 1.2) * mm, "mid": v(20.55, 3.09) * mm, "end": v(18.66, 4.2) * mm});
            skArc(sketch, "E17.8.5.5", {"start": v(25, 4.2) * mm, "mid": v(23.1, 3.09) * mm, "end": v(22, 1.2) * mm});
            skArc(sketch, "E17.8.5.6", {"start": v(21.66, 1.2) * mm, "mid": v(21.83, 1.2) * mm, "end": v(22, 1.2) * mm});
            skArc(sketch, "E17.8.5.7", {"start": v(25, 4.2) * mm, "mid": v(25, 4.37) * mm, "end": v(25, 4.53) * mm});
            skArc(sketch, "E17.8.6.0", {"start": v(22, -1.2) * mm, "mid": v(23.1, -3.09) * mm, "end": v(25, -4.2) * mm});
            skArc(sketch, "E17.8.6.1", {"start": v(18.66, -4.2) * mm, "mid": v(20.55, -3.09) * mm, "end": v(21.66, -1.2) * mm});
            skArc(sketch, "E17.8.6.2", {"start": v(22, -1.2) * mm, "mid": v(21.83, -1.2) * mm, "end": v(21.66, -1.2) * mm});
            skArc(sketch, "E17.8.6.3", {"start": v(18.66, -4.2) * mm, "mid": v(18.65, -4.37) * mm, "end": v(18.66, -4.53) * mm});
            skArc(sketch, "E17.8.6.4", {"start": v(21.66, -7.54) * mm, "mid": v(20.55, -5.64) * mm, "end": v(18.66, -4.53) * mm});
            skArc(sketch, "E17.8.6.5", {"start": v(25, -4.53) * mm, "mid": v(23.1, -5.64) * mm, "end": v(22, -7.54) * mm});
            skArc(sketch, "E17.8.6.6", {"start": v(21.66, -7.54) * mm, "mid": v(21.83, -7.54) * mm, "end": v(22, -7.54) * mm});
            skArc(sketch, "E17.8.6.7", {"start": v(25, -4.53) * mm, "mid": v(25, -4.37) * mm, "end": v(25, -4.2) * mm});
            skArc(sketch, "E17.8.7.0", {"start": v(22, -9.93) * mm, "mid": v(23.1, -11.82) * mm, "end": v(25, -12.93) * mm});
            skArc(sketch, "E17.8.7.1", {"start": v(18.66, -12.93) * mm, "mid": v(20.55, -11.82) * mm, "end": v(21.66, -9.93) * mm});
            skArc(sketch, "E17.8.7.2", {"start": v(22, -9.93) * mm, "mid": v(21.83, -9.92) * mm, "end": v(21.66, -9.93) * mm});
            skArc(sketch, "E17.8.7.3", {"start": v(18.66, -12.93) * mm, "mid": v(18.65, -13.1) * mm, "end": v(18.66, -13.26) * mm});
            skArc(sketch, "E17.8.7.4", {"start": v(21.66, -16.27) * mm, "mid": v(20.55, -14.38) * mm, "end": v(18.66, -13.26) * mm});
            skArc(sketch, "E17.8.7.5", {"start": v(25, -13.26) * mm, "mid": v(23.1, -14.38) * mm, "end": v(22, -16.27) * mm});
            skArc(sketch, "E17.8.7.6", {"start": v(21.66, -16.27) * mm, "mid": v(21.83, -16.27) * mm, "end": v(22, -16.27) * mm});
            skArc(sketch, "E17.8.7.7", {"start": v(25, -13.26) * mm, "mid": v(25, -13.1) * mm, "end": v(25, -12.93) * mm});
            skArc(sketch, "E17.8.8.0", {"start": v(22, -18.66) * mm, "mid": v(23.1, -20.55) * mm, "end": v(25, -21.66) * mm});
            skArc(sketch, "E17.8.8.1", {"start": v(18.66, -21.66) * mm, "mid": v(20.55, -20.55) * mm, "end": v(21.66, -18.66) * mm});
            skArc(sketch, "E17.8.8.2", {"start": v(22, -18.66) * mm, "mid": v(21.83, -18.65) * mm, "end": v(21.66, -18.66) * mm});
            skArc(sketch, "E17.8.8.3", {"start": v(18.66, -21.66) * mm, "mid": v(18.65, -21.83) * mm, "end": v(18.66, -22) * mm});
            skArc(sketch, "E17.8.8.4", {"start": v(21.66, -25) * mm, "mid": v(20.55, -23.1) * mm, "end": v(18.66, -22) * mm});
            skArc(sketch, "E17.8.8.5", {"start": v(25, -22) * mm, "mid": v(23.1, -23.1) * mm, "end": v(22, -25) * mm});
            skArc(sketch, "E17.8.8.6", {"start": v(21.66, -25) * mm, "mid": v(21.83, -25) * mm, "end": v(22, -25) * mm});
            skArc(sketch, "E17.8.8.7", {"start": v(25, -22) * mm, "mid": v(25, -21.83) * mm, "end": v(25, -21.66) * mm});
            skArc(sketch, "E17.8.9.0", {"start": v(22, -27.39) * mm, "mid": v(23.1, -29.28) * mm, "end": v(25, -30.4) * mm});
            skArc(sketch, "E17.8.9.1", {"start": v(18.66, -30.4) * mm, "mid": v(20.55, -29.28) * mm, "end": v(21.66, -27.39) * mm});
            skArc(sketch, "E17.8.9.2", {"start": v(22, -27.39) * mm, "mid": v(21.83, -27.38) * mm, "end": v(21.66, -27.39) * mm});
            skArc(sketch, "E17.8.9.3", {"start": v(18.66, -30.4) * mm, "mid": v(18.65, -30.56) * mm, "end": v(18.66, -30.73) * mm});
            skArc(sketch, "E17.8.9.4", {"start": v(21.66, -33.73) * mm, "mid": v(20.55, -31.84) * mm, "end": v(18.66, -30.73) * mm});
            skArc(sketch, "E17.8.9.5", {"start": v(25, -30.73) * mm, "mid": v(23.1, -31.84) * mm, "end": v(22, -33.73) * mm});
            skArc(sketch, "E17.8.9.6", {"start": v(21.66, -33.73) * mm, "mid": v(21.83, -33.73) * mm, "end": v(22, -33.73) * mm});
            skArc(sketch, "E17.8.9.7", {"start": v(25, -30.73) * mm, "mid": v(25, -30.56) * mm, "end": v(25, -30.4) * mm});
            skArc(sketch, "E17.8.10.0", {"start": v(22, -36.12) * mm, "mid": v(23.1, -38.01) * mm, "end": v(25, -39.12) * mm});
            skArc(sketch, "E17.8.10.1", {"start": v(18.66, -39.12) * mm, "mid": v(20.55, -38.01) * mm, "end": v(21.66, -36.12) * mm});
            skArc(sketch, "E17.8.10.2", {"start": v(22, -36.12) * mm, "mid": v(21.83, -36.12) * mm, "end": v(21.66, -36.12) * mm});
            skArc(sketch, "E17.8.10.3", {"start": v(18.66, -39.12) * mm, "mid": v(18.65, -39.3) * mm, "end": v(18.66, -39.46) * mm});
            skArc(sketch, "E17.8.10.4", {"start": v(21.66, -42.46) * mm, "mid": v(20.55, -40.57) * mm, "end": v(18.66, -39.46) * mm});
            skArc(sketch, "E17.8.10.5", {"start": v(25, -39.46) * mm, "mid": v(23.1, -40.57) * mm, "end": v(22, -42.46) * mm});
            skArc(sketch, "E17.8.10.6", {"start": v(21.66, -42.46) * mm, "mid": v(21.83, -42.47) * mm, "end": v(22, -42.46) * mm});
            skArc(sketch, "E17.8.10.7", {"start": v(25, -39.46) * mm, "mid": v(25, -39.3) * mm, "end": v(25, -39.12) * mm});
            skArc(sketch, "E17.8.11.0", {"start": v(22, -44.85) * mm, "mid": v(23.1, -46.74) * mm, "end": v(25, -47.86) * mm});
            skArc(sketch, "E17.8.11.1", {"start": v(18.66, -47.86) * mm, "mid": v(20.55, -46.74) * mm, "end": v(21.66, -44.85) * mm});
            skArc(sketch, "E17.8.11.2", {"start": v(22, -44.85) * mm, "mid": v(21.83, -44.85) * mm, "end": v(21.66, -44.85) * mm});
            skArc(sketch, "E17.8.11.3", {"start": v(18.66, -47.86) * mm, "mid": v(18.65, -48.02) * mm, "end": v(18.66, -48.19) * mm});
            skArc(sketch, "E17.8.11.4", {"start": v(21.66, -51.2) * mm, "mid": v(20.55, -49.3) * mm, "end": v(18.66, -48.19) * mm});
            skArc(sketch, "E17.8.11.5", {"start": v(25, -48.19) * mm, "mid": v(23.1, -49.3) * mm, "end": v(22, -51.2) * mm});
            skArc(sketch, "E17.8.11.6", {"start": v(21.66, -51.2) * mm, "mid": v(21.83, -51.2) * mm, "end": v(22, -51.2) * mm});
            skArc(sketch, "E17.8.11.7", {"start": v(25, -48.19) * mm, "mid": v(25, -48.02) * mm, "end": v(25, -47.86) * mm});
            skArc(sketch, "E17.9.0.0", {"start": v(30.73, 51.2) * mm, "mid": v(31.84, 49.3) * mm, "end": v(33.73, 48.19) * mm});
            skArc(sketch, "E17.9.0.1", {"start": v(27.39, 48.19) * mm, "mid": v(29.28, 49.3) * mm, "end": v(30.4, 51.2) * mm});
            skArc(sketch, "E17.9.0.2", {"start": v(30.73, 51.2) * mm, "mid": v(30.56, 51.2) * mm, "end": v(30.4, 51.2) * mm});
            skArc(sketch, "E17.9.0.3", {"start": v(27.39, 48.19) * mm, "mid": v(27.38, 48.02) * mm, "end": v(27.39, 47.86) * mm});
            skArc(sketch, "E17.9.0.4", {"start": v(30.4, 44.85) * mm, "mid": v(29.28, 46.74) * mm, "end": v(27.39, 47.86) * mm});
            skArc(sketch, "E17.9.0.5", {"start": v(33.73, 47.86) * mm, "mid": v(31.84, 46.74) * mm, "end": v(30.73, 44.85) * mm});
            skArc(sketch, "E17.9.0.6", {"start": v(30.4, 44.85) * mm, "mid": v(30.56, 44.85) * mm, "end": v(30.73, 44.85) * mm});
            skArc(sketch, "E17.9.0.7", {"start": v(33.73, 47.86) * mm, "mid": v(33.73, 48.02) * mm, "end": v(33.73, 48.19) * mm});
            skArc(sketch, "E17.9.1.0", {"start": v(30.73, 42.46) * mm, "mid": v(31.84, 40.57) * mm, "end": v(33.73, 39.46) * mm});
            skArc(sketch, "E17.9.1.1", {"start": v(27.39, 39.46) * mm, "mid": v(29.28, 40.57) * mm, "end": v(30.4, 42.46) * mm});
            skArc(sketch, "E17.9.1.2", {"start": v(30.73, 42.46) * mm, "mid": v(30.56, 42.47) * mm, "end": v(30.4, 42.46) * mm});
            skArc(sketch, "E17.9.1.3", {"start": v(27.39, 39.46) * mm, "mid": v(27.38, 39.3) * mm, "end": v(27.39, 39.12) * mm});
            skArc(sketch, "E17.9.1.4", {"start": v(30.4, 36.12) * mm, "mid": v(29.28, 38.01) * mm, "end": v(27.39, 39.12) * mm});
            skArc(sketch, "E17.9.1.5", {"start": v(33.73, 39.12) * mm, "mid": v(31.84, 38.01) * mm, "end": v(30.73, 36.12) * mm});
            skArc(sketch, "E17.9.1.6", {"start": v(30.4, 36.12) * mm, "mid": v(30.56, 36.12) * mm, "end": v(30.73, 36.12) * mm});
            skArc(sketch, "E17.9.1.7", {"start": v(33.73, 39.12) * mm, "mid": v(33.73, 39.3) * mm, "end": v(33.73, 39.46) * mm});
            skArc(sketch, "E17.9.2.0", {"start": v(30.73, 33.73) * mm, "mid": v(31.84, 31.84) * mm, "end": v(33.73, 30.73) * mm});
            skArc(sketch, "E17.9.2.1", {"start": v(27.39, 30.73) * mm, "mid": v(29.28, 31.84) * mm, "end": v(30.4, 33.73) * mm});
            skArc(sketch, "E17.9.2.2", {"start": v(30.73, 33.73) * mm, "mid": v(30.56, 33.73) * mm, "end": v(30.4, 33.73) * mm});
            skArc(sketch, "E17.9.2.3", {"start": v(27.39, 30.73) * mm, "mid": v(27.38, 30.56) * mm, "end": v(27.39, 30.4) * mm});
            skArc(sketch, "E17.9.2.4", {"start": v(30.4, 27.39) * mm, "mid": v(29.28, 29.28) * mm, "end": v(27.39, 30.4) * mm});
            skArc(sketch, "E17.9.2.5", {"start": v(33.73, 30.4) * mm, "mid": v(31.84, 29.28) * mm, "end": v(30.73, 27.39) * mm});
            skArc(sketch, "E17.9.2.6", {"start": v(30.4, 27.39) * mm, "mid": v(30.56, 27.38) * mm, "end": v(30.73, 27.39) * mm});
            skArc(sketch, "E17.9.2.7", {"start": v(33.73, 30.4) * mm, "mid": v(33.73, 30.56) * mm, "end": v(33.73, 30.73) * mm});
            skArc(sketch, "E17.9.3.0", {"start": v(30.73, 25) * mm, "mid": v(31.84, 23.1) * mm, "end": v(33.73, 22) * mm});
            skArc(sketch, "E17.9.3.1", {"start": v(27.39, 22) * mm, "mid": v(29.28, 23.1) * mm, "end": v(30.4, 25) * mm});
            skArc(sketch, "E17.9.3.2", {"start": v(30.73, 25) * mm, "mid": v(30.56, 25) * mm, "end": v(30.4, 25) * mm});
            skArc(sketch, "E17.9.3.3", {"start": v(27.39, 22) * mm, "mid": v(27.38, 21.83) * mm, "end": v(27.39, 21.66) * mm});
            skArc(sketch, "E17.9.3.4", {"start": v(30.4, 18.66) * mm, "mid": v(29.28, 20.55) * mm, "end": v(27.39, 21.66) * mm});
            skArc(sketch, "E17.9.3.5", {"start": v(33.73, 21.66) * mm, "mid": v(31.84, 20.55) * mm, "end": v(30.73, 18.66) * mm});
            skArc(sketch, "E17.9.3.6", {"start": v(30.4, 18.66) * mm, "mid": v(30.56, 18.65) * mm, "end": v(30.73, 18.66) * mm});
            skArc(sketch, "E17.9.3.7", {"start": v(33.73, 21.66) * mm, "mid": v(33.73, 21.83) * mm, "end": v(33.73, 22) * mm});
            skArc(sketch, "E17.9.4.0", {"start": v(30.73, 16.27) * mm, "mid": v(31.84, 14.38) * mm, "end": v(33.73, 13.26) * mm});
            skArc(sketch, "E17.9.4.1", {"start": v(27.39, 13.26) * mm, "mid": v(29.28, 14.38) * mm, "end": v(30.4, 16.27) * mm});
            skArc(sketch, "E17.9.4.2", {"start": v(30.73, 16.27) * mm, "mid": v(30.56, 16.27) * mm, "end": v(30.4, 16.27) * mm});
            skArc(sketch, "E17.9.4.3", {"start": v(27.39, 13.26) * mm, "mid": v(27.38, 13.1) * mm, "end": v(27.39, 12.93) * mm});
            skArc(sketch, "E17.9.4.4", {"start": v(30.4, 9.93) * mm, "mid": v(29.28, 11.82) * mm, "end": v(27.39, 12.93) * mm});
            skArc(sketch, "E17.9.4.5", {"start": v(33.73, 12.93) * mm, "mid": v(31.84, 11.82) * mm, "end": v(30.73, 9.93) * mm});
            skArc(sketch, "E17.9.4.6", {"start": v(30.4, 9.93) * mm, "mid": v(30.56, 9.92) * mm, "end": v(30.73, 9.93) * mm});
            skArc(sketch, "E17.9.4.7", {"start": v(33.73, 12.93) * mm, "mid": v(33.73, 13.1) * mm, "end": v(33.73, 13.26) * mm});
            skArc(sketch, "E17.9.5.0", {"start": v(30.73, 7.54) * mm, "mid": v(31.84, 5.64) * mm, "end": v(33.73, 4.53) * mm});
            skArc(sketch, "E17.9.5.1", {"start": v(27.39, 4.53) * mm, "mid": v(29.28, 5.64) * mm, "end": v(30.4, 7.54) * mm});
            skArc(sketch, "E17.9.5.2", {"start": v(30.73, 7.54) * mm, "mid": v(30.56, 7.54) * mm, "end": v(30.4, 7.54) * mm});
            skArc(sketch, "E17.9.5.3", {"start": v(27.39, 4.53) * mm, "mid": v(27.38, 4.37) * mm, "end": v(27.39, 4.2) * mm});
            skArc(sketch, "E17.9.5.4", {"start": v(30.4, 1.2) * mm, "mid": v(29.28, 3.09) * mm, "end": v(27.39, 4.2) * mm});
            skArc(sketch, "E17.9.5.5", {"start": v(33.73, 4.2) * mm, "mid": v(31.84, 3.09) * mm, "end": v(30.73, 1.2) * mm});
            skArc(sketch, "E17.9.5.6", {"start": v(30.4, 1.2) * mm, "mid": v(30.56, 1.2) * mm, "end": v(30.73, 1.2) * mm});
            skArc(sketch, "E17.9.5.7", {"start": v(33.73, 4.2) * mm, "mid": v(33.73, 4.37) * mm, "end": v(33.73, 4.53) * mm});
            skArc(sketch, "E17.9.6.0", {"start": v(30.73, -1.2) * mm, "mid": v(31.84, -3.09) * mm, "end": v(33.73, -4.2) * mm});
            skArc(sketch, "E17.9.6.1", {"start": v(27.39, -4.2) * mm, "mid": v(29.28, -3.09) * mm, "end": v(30.4, -1.2) * mm});
            skArc(sketch, "E17.9.6.2", {"start": v(30.73, -1.2) * mm, "mid": v(30.56, -1.2) * mm, "end": v(30.4, -1.2) * mm});
            skArc(sketch, "E17.9.6.3", {"start": v(27.39, -4.2) * mm, "mid": v(27.38, -4.37) * mm, "end": v(27.39, -4.53) * mm});
            skArc(sketch, "E17.9.6.4", {"start": v(30.4, -7.54) * mm, "mid": v(29.28, -5.64) * mm, "end": v(27.39, -4.53) * mm});
            skArc(sketch, "E17.9.6.5", {"start": v(33.73, -4.53) * mm, "mid": v(31.84, -5.64) * mm, "end": v(30.73, -7.54) * mm});
            skArc(sketch, "E17.9.6.6", {"start": v(30.4, -7.54) * mm, "mid": v(30.56, -7.54) * mm, "end": v(30.73, -7.54) * mm});
            skArc(sketch, "E17.9.6.7", {"start": v(33.73, -4.53) * mm, "mid": v(33.73, -4.37) * mm, "end": v(33.73, -4.2) * mm});
            skArc(sketch, "E17.9.7.0", {"start": v(30.73, -9.93) * mm, "mid": v(31.84, -11.82) * mm, "end": v(33.73, -12.93) * mm});
            skArc(sketch, "E17.9.7.1", {"start": v(27.39, -12.93) * mm, "mid": v(29.28, -11.82) * mm, "end": v(30.4, -9.93) * mm});
            skArc(sketch, "E17.9.7.2", {"start": v(30.73, -9.93) * mm, "mid": v(30.56, -9.92) * mm, "end": v(30.4, -9.93) * mm});
            skArc(sketch, "E17.9.7.3", {"start": v(27.39, -12.93) * mm, "mid": v(27.38, -13.1) * mm, "end": v(27.39, -13.26) * mm});
            skArc(sketch, "E17.9.7.4", {"start": v(30.4, -16.27) * mm, "mid": v(29.28, -14.38) * mm, "end": v(27.39, -13.26) * mm});
            skArc(sketch, "E17.9.7.5", {"start": v(33.73, -13.26) * mm, "mid": v(31.84, -14.38) * mm, "end": v(30.73, -16.27) * mm});
            skArc(sketch, "E17.9.7.6", {"start": v(30.4, -16.27) * mm, "mid": v(30.56, -16.27) * mm, "end": v(30.73, -16.27) * mm});
            skArc(sketch, "E17.9.7.7", {"start": v(33.73, -13.26) * mm, "mid": v(33.73, -13.1) * mm, "end": v(33.73, -12.93) * mm});
            skArc(sketch, "E17.9.8.0", {"start": v(30.73, -18.66) * mm, "mid": v(31.84, -20.55) * mm, "end": v(33.73, -21.66) * mm});
            skArc(sketch, "E17.9.8.1", {"start": v(27.39, -21.66) * mm, "mid": v(29.28, -20.55) * mm, "end": v(30.4, -18.66) * mm});
            skArc(sketch, "E17.9.8.2", {"start": v(30.73, -18.66) * mm, "mid": v(30.56, -18.65) * mm, "end": v(30.4, -18.66) * mm});
            skArc(sketch, "E17.9.8.3", {"start": v(27.39, -21.66) * mm, "mid": v(27.38, -21.83) * mm, "end": v(27.39, -22) * mm});
            skArc(sketch, "E17.9.8.4", {"start": v(30.4, -25) * mm, "mid": v(29.28, -23.1) * mm, "end": v(27.39, -22) * mm});
            skArc(sketch, "E17.9.8.5", {"start": v(33.73, -22) * mm, "mid": v(31.84, -23.1) * mm, "end": v(30.73, -25) * mm});
            skArc(sketch, "E17.9.8.6", {"start": v(30.4, -25) * mm, "mid": v(30.56, -25) * mm, "end": v(30.73, -25) * mm});
            skArc(sketch, "E17.9.8.7", {"start": v(33.73, -22) * mm, "mid": v(33.73, -21.83) * mm, "end": v(33.73, -21.66) * mm});
            skArc(sketch, "E17.9.9.0", {"start": v(30.73, -27.39) * mm, "mid": v(31.84, -29.28) * mm, "end": v(33.73, -30.4) * mm});
            skArc(sketch, "E17.9.9.1", {"start": v(27.39, -30.4) * mm, "mid": v(29.28, -29.28) * mm, "end": v(30.4, -27.39) * mm});
            skArc(sketch, "E17.9.9.2", {"start": v(30.73, -27.39) * mm, "mid": v(30.56, -27.38) * mm, "end": v(30.4, -27.39) * mm});
            skArc(sketch, "E17.9.9.3", {"start": v(27.39, -30.4) * mm, "mid": v(27.38, -30.56) * mm, "end": v(27.39, -30.73) * mm});
            skArc(sketch, "E17.9.9.4", {"start": v(30.4, -33.73) * mm, "mid": v(29.28, -31.84) * mm, "end": v(27.39, -30.73) * mm});
            skArc(sketch, "E17.9.9.5", {"start": v(33.73, -30.73) * mm, "mid": v(31.84, -31.84) * mm, "end": v(30.73, -33.73) * mm});
            skArc(sketch, "E17.9.9.6", {"start": v(30.4, -33.73) * mm, "mid": v(30.56, -33.73) * mm, "end": v(30.73, -33.73) * mm});
            skArc(sketch, "E17.9.9.7", {"start": v(33.73, -30.73) * mm, "mid": v(33.73, -30.56) * mm, "end": v(33.73, -30.4) * mm});
            skArc(sketch, "E17.9.10.0", {"start": v(30.73, -36.12) * mm, "mid": v(31.84, -38.01) * mm, "end": v(33.73, -39.12) * mm});
            skArc(sketch, "E17.9.10.1", {"start": v(27.39, -39.12) * mm, "mid": v(29.28, -38.01) * mm, "end": v(30.4, -36.12) * mm});
            skArc(sketch, "E17.9.10.2", {"start": v(30.73, -36.12) * mm, "mid": v(30.56, -36.12) * mm, "end": v(30.4, -36.12) * mm});
            skArc(sketch, "E17.9.10.3", {"start": v(27.39, -39.12) * mm, "mid": v(27.38, -39.3) * mm, "end": v(27.39, -39.46) * mm});
            skArc(sketch, "E17.9.10.4", {"start": v(30.4, -42.46) * mm, "mid": v(29.28, -40.57) * mm, "end": v(27.39, -39.46) * mm});
            skArc(sketch, "E17.9.10.5", {"start": v(33.73, -39.46) * mm, "mid": v(31.84, -40.57) * mm, "end": v(30.73, -42.46) * mm});
            skArc(sketch, "E17.9.10.6", {"start": v(30.4, -42.46) * mm, "mid": v(30.56, -42.47) * mm, "end": v(30.73, -42.46) * mm});
            skArc(sketch, "E17.9.10.7", {"start": v(33.73, -39.46) * mm, "mid": v(33.73, -39.3) * mm, "end": v(33.73, -39.12) * mm});
            skArc(sketch, "E17.9.11.0", {"start": v(30.73, -44.85) * mm, "mid": v(31.84, -46.74) * mm, "end": v(33.73, -47.86) * mm});
            skArc(sketch, "E17.9.11.1", {"start": v(27.39, -47.86) * mm, "mid": v(29.28, -46.74) * mm, "end": v(30.4, -44.85) * mm});
            skArc(sketch, "E17.9.11.2", {"start": v(30.73, -44.85) * mm, "mid": v(30.56, -44.85) * mm, "end": v(30.4, -44.85) * mm});
            skArc(sketch, "E17.9.11.3", {"start": v(27.39, -47.86) * mm, "mid": v(27.38, -48.02) * mm, "end": v(27.39, -48.19) * mm});
            skArc(sketch, "E17.9.11.4", {"start": v(30.4, -51.2) * mm, "mid": v(29.28, -49.3) * mm, "end": v(27.39, -48.19) * mm});
            skArc(sketch, "E17.9.11.5", {"start": v(33.73, -48.19) * mm, "mid": v(31.84, -49.3) * mm, "end": v(30.73, -51.2) * mm});
            skArc(sketch, "E17.9.11.6", {"start": v(30.4, -51.2) * mm, "mid": v(30.56, -51.2) * mm, "end": v(30.73, -51.2) * mm});
            skArc(sketch, "E17.9.11.7", {"start": v(33.73, -48.19) * mm, "mid": v(33.73, -48.02) * mm, "end": v(33.73, -47.86) * mm});
            skArc(sketch, "E17.10.0.0", {"start": v(39.46, 51.2) * mm, "mid": v(40.57, 49.3) * mm, "end": v(42.46, 48.19) * mm});
            skArc(sketch, "E17.10.0.1", {"start": v(36.12, 48.19) * mm, "mid": v(38.01, 49.3) * mm, "end": v(39.12, 51.2) * mm});
            skArc(sketch, "E17.10.0.2", {"start": v(39.46, 51.2) * mm, "mid": v(39.3, 51.2) * mm, "end": v(39.12, 51.2) * mm});
            skArc(sketch, "E17.10.0.3", {"start": v(36.12, 48.19) * mm, "mid": v(36.12, 48.02) * mm, "end": v(36.12, 47.86) * mm});
            skArc(sketch, "E17.10.0.4", {"start": v(39.12, 44.85) * mm, "mid": v(38.01, 46.74) * mm, "end": v(36.12, 47.86) * mm});
            skArc(sketch, "E17.10.0.5", {"start": v(42.46, 47.86) * mm, "mid": v(40.57, 46.74) * mm, "end": v(39.46, 44.85) * mm});
            skArc(sketch, "E17.10.0.6", {"start": v(39.12, 44.85) * mm, "mid": v(39.3, 44.85) * mm, "end": v(39.46, 44.85) * mm});
            skArc(sketch, "E17.10.0.7", {"start": v(42.46, 47.86) * mm, "mid": v(42.47, 48.02) * mm, "end": v(42.46, 48.19) * mm});
            skArc(sketch, "E17.10.1.0", {"start": v(39.46, 42.46) * mm, "mid": v(40.57, 40.57) * mm, "end": v(42.46, 39.46) * mm});
            skArc(sketch, "E17.10.1.1", {"start": v(36.12, 39.46) * mm, "mid": v(38.01, 40.57) * mm, "end": v(39.12, 42.46) * mm});
            skArc(sketch, "E17.10.1.2", {"start": v(39.46, 42.46) * mm, "mid": v(39.3, 42.47) * mm, "end": v(39.12, 42.46) * mm});
            skArc(sketch, "E17.10.1.3", {"start": v(36.12, 39.46) * mm, "mid": v(36.12, 39.3) * mm, "end": v(36.12, 39.12) * mm});
            skArc(sketch, "E17.10.1.4", {"start": v(39.12, 36.12) * mm, "mid": v(38.01, 38.01) * mm, "end": v(36.12, 39.12) * mm});
            skArc(sketch, "E17.10.1.5", {"start": v(42.46, 39.12) * mm, "mid": v(40.57, 38.01) * mm, "end": v(39.46, 36.12) * mm});
            skArc(sketch, "E17.10.1.6", {"start": v(39.12, 36.12) * mm, "mid": v(39.3, 36.12) * mm, "end": v(39.46, 36.12) * mm});
            skArc(sketch, "E17.10.1.7", {"start": v(42.46, 39.12) * mm, "mid": v(42.47, 39.3) * mm, "end": v(42.46, 39.46) * mm});
            skArc(sketch, "E17.10.2.0", {"start": v(39.46, 33.73) * mm, "mid": v(40.57, 31.84) * mm, "end": v(42.46, 30.73) * mm});
            skArc(sketch, "E17.10.2.1", {"start": v(36.12, 30.73) * mm, "mid": v(38.01, 31.84) * mm, "end": v(39.12, 33.73) * mm});
            skArc(sketch, "E17.10.2.2", {"start": v(39.46, 33.73) * mm, "mid": v(39.3, 33.73) * mm, "end": v(39.12, 33.73) * mm});
            skArc(sketch, "E17.10.2.3", {"start": v(36.12, 30.73) * mm, "mid": v(36.12, 30.56) * mm, "end": v(36.12, 30.4) * mm});
            skArc(sketch, "E17.10.2.4", {"start": v(39.12, 27.39) * mm, "mid": v(38.01, 29.28) * mm, "end": v(36.12, 30.4) * mm});
            skArc(sketch, "E17.10.2.5", {"start": v(42.46, 30.4) * mm, "mid": v(40.57, 29.28) * mm, "end": v(39.46, 27.39) * mm});
            skArc(sketch, "E17.10.2.6", {"start": v(39.12, 27.39) * mm, "mid": v(39.3, 27.38) * mm, "end": v(39.46, 27.39) * mm});
            skArc(sketch, "E17.10.2.7", {"start": v(42.46, 30.4) * mm, "mid": v(42.47, 30.56) * mm, "end": v(42.46, 30.73) * mm});
            skArc(sketch, "E17.10.3.0", {"start": v(39.46, 25) * mm, "mid": v(40.57, 23.1) * mm, "end": v(42.46, 22) * mm});
            skArc(sketch, "E17.10.3.1", {"start": v(36.12, 22) * mm, "mid": v(38.01, 23.1) * mm, "end": v(39.12, 25) * mm});
            skArc(sketch, "E17.10.3.2", {"start": v(39.46, 25) * mm, "mid": v(39.3, 25) * mm, "end": v(39.12, 25) * mm});
            skArc(sketch, "E17.10.3.3", {"start": v(36.12, 22) * mm, "mid": v(36.12, 21.83) * mm, "end": v(36.12, 21.66) * mm});
            skArc(sketch, "E17.10.3.4", {"start": v(39.12, 18.66) * mm, "mid": v(38.01, 20.55) * mm, "end": v(36.12, 21.66) * mm});
            skArc(sketch, "E17.10.3.5", {"start": v(42.46, 21.66) * mm, "mid": v(40.57, 20.55) * mm, "end": v(39.46, 18.66) * mm});
            skArc(sketch, "E17.10.3.6", {"start": v(39.12, 18.66) * mm, "mid": v(39.3, 18.65) * mm, "end": v(39.46, 18.66) * mm});
            skArc(sketch, "E17.10.3.7", {"start": v(42.46, 21.66) * mm, "mid": v(42.47, 21.83) * mm, "end": v(42.46, 22) * mm});
            skArc(sketch, "E17.10.4.0", {"start": v(39.46, 16.27) * mm, "mid": v(40.57, 14.38) * mm, "end": v(42.46, 13.26) * mm});
            skArc(sketch, "E17.10.4.1", {"start": v(36.12, 13.26) * mm, "mid": v(38.01, 14.38) * mm, "end": v(39.12, 16.27) * mm});
            skArc(sketch, "E17.10.4.2", {"start": v(39.46, 16.27) * mm, "mid": v(39.3, 16.27) * mm, "end": v(39.12, 16.27) * mm});
            skArc(sketch, "E17.10.4.3", {"start": v(36.12, 13.26) * mm, "mid": v(36.12, 13.1) * mm, "end": v(36.12, 12.93) * mm});
            skArc(sketch, "E17.10.4.4", {"start": v(39.12, 9.93) * mm, "mid": v(38.01, 11.82) * mm, "end": v(36.12, 12.93) * mm});
            skArc(sketch, "E17.10.4.5", {"start": v(42.46, 12.93) * mm, "mid": v(40.57, 11.82) * mm, "end": v(39.46, 9.93) * mm});
            skArc(sketch, "E17.10.4.6", {"start": v(39.12, 9.93) * mm, "mid": v(39.3, 9.92) * mm, "end": v(39.46, 9.93) * mm});
            skArc(sketch, "E17.10.4.7", {"start": v(42.46, 12.93) * mm, "mid": v(42.47, 13.1) * mm, "end": v(42.46, 13.26) * mm});
            skArc(sketch, "E17.10.5.0", {"start": v(39.46, 7.54) * mm, "mid": v(40.57, 5.64) * mm, "end": v(42.46, 4.53) * mm});
            skArc(sketch, "E17.10.5.1", {"start": v(36.12, 4.53) * mm, "mid": v(38.01, 5.64) * mm, "end": v(39.12, 7.54) * mm});
            skArc(sketch, "E17.10.5.2", {"start": v(39.46, 7.54) * mm, "mid": v(39.3, 7.54) * mm, "end": v(39.12, 7.54) * mm});
            skArc(sketch, "E17.10.5.3", {"start": v(36.12, 4.53) * mm, "mid": v(36.12, 4.37) * mm, "end": v(36.12, 4.2) * mm});
            skArc(sketch, "E17.10.5.4", {"start": v(39.12, 1.2) * mm, "mid": v(38.01, 3.09) * mm, "end": v(36.12, 4.2) * mm});
            skArc(sketch, "E17.10.5.5", {"start": v(42.46, 4.2) * mm, "mid": v(40.57, 3.09) * mm, "end": v(39.46, 1.2) * mm});
            skArc(sketch, "E17.10.5.6", {"start": v(39.12, 1.2) * mm, "mid": v(39.3, 1.2) * mm, "end": v(39.46, 1.2) * mm});
            skArc(sketch, "E17.10.5.7", {"start": v(42.46, 4.2) * mm, "mid": v(42.47, 4.37) * mm, "end": v(42.46, 4.53) * mm});
            skArc(sketch, "E17.10.6.0", {"start": v(39.46, -1.2) * mm, "mid": v(40.57, -3.09) * mm, "end": v(42.46, -4.2) * mm});
            skArc(sketch, "E17.10.6.1", {"start": v(36.12, -4.2) * mm, "mid": v(38.01, -3.09) * mm, "end": v(39.12, -1.2) * mm});
            skArc(sketch, "E17.10.6.2", {"start": v(39.46, -1.2) * mm, "mid": v(39.3, -1.2) * mm, "end": v(39.12, -1.2) * mm});
            skArc(sketch, "E17.10.6.3", {"start": v(36.12, -4.2) * mm, "mid": v(36.12, -4.37) * mm, "end": v(36.12, -4.53) * mm});
            skArc(sketch, "E17.10.6.4", {"start": v(39.12, -7.54) * mm, "mid": v(38.01, -5.64) * mm, "end": v(36.12, -4.53) * mm});
            skArc(sketch, "E17.10.6.5", {"start": v(42.46, -4.53) * mm, "mid": v(40.57, -5.64) * mm, "end": v(39.46, -7.54) * mm});
            skArc(sketch, "E17.10.6.6", {"start": v(39.12, -7.54) * mm, "mid": v(39.3, -7.54) * mm, "end": v(39.46, -7.54) * mm});
            skArc(sketch, "E17.10.6.7", {"start": v(42.46, -4.53) * mm, "mid": v(42.47, -4.37) * mm, "end": v(42.46, -4.2) * mm});
            skArc(sketch, "E17.10.7.0", {"start": v(39.46, -9.93) * mm, "mid": v(40.57, -11.82) * mm, "end": v(42.46, -12.93) * mm});
            skArc(sketch, "E17.10.7.1", {"start": v(36.12, -12.93) * mm, "mid": v(38.01, -11.82) * mm, "end": v(39.12, -9.93) * mm});
            skArc(sketch, "E17.10.7.2", {"start": v(39.46, -9.93) * mm, "mid": v(39.3, -9.92) * mm, "end": v(39.12, -9.93) * mm});
            skArc(sketch, "E17.10.7.3", {"start": v(36.12, -12.93) * mm, "mid": v(36.12, -13.1) * mm, "end": v(36.12, -13.26) * mm});
            skArc(sketch, "E17.10.7.4", {"start": v(39.12, -16.27) * mm, "mid": v(38.01, -14.38) * mm, "end": v(36.12, -13.26) * mm});
            skArc(sketch, "E17.10.7.5", {"start": v(42.46, -13.26) * mm, "mid": v(40.57, -14.38) * mm, "end": v(39.46, -16.27) * mm});
            skArc(sketch, "E17.10.7.6", {"start": v(39.12, -16.27) * mm, "mid": v(39.3, -16.27) * mm, "end": v(39.46, -16.27) * mm});
            skArc(sketch, "E17.10.7.7", {"start": v(42.46, -13.26) * mm, "mid": v(42.47, -13.1) * mm, "end": v(42.46, -12.93) * mm});
            skArc(sketch, "E17.10.8.0", {"start": v(39.46, -18.66) * mm, "mid": v(40.57, -20.55) * mm, "end": v(42.46, -21.66) * mm});
            skArc(sketch, "E17.10.8.1", {"start": v(36.12, -21.66) * mm, "mid": v(38.01, -20.55) * mm, "end": v(39.12, -18.66) * mm});
            skArc(sketch, "E17.10.8.2", {"start": v(39.46, -18.66) * mm, "mid": v(39.3, -18.65) * mm, "end": v(39.12, -18.66) * mm});
            skArc(sketch, "E17.10.8.3", {"start": v(36.12, -21.66) * mm, "mid": v(36.12, -21.83) * mm, "end": v(36.12, -22) * mm});
            skArc(sketch, "E17.10.8.4", {"start": v(39.12, -25) * mm, "mid": v(38.01, -23.1) * mm, "end": v(36.12, -22) * mm});
            skArc(sketch, "E17.10.8.5", {"start": v(42.46, -22) * mm, "mid": v(40.57, -23.1) * mm, "end": v(39.46, -25) * mm});
            skArc(sketch, "E17.10.8.6", {"start": v(39.12, -25) * mm, "mid": v(39.3, -25) * mm, "end": v(39.46, -25) * mm});
            skArc(sketch, "E17.10.8.7", {"start": v(42.46, -22) * mm, "mid": v(42.47, -21.83) * mm, "end": v(42.46, -21.66) * mm});
            skArc(sketch, "E17.10.9.0", {"start": v(39.46, -27.39) * mm, "mid": v(40.57, -29.28) * mm, "end": v(42.46, -30.4) * mm});
            skArc(sketch, "E17.10.9.1", {"start": v(36.12, -30.4) * mm, "mid": v(38.01, -29.28) * mm, "end": v(39.12, -27.39) * mm});
            skArc(sketch, "E17.10.9.2", {"start": v(39.46, -27.39) * mm, "mid": v(39.3, -27.38) * mm, "end": v(39.12, -27.39) * mm});
            skArc(sketch, "E17.10.9.3", {"start": v(36.12, -30.4) * mm, "mid": v(36.12, -30.56) * mm, "end": v(36.12, -30.73) * mm});
            skArc(sketch, "E17.10.9.4", {"start": v(39.12, -33.73) * mm, "mid": v(38.01, -31.84) * mm, "end": v(36.12, -30.73) * mm});
            skArc(sketch, "E17.10.9.5", {"start": v(42.46, -30.73) * mm, "mid": v(40.57, -31.84) * mm, "end": v(39.46, -33.73) * mm});
            skArc(sketch, "E17.10.9.6", {"start": v(39.12, -33.73) * mm, "mid": v(39.3, -33.73) * mm, "end": v(39.46, -33.73) * mm});
            skArc(sketch, "E17.10.9.7", {"start": v(42.46, -30.73) * mm, "mid": v(42.47, -30.56) * mm, "end": v(42.46, -30.4) * mm});
            skArc(sketch, "E17.10.10.0", {"start": v(39.46, -36.12) * mm, "mid": v(40.57, -38.01) * mm, "end": v(42.46, -39.12) * mm});
            skArc(sketch, "E17.10.10.1", {"start": v(36.12, -39.12) * mm, "mid": v(38.01, -38.01) * mm, "end": v(39.12, -36.12) * mm});
            skArc(sketch, "E17.10.10.2", {"start": v(39.46, -36.12) * mm, "mid": v(39.3, -36.12) * mm, "end": v(39.12, -36.12) * mm});
            skArc(sketch, "E17.10.10.3", {"start": v(36.12, -39.12) * mm, "mid": v(36.12, -39.3) * mm, "end": v(36.12, -39.46) * mm});
            skArc(sketch, "E17.10.10.4", {"start": v(39.12, -42.46) * mm, "mid": v(38.01, -40.57) * mm, "end": v(36.12, -39.46) * mm});
            skArc(sketch, "E17.10.10.5", {"start": v(42.46, -39.46) * mm, "mid": v(40.57, -40.57) * mm, "end": v(39.46, -42.46) * mm});
            skArc(sketch, "E17.10.10.6", {"start": v(39.12, -42.46) * mm, "mid": v(39.3, -42.47) * mm, "end": v(39.46, -42.46) * mm});
            skArc(sketch, "E17.10.10.7", {"start": v(42.46, -39.46) * mm, "mid": v(42.47, -39.3) * mm, "end": v(42.46, -39.12) * mm});
            skArc(sketch, "E17.10.11.0", {"start": v(39.46, -44.85) * mm, "mid": v(40.57, -46.74) * mm, "end": v(42.46, -47.86) * mm});
            skArc(sketch, "E17.10.11.1", {"start": v(36.12, -47.86) * mm, "mid": v(38.01, -46.74) * mm, "end": v(39.12, -44.85) * mm});
            skArc(sketch, "E17.10.11.2", {"start": v(39.46, -44.85) * mm, "mid": v(39.3, -44.85) * mm, "end": v(39.12, -44.85) * mm});
            skArc(sketch, "E17.10.11.3", {"start": v(36.12, -47.86) * mm, "mid": v(36.12, -48.02) * mm, "end": v(36.12, -48.19) * mm});
            skArc(sketch, "E17.10.11.4", {"start": v(39.12, -51.2) * mm, "mid": v(38.01, -49.3) * mm, "end": v(36.12, -48.19) * mm});
            skArc(sketch, "E17.10.11.5", {"start": v(42.46, -48.19) * mm, "mid": v(40.57, -49.3) * mm, "end": v(39.46, -51.2) * mm});
            skArc(sketch, "E17.10.11.6", {"start": v(39.12, -51.2) * mm, "mid": v(39.3, -51.2) * mm, "end": v(39.46, -51.2) * mm});
            skArc(sketch, "E17.10.11.7", {"start": v(42.46, -48.19) * mm, "mid": v(42.47, -48.02) * mm, "end": v(42.46, -47.86) * mm});
            skArc(sketch, "E17.11.0.0", {"start": v(48.19, 51.2) * mm, "mid": v(49.3, 49.3) * mm, "end": v(51.2, 48.19) * mm});
            skArc(sketch, "E17.11.0.1", {"start": v(44.85, 48.19) * mm, "mid": v(46.74, 49.3) * mm, "end": v(47.86, 51.2) * mm});
            skArc(sketch, "E17.11.0.2", {"start": v(48.19, 51.2) * mm, "mid": v(48.02, 51.2) * mm, "end": v(47.86, 51.2) * mm});
            skArc(sketch, "E17.11.0.3", {"start": v(44.85, 48.19) * mm, "mid": v(44.85, 48.02) * mm, "end": v(44.85, 47.86) * mm});
            skArc(sketch, "E17.11.0.4", {"start": v(47.86, 44.85) * mm, "mid": v(46.74, 46.74) * mm, "end": v(44.85, 47.86) * mm});
            skArc(sketch, "E17.11.0.5", {"start": v(51.2, 47.86) * mm, "mid": v(49.3, 46.74) * mm, "end": v(48.19, 44.85) * mm});
            skArc(sketch, "E17.11.0.6", {"start": v(47.86, 44.85) * mm, "mid": v(48.02, 44.85) * mm, "end": v(48.19, 44.85) * mm});
            skArc(sketch, "E17.11.0.7", {"start": v(51.2, 47.86) * mm, "mid": v(51.2, 48.02) * mm, "end": v(51.2, 48.19) * mm});
            skArc(sketch, "E17.11.1.0", {"start": v(48.19, 42.46) * mm, "mid": v(49.3, 40.57) * mm, "end": v(51.2, 39.46) * mm});
            skArc(sketch, "E17.11.1.1", {"start": v(44.85, 39.46) * mm, "mid": v(46.74, 40.57) * mm, "end": v(47.86, 42.46) * mm});
            skArc(sketch, "E17.11.1.2", {"start": v(48.19, 42.46) * mm, "mid": v(48.02, 42.47) * mm, "end": v(47.86, 42.46) * mm});
            skArc(sketch, "E17.11.1.3", {"start": v(44.85, 39.46) * mm, "mid": v(44.85, 39.3) * mm, "end": v(44.85, 39.12) * mm});
            skArc(sketch, "E17.11.1.4", {"start": v(47.86, 36.12) * mm, "mid": v(46.74, 38.01) * mm, "end": v(44.85, 39.12) * mm});
            skArc(sketch, "E17.11.1.5", {"start": v(51.2, 39.12) * mm, "mid": v(49.3, 38.01) * mm, "end": v(48.19, 36.12) * mm});
            skArc(sketch, "E17.11.1.6", {"start": v(47.86, 36.12) * mm, "mid": v(48.02, 36.12) * mm, "end": v(48.19, 36.12) * mm});
            skArc(sketch, "E17.11.1.7", {"start": v(51.2, 39.12) * mm, "mid": v(51.2, 39.3) * mm, "end": v(51.2, 39.46) * mm});
            skArc(sketch, "E17.11.2.0", {"start": v(48.19, 33.73) * mm, "mid": v(49.3, 31.84) * mm, "end": v(51.2, 30.73) * mm});
            skArc(sketch, "E17.11.2.1", {"start": v(44.85, 30.73) * mm, "mid": v(46.74, 31.84) * mm, "end": v(47.86, 33.73) * mm});
            skArc(sketch, "E17.11.2.2", {"start": v(48.19, 33.73) * mm, "mid": v(48.02, 33.73) * mm, "end": v(47.86, 33.73) * mm});
            skArc(sketch, "E17.11.2.3", {"start": v(44.85, 30.73) * mm, "mid": v(44.85, 30.56) * mm, "end": v(44.85, 30.4) * mm});
            skArc(sketch, "E17.11.2.4", {"start": v(47.86, 27.39) * mm, "mid": v(46.74, 29.28) * mm, "end": v(44.85, 30.4) * mm});
            skArc(sketch, "E17.11.2.5", {"start": v(51.2, 30.4) * mm, "mid": v(49.3, 29.28) * mm, "end": v(48.19, 27.39) * mm});
            skArc(sketch, "E17.11.2.6", {"start": v(47.86, 27.39) * mm, "mid": v(48.02, 27.38) * mm, "end": v(48.19, 27.39) * mm});
            skArc(sketch, "E17.11.2.7", {"start": v(51.2, 30.4) * mm, "mid": v(51.2, 30.56) * mm, "end": v(51.2, 30.73) * mm});
            skArc(sketch, "E17.11.3.0", {"start": v(48.19, 25) * mm, "mid": v(49.3, 23.1) * mm, "end": v(51.2, 22) * mm});
            skArc(sketch, "E17.11.3.1", {"start": v(44.85, 22) * mm, "mid": v(46.74, 23.1) * mm, "end": v(47.86, 25) * mm});
            skArc(sketch, "E17.11.3.2", {"start": v(48.19, 25) * mm, "mid": v(48.02, 25) * mm, "end": v(47.86, 25) * mm});
            skArc(sketch, "E17.11.3.3", {"start": v(44.85, 22) * mm, "mid": v(44.85, 21.83) * mm, "end": v(44.85, 21.66) * mm});
            skArc(sketch, "E17.11.3.4", {"start": v(47.86, 18.66) * mm, "mid": v(46.74, 20.55) * mm, "end": v(44.85, 21.66) * mm});
            skArc(sketch, "E17.11.3.5", {"start": v(51.2, 21.66) * mm, "mid": v(49.3, 20.55) * mm, "end": v(48.19, 18.66) * mm});
            skArc(sketch, "E17.11.3.6", {"start": v(47.86, 18.66) * mm, "mid": v(48.02, 18.65) * mm, "end": v(48.19, 18.66) * mm});
            skArc(sketch, "E17.11.3.7", {"start": v(51.2, 21.66) * mm, "mid": v(51.2, 21.83) * mm, "end": v(51.2, 22) * mm});
            skArc(sketch, "E17.11.4.0", {"start": v(48.19, 16.27) * mm, "mid": v(49.3, 14.38) * mm, "end": v(51.2, 13.26) * mm});
            skArc(sketch, "E17.11.4.1", {"start": v(44.85, 13.26) * mm, "mid": v(46.74, 14.38) * mm, "end": v(47.86, 16.27) * mm});
            skArc(sketch, "E17.11.4.2", {"start": v(48.19, 16.27) * mm, "mid": v(48.02, 16.27) * mm, "end": v(47.86, 16.27) * mm});
            skArc(sketch, "E17.11.4.3", {"start": v(44.85, 13.26) * mm, "mid": v(44.85, 13.1) * mm, "end": v(44.85, 12.93) * mm});
            skArc(sketch, "E17.11.4.4", {"start": v(47.86, 9.93) * mm, "mid": v(46.74, 11.82) * mm, "end": v(44.85, 12.93) * mm});
            skArc(sketch, "E17.11.4.5", {"start": v(51.2, 12.93) * mm, "mid": v(49.3, 11.82) * mm, "end": v(48.19, 9.93) * mm});
            skArc(sketch, "E17.11.4.6", {"start": v(47.86, 9.93) * mm, "mid": v(48.02, 9.92) * mm, "end": v(48.19, 9.93) * mm});
            skArc(sketch, "E17.11.4.7", {"start": v(51.2, 12.93) * mm, "mid": v(51.2, 13.1) * mm, "end": v(51.2, 13.26) * mm});
            skArc(sketch, "E17.11.5.0", {"start": v(48.19, 7.54) * mm, "mid": v(49.3, 5.64) * mm, "end": v(51.2, 4.53) * mm});
            skArc(sketch, "E17.11.5.1", {"start": v(44.85, 4.53) * mm, "mid": v(46.74, 5.64) * mm, "end": v(47.86, 7.54) * mm});
            skArc(sketch, "E17.11.5.2", {"start": v(48.19, 7.54) * mm, "mid": v(48.02, 7.54) * mm, "end": v(47.86, 7.54) * mm});
            skArc(sketch, "E17.11.5.3", {"start": v(44.85, 4.53) * mm, "mid": v(44.85, 4.37) * mm, "end": v(44.85, 4.2) * mm});
            skArc(sketch, "E17.11.5.4", {"start": v(47.86, 1.2) * mm, "mid": v(46.74, 3.09) * mm, "end": v(44.85, 4.2) * mm});
            skArc(sketch, "E17.11.5.5", {"start": v(51.2, 4.2) * mm, "mid": v(49.3, 3.09) * mm, "end": v(48.19, 1.2) * mm});
            skArc(sketch, "E17.11.5.6", {"start": v(47.86, 1.2) * mm, "mid": v(48.02, 1.2) * mm, "end": v(48.19, 1.2) * mm});
            skArc(sketch, "E17.11.5.7", {"start": v(51.2, 4.2) * mm, "mid": v(51.2, 4.37) * mm, "end": v(51.2, 4.53) * mm});
            skArc(sketch, "E17.11.6.0", {"start": v(48.19, -1.2) * mm, "mid": v(49.3, -3.09) * mm, "end": v(51.2, -4.2) * mm});
            skArc(sketch, "E17.11.6.1", {"start": v(44.85, -4.2) * mm, "mid": v(46.74, -3.09) * mm, "end": v(47.86, -1.2) * mm});
            skArc(sketch, "E17.11.6.2", {"start": v(48.19, -1.2) * mm, "mid": v(48.02, -1.2) * mm, "end": v(47.86, -1.2) * mm});
            skArc(sketch, "E17.11.6.3", {"start": v(44.85, -4.2) * mm, "mid": v(44.85, -4.37) * mm, "end": v(44.85, -4.53) * mm});
            skArc(sketch, "E17.11.6.4", {"start": v(47.86, -7.54) * mm, "mid": v(46.74, -5.64) * mm, "end": v(44.85, -4.53) * mm});
            skArc(sketch, "E17.11.6.5", {"start": v(51.2, -4.53) * mm, "mid": v(49.3, -5.64) * mm, "end": v(48.19, -7.54) * mm});
            skArc(sketch, "E17.11.6.6", {"start": v(47.86, -7.54) * mm, "mid": v(48.02, -7.54) * mm, "end": v(48.19, -7.54) * mm});
            skArc(sketch, "E17.11.6.7", {"start": v(51.2, -4.53) * mm, "mid": v(51.2, -4.37) * mm, "end": v(51.2, -4.2) * mm});
            skArc(sketch, "E17.11.7.0", {"start": v(48.19, -9.93) * mm, "mid": v(49.3, -11.82) * mm, "end": v(51.2, -12.93) * mm});
            skArc(sketch, "E17.11.7.1", {"start": v(44.85, -12.93) * mm, "mid": v(46.74, -11.82) * mm, "end": v(47.86, -9.93) * mm});
            skArc(sketch, "E17.11.7.2", {"start": v(48.19, -9.93) * mm, "mid": v(48.02, -9.92) * mm, "end": v(47.86, -9.93) * mm});
            skArc(sketch, "E17.11.7.3", {"start": v(44.85, -12.93) * mm, "mid": v(44.85, -13.1) * mm, "end": v(44.85, -13.26) * mm});
            skArc(sketch, "E17.11.7.4", {"start": v(47.86, -16.27) * mm, "mid": v(46.74, -14.38) * mm, "end": v(44.85, -13.26) * mm});
            skArc(sketch, "E17.11.7.5", {"start": v(51.2, -13.26) * mm, "mid": v(49.3, -14.38) * mm, "end": v(48.19, -16.27) * mm});
            skArc(sketch, "E17.11.7.6", {"start": v(47.86, -16.27) * mm, "mid": v(48.02, -16.27) * mm, "end": v(48.19, -16.27) * mm});
            skArc(sketch, "E17.11.7.7", {"start": v(51.2, -13.26) * mm, "mid": v(51.2, -13.1) * mm, "end": v(51.2, -12.93) * mm});
            skArc(sketch, "E17.11.8.0", {"start": v(48.19, -18.66) * mm, "mid": v(49.3, -20.55) * mm, "end": v(51.2, -21.66) * mm});
            skArc(sketch, "E17.11.8.1", {"start": v(44.85, -21.66) * mm, "mid": v(46.74, -20.55) * mm, "end": v(47.86, -18.66) * mm});
            skArc(sketch, "E17.11.8.2", {"start": v(48.19, -18.66) * mm, "mid": v(48.02, -18.65) * mm, "end": v(47.86, -18.66) * mm});
            skArc(sketch, "E17.11.8.3", {"start": v(44.85, -21.66) * mm, "mid": v(44.85, -21.83) * mm, "end": v(44.85, -22) * mm});
            skArc(sketch, "E17.11.8.4", {"start": v(47.86, -25) * mm, "mid": v(46.74, -23.1) * mm, "end": v(44.85, -22) * mm});
            skArc(sketch, "E17.11.8.5", {"start": v(51.2, -22) * mm, "mid": v(49.3, -23.1) * mm, "end": v(48.19, -25) * mm});
            skArc(sketch, "E17.11.8.6", {"start": v(47.86, -25) * mm, "mid": v(48.02, -25) * mm, "end": v(48.19, -25) * mm});
            skArc(sketch, "E17.11.8.7", {"start": v(51.2, -22) * mm, "mid": v(51.2, -21.83) * mm, "end": v(51.2, -21.66) * mm});
            skArc(sketch, "E17.11.9.0", {"start": v(48.19, -27.39) * mm, "mid": v(49.3, -29.28) * mm, "end": v(51.2, -30.4) * mm});
            skArc(sketch, "E17.11.9.1", {"start": v(44.85, -30.4) * mm, "mid": v(46.74, -29.28) * mm, "end": v(47.86, -27.39) * mm});
            skArc(sketch, "E17.11.9.2", {"start": v(48.19, -27.39) * mm, "mid": v(48.02, -27.38) * mm, "end": v(47.86, -27.39) * mm});
            skArc(sketch, "E17.11.9.3", {"start": v(44.85, -30.4) * mm, "mid": v(44.85, -30.56) * mm, "end": v(44.85, -30.73) * mm});
            skArc(sketch, "E17.11.9.4", {"start": v(47.86, -33.73) * mm, "mid": v(46.74, -31.84) * mm, "end": v(44.85, -30.73) * mm});
            skArc(sketch, "E17.11.9.5", {"start": v(51.2, -30.73) * mm, "mid": v(49.3, -31.84) * mm, "end": v(48.19, -33.73) * mm});
            skArc(sketch, "E17.11.9.6", {"start": v(47.86, -33.73) * mm, "mid": v(48.02, -33.73) * mm, "end": v(48.19, -33.73) * mm});
            skArc(sketch, "E17.11.9.7", {"start": v(51.2, -30.73) * mm, "mid": v(51.2, -30.56) * mm, "end": v(51.2, -30.4) * mm});
            skArc(sketch, "E17.11.10.0", {"start": v(48.19, -36.12) * mm, "mid": v(49.3, -38.01) * mm, "end": v(51.2, -39.12) * mm});
            skArc(sketch, "E17.11.10.1", {"start": v(44.85, -39.12) * mm, "mid": v(46.74, -38.01) * mm, "end": v(47.86, -36.12) * mm});
            skArc(sketch, "E17.11.10.2", {"start": v(48.19, -36.12) * mm, "mid": v(48.02, -36.12) * mm, "end": v(47.86, -36.12) * mm});
            skArc(sketch, "E17.11.10.3", {"start": v(44.85, -39.12) * mm, "mid": v(44.85, -39.3) * mm, "end": v(44.85, -39.46) * mm});
            skArc(sketch, "E17.11.10.4", {"start": v(47.86, -42.46) * mm, "mid": v(46.74, -40.57) * mm, "end": v(44.85, -39.46) * mm});
            skArc(sketch, "E17.11.10.5", {"start": v(51.2, -39.46) * mm, "mid": v(49.3, -40.57) * mm, "end": v(48.19, -42.46) * mm});
            skArc(sketch, "E17.11.10.6", {"start": v(47.86, -42.46) * mm, "mid": v(48.02, -42.47) * mm, "end": v(48.19, -42.46) * mm});
            skArc(sketch, "E17.11.10.7", {"start": v(51.2, -39.46) * mm, "mid": v(51.2, -39.3) * mm, "end": v(51.2, -39.12) * mm});
            skArc(sketch, "E17.11.11.0", {"start": v(48.19, -44.85) * mm, "mid": v(49.3, -46.74) * mm, "end": v(51.2, -47.86) * mm});
            skArc(sketch, "E17.11.11.1", {"start": v(44.85, -47.86) * mm, "mid": v(46.74, -46.74) * mm, "end": v(47.86, -44.85) * mm});
            skArc(sketch, "E17.11.11.2", {"start": v(48.19, -44.85) * mm, "mid": v(48.02, -44.85) * mm, "end": v(47.86, -44.85) * mm});
            skArc(sketch, "E17.11.11.3", {"start": v(44.85, -47.86) * mm, "mid": v(44.85, -48.02) * mm, "end": v(44.85, -48.19) * mm});
            skArc(sketch, "E17.11.11.4", {"start": v(47.86, -51.2) * mm, "mid": v(46.74, -49.3) * mm, "end": v(44.85, -48.19) * mm});
            skArc(sketch, "E17.11.11.5", {"start": v(51.2, -48.19) * mm, "mid": v(49.3, -49.3) * mm, "end": v(48.19, -51.2) * mm});
            skArc(sketch, "E17.11.11.6", {"start": v(47.86, -51.2) * mm, "mid": v(48.02, -51.2) * mm, "end": v(48.19, -51.2) * mm});
            skArc(sketch, "E17.11.11.7", {"start": v(51.2, -48.19) * mm, "mid": v(51.2, -48.02) * mm, "end": v(51.2, -47.86) * mm});
            skLineSegment(sketch, "E17.direction1", {"start": v(-52.39, 43.66) * mm, "end": v(-43.66, 43.66) * mm, "construction": true});
            skLineSegment(sketch, "E17.direction2", {"start": v(-52.39, 43.66) * mm, "end": v(-52.39, 34.93) * mm, "construction": true});
            skLineSegment(sketch, "E18", {"start": v(52.39, -52.39) * mm, "end": v(43.66, -43.66) * mm, "construction": true});
            skSolve(sketch);
        }
        {
            var Q0;
            Q0 = qSketchRegion(id + "F2", true);
            var Q1;
            Q1=makeQuery(id+"F1.opExtrude","CAP_FACE",FACE,{"disambiguationData":[OSD([sQuery(id+"F0.wireOp",EDGE,"E0.bottom"),sQuery(id+"F0.wireOp",EDGE,"E0.top"),sQuery(id+"F0.wireOp",EDGE,"E0.left"),sQuery(id+"F0.wireOp",EDGE,"E0.right"),sQuery(id+"F0.wireOp",EDGE,"E1"),sQuery(id+"F0.wireOp",EDGE,"E5.0.1.0"),sQuery(id+"F0.wireOp",EDGE,"E5.0.2.0"),sQuery(id+"F0.wireOp",EDGE,"E5.0.3.0"),sQuery(id+"F0.wireOp",EDGE,"E5.0.4.0"),sQuery(id+"F0.wireOp",EDGE,"E5.0.5.0"),sQuery(id+"F0.wireOp",EDGE,"E5.0.6.0"),sQuery(id+"F0.wireOp",EDGE,"E5.0.7.0"),sQuery(id+"F0.wireOp",EDGE,"E5.0.8.0"),sQuery(id+"F0.wireOp",EDGE,"E5.0.9.0"),sQuery(id+"F0.wireOp",EDGE,"E5.0.10.0"),sQuery(id+"F0.wireOp",EDGE,"E5.0.11.0"),sQuery(id+"F0.wireOp",EDGE,"E5.0.12.0"),sQuery(id+"F0.wireOp",EDGE,"E5.1.0.0"),sQuery(id+"F0.wireOp",EDGE,"E5.1.1.0"),sQuery(id+"F0.wireOp",EDGE,"E5.1.2.0"),sQuery(id+"F0.wireOp",EDGE,"E5.1.3.0"),sQuery(id+"F0.wireOp",EDGE,"E5.1.4.0"),sQuery(id+"F0.wireOp",EDGE,"E5.1.5.0"),sQuery(id+"F0.wireOp",EDGE,"E5.1.6.0"),sQuery(id+"F0.wireOp",EDGE,"E5.1.7.0"),sQuery(id+"F0.wireOp",EDGE,"E5.1.8.0"),sQuery(id+"F0.wireOp",EDGE,"E5.1.9.0"),sQuery(id+"F0.wireOp",EDGE,"E5.1.10.0"),sQuery(id+"F0.wireOp",EDGE,"E5.1.11.0"),sQuery(id+"F0.wireOp",EDGE,"E5.1.12.0"),sQuery(id+"F0.wireOp",EDGE,"E5.2.0.0"),sQuery(id+"F0.wireOp",EDGE,"E5.2.1.0"),sQuery(id+"F0.wireOp",EDGE,"E5.2.2.0"),sQuery(id+"F0.wireOp",EDGE,"E5.2.3.0"),sQuery(id+"F0.wireOp",EDGE,"E5.2.4.0"),sQuery(id+"F0.wireOp",EDGE,"E5.2.5.0"),sQuery(id+"F0.wireOp",EDGE,"E5.2.6.0"),sQuery(id+"F0.wireOp",EDGE,"E5.2.7.0"),sQuery(id+"F0.wireOp",EDGE,"E5.2.8.0"),sQuery(id+"F0.wireOp",EDGE,"E5.2.9.0"),sQuery(id+"F0.wireOp",EDGE,"E5.2.10.0"),sQuery(id+"F0.wireOp",EDGE,"E5.2.11.0"),sQuery(id+"F0.wireOp",EDGE,"E5.2.12.0"),sQuery(id+"F0.wireOp",EDGE,"E5.3.0.0"),sQuery(id+"F0.wireOp",EDGE,"E5.3.1.0"),sQuery(id+"F0.wireOp",EDGE,"E5.3.2.0"),sQuery(id+"F0.wireOp",EDGE,"E5.3.3.0"),sQuery(id+"F0.wireOp",EDGE,"E5.3.4.0"),sQuery(id+"F0.wireOp",EDGE,"E5.3.5.0"),sQuery(id+"F0.wireOp",EDGE,"E5.3.6.0"),sQuery(id+"F0.wireOp",EDGE,"E5.3.7.0"),sQuery(id+"F0.wireOp",EDGE,"E5.3.8.0"),sQuery(id+"F0.wireOp",EDGE,"E5.3.9.0"),sQuery(id+"F0.wireOp",EDGE,"E5.3.10.0"),sQuery(id+"F0.wireOp",EDGE,"E5.3.11.0"),sQuery(id+"F0.wireOp",EDGE,"E5.3.12.0"),sQuery(id+"F0.wireOp",EDGE,"E5.4.0.0"),sQuery(id+"F0.wireOp",EDGE,"E5.4.1.0"),sQuery(id+"F0.wireOp",EDGE,"E5.4.2.0"),sQuery(id+"F0.wireOp",EDGE,"E5.4.3.0"),sQuery(id+"F0.wireOp",EDGE,"E5.4.4.0"),sQuery(id+"F0.wireOp",EDGE,"E5.4.5.0"),sQuery(id+"F0.wireOp",EDGE,"E5.4.6.0"),sQuery(id+"F0.wireOp",EDGE,"E5.4.7.0"),sQuery(id+"F0.wireOp",EDGE,"E5.4.8.0"),sQuery(id+"F0.wireOp",EDGE,"E5.4.9.0"),sQuery(id+"F0.wireOp",EDGE,"E5.4.10.0"),sQuery(id+"F0.wireOp",EDGE,"E5.4.11.0"),sQuery(id+"F0.wireOp",EDGE,"E5.4.12.0"),sQuery(id+"F0.wireOp",EDGE,"E5.5.0.0"),sQuery(id+"F0.wireOp",EDGE,"E5.5.1.0"),sQuery(id+"F0.wireOp",EDGE,"E5.5.2.0"),sQuery(id+"F0.wireOp",EDGE,"E5.5.3.0"),sQuery(id+"F0.wireOp",EDGE,"E5.5.4.0"),sQuery(id+"F0.wireOp",EDGE,"E5.5.5.0"),sQuery(id+"F0.wireOp",EDGE,"E5.5.6.0"),sQuery(id+"F0.wireOp",EDGE,"E5.5.7.0"),sQuery(id+"F0.wireOp",EDGE,"E5.5.8.0"),sQuery(id+"F0.wireOp",EDGE,"E5.5.9.0"),sQuery(id+"F0.wireOp",EDGE,"E5.5.10.0"),sQuery(id+"F0.wireOp",EDGE,"E5.5.11.0"),sQuery(id+"F0.wireOp",EDGE,"E5.5.12.0"),sQuery(id+"F0.wireOp",EDGE,"E5.6.0.0"),sQuery(id+"F0.wireOp",EDGE,"E5.6.1.0"),sQuery(id+"F0.wireOp",EDGE,"E5.6.2.0"),sQuery(id+"F0.wireOp",EDGE,"E5.6.3.0"),sQuery(id+"F0.wireOp",EDGE,"E5.6.4.0"),sQuery(id+"F0.wireOp",EDGE,"E5.6.5.0"),sQuery(id+"F0.wireOp",EDGE,"E5.6.6.0"),sQuery(id+"F0.wireOp",EDGE,"E5.6.7.0"),sQuery(id+"F0.wireOp",EDGE,"E5.6.8.0"),sQuery(id+"F0.wireOp",EDGE,"E5.6.9.0"),sQuery(id+"F0.wireOp",EDGE,"E5.6.10.0"),sQuery(id+"F0.wireOp",EDGE,"E5.6.11.0"),sQuery(id+"F0.wireOp",EDGE,"E5.6.12.0"),sQuery(id+"F0.wireOp",EDGE,"E5.7.0.0"),sQuery(id+"F0.wireOp",EDGE,"E5.7.1.0"),sQuery(id+"F0.wireOp",EDGE,"E5.7.2.0"),sQuery(id+"F0.wireOp",EDGE,"E5.7.3.0"),sQuery(id+"F0.wireOp",EDGE,"E5.7.4.0"),sQuery(id+"F0.wireOp",EDGE,"E5.7.5.0"),sQuery(id+"F0.wireOp",EDGE,"E5.7.6.0"),sQuery(id+"F0.wireOp",EDGE,"E5.7.7.0"),sQuery(id+"F0.wireOp",EDGE,"E5.7.8.0"),sQuery(id+"F0.wireOp",EDGE,"E5.7.9.0"),sQuery(id+"F0.wireOp",EDGE,"E5.7.10.0"),sQuery(id+"F0.wireOp",EDGE,"E5.7.11.0"),sQuery(id+"F0.wireOp",EDGE,"E5.7.12.0"),sQuery(id+"F0.wireOp",EDGE,"E5.8.0.0"),sQuery(id+"F0.wireOp",EDGE,"E5.8.1.0"),sQuery(id+"F0.wireOp",EDGE,"E5.8.2.0"),sQuery(id+"F0.wireOp",EDGE,"E5.8.3.0"),sQuery(id+"F0.wireOp",EDGE,"E5.8.4.0"),sQuery(id+"F0.wireOp",EDGE,"E5.8.5.0"),sQuery(id+"F0.wireOp",EDGE,"E5.8.6.0"),sQuery(id+"F0.wireOp",EDGE,"E5.8.7.0"),sQuery(id+"F0.wireOp",EDGE,"E5.8.8.0"),sQuery(id+"F0.wireOp",EDGE,"E5.8.9.0"),sQuery(id+"F0.wireOp",EDGE,"E5.8.10.0"),sQuery(id+"F0.wireOp",EDGE,"E5.8.11.0"),sQuery(id+"F0.wireOp",EDGE,"E5.8.12.0"),sQuery(id+"F0.wireOp",EDGE,"E5.9.0.0"),sQuery(id+"F0.wireOp",EDGE,"E5.9.1.0"),sQuery(id+"F0.wireOp",EDGE,"E5.9.2.0"),sQuery(id+"F0.wireOp",EDGE,"E5.9.3.0"),sQuery(id+"F0.wireOp",EDGE,"E5.9.4.0"),sQuery(id+"F0.wireOp",EDGE,"E5.9.5.0"),sQuery(id+"F0.wireOp",EDGE,"E5.9.6.0"),sQuery(id+"F0.wireOp",EDGE,"E5.9.7.0"),sQuery(id+"F0.wireOp",EDGE,"E5.9.8.0"),sQuery(id+"F0.wireOp",EDGE,"E5.9.9.0"),sQuery(id+"F0.wireOp",EDGE,"E5.9.10.0"),sQuery(id+"F0.wireOp",EDGE,"E5.9.11.0"),sQuery(id+"F0.wireOp",EDGE,"E5.9.12.0"),sQuery(id+"F0.wireOp",EDGE,"E5.10.0.0"),sQuery(id+"F0.wireOp",EDGE,"E5.10.1.0"),sQuery(id+"F0.wireOp",EDGE,"E5.10.2.0"),sQuery(id+"F0.wireOp",EDGE,"E5.10.3.0"),sQuery(id+"F0.wireOp",EDGE,"E5.10.4.0"),sQuery(id+"F0.wireOp",EDGE,"E5.10.5.0"),sQuery(id+"F0.wireOp",EDGE,"E5.10.6.0"),sQuery(id+"F0.wireOp",EDGE,"E5.10.7.0"),sQuery(id+"F0.wireOp",EDGE,"E5.10.8.0"),sQuery(id+"F0.wireOp",EDGE,"E5.10.9.0"),sQuery(id+"F0.wireOp",EDGE,"E5.10.10.0"),sQuery(id+"F0.wireOp",EDGE,"E5.10.11.0"),sQuery(id+"F0.wireOp",EDGE,"E5.10.12.0"),sQuery(id+"F0.wireOp",EDGE,"E5.11.0.0"),sQuery(id+"F0.wireOp",EDGE,"E5.11.1.0"),sQuery(id+"F0.wireOp",EDGE,"E5.11.2.0"),sQuery(id+"F0.wireOp",EDGE,"E5.11.3.0"),sQuery(id+"F0.wireOp",EDGE,"E5.11.4.0"),sQuery(id+"F0.wireOp",EDGE,"E5.11.5.0"),sQuery(id+"F0.wireOp",EDGE,"E5.11.6.0"),sQuery(id+"F0.wireOp",EDGE,"E5.11.7.0"),sQuery(id+"F0.wireOp",EDGE,"E5.11.8.0"),sQuery(id+"F0.wireOp",EDGE,"E5.11.9.0"),sQuery(id+"F0.wireOp",EDGE,"E5.11.10.0"),sQuery(id+"F0.wireOp",EDGE,"E5.11.11.0"),sQuery(id+"F0.wireOp",EDGE,"E5.11.12.0"),sQuery(id+"F0.wireOp",EDGE,"E5.12.0.0"),sQuery(id+"F0.wireOp",EDGE,"E5.12.1.0"),sQuery(id+"F0.wireOp",EDGE,"E5.12.2.0"),sQuery(id+"F0.wireOp",EDGE,"E5.12.3.0"),sQuery(id+"F0.wireOp",EDGE,"E5.12.4.0"),sQuery(id+"F0.wireOp",EDGE,"E5.12.5.0"),sQuery(id+"F0.wireOp",EDGE,"E5.12.6.0"),sQuery(id+"F0.wireOp",EDGE,"E5.12.7.0"),sQuery(id+"F0.wireOp",EDGE,"E5.12.8.0"),sQuery(id+"F0.wireOp",EDGE,"E5.12.9.0"),sQuery(id+"F0.wireOp",EDGE,"E5.12.10.0"),sQuery(id+"F0.wireOp",EDGE,"E5.12.11.0"),sQuery(id+"F0.wireOp",EDGE,"E5.12.12.0")])],"isStart":true});
            extrude(context, id + "F3", {"entities" : qUnion([Q0]), "operationType" : NewBodyOperationType.REMOVE, "endBound" : BoundingType.UP_TO_SURFACE, "oppositeDirection" : true, "endBoundEntityFace" : qUnion([Q1]), "depth" : 25.4 * mm});
        }
    });
